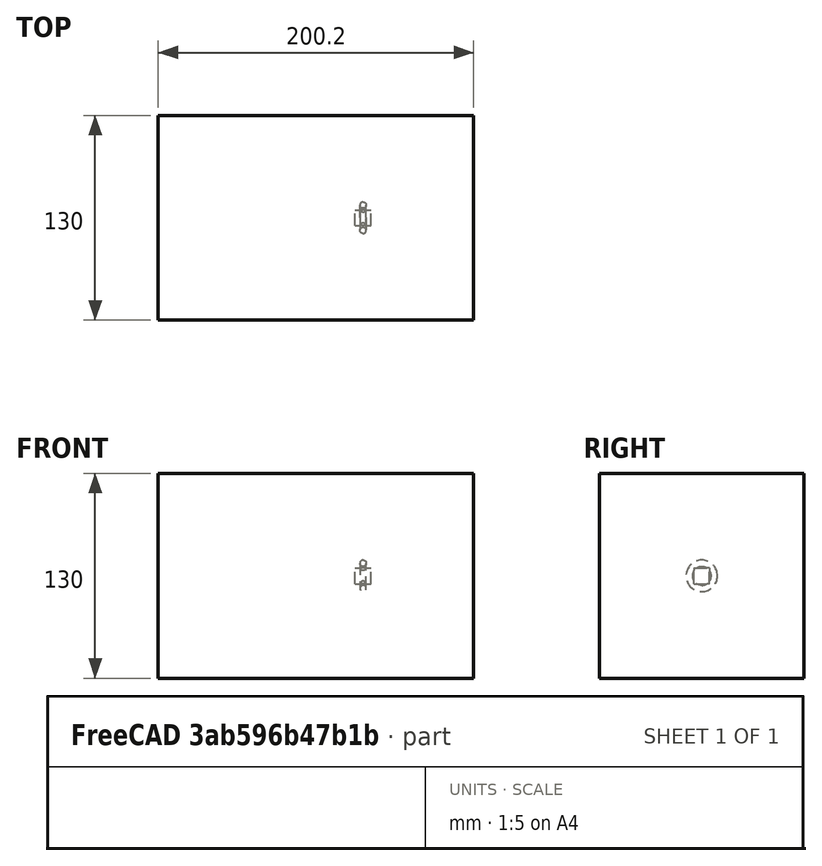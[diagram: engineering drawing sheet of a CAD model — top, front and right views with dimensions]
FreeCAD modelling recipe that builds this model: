
FCSTD DOCUMENT  (FreeCAD 0.21R33694 (Git))
Label: polarArray-7-array-translated
License: All rights reserved
objects: App::DocumentObjectGroupPython×1251, Part::FeaturePython×4, App::Part×2, Part::MultiFuse×1
note: 4 computed .brp shape members not serialized (recipe doc carries the construction recipe); baked Part::Feature solids carry a one-line shape summary decoded from their .brp

FEATURE [App::DocumentObjectGroupPython] HALFPI  # scripted group (container) (typed FeaturePython)
  name = HALFPI
  value = pi/2.
FEATURE [App::DocumentObjectGroupPython] PI  # scripted group (container) (typed FeaturePython)
  name = PI
  value = 1.*pi
FEATURE [App::DocumentObjectGroupPython] TWOPI  # scripted group (container) (typed FeaturePython)
  name = TWOPI
  value = 2.*pi
FEATURE [App::DocumentObjectGroupPython] Constants  # scripted group (container) (typed FeaturePython)
  Group = -> [HALFPI,PI,TWOPI]
FEATURE [App::DocumentObjectGroupPython] Variables  # scripted group (container) (typed FeaturePython)
FEATURE [App::DocumentObjectGroupPython] Quantities  # scripted group (container) (typed FeaturePython)
FEATURE [App::DocumentObjectGroupPython] Isotopes  # scripted group (container) (typed FeaturePython)
FEATURE [App::DocumentObjectGroupPython] Elements  # scripted group (container) (typed FeaturePython)
FEATURE [App::DocumentObjectGroupPython] Matrix  # scripted group (container) (typed FeaturePython)
FEATURE [App::DocumentObjectGroupPython] Surfaces  # scripted group (container) (typed FeaturePython)
FEATURE [App::DocumentObjectGroupPython] Opticals  # scripted group (container) (typed FeaturePython)
  Group = -> [Matrix,Surfaces]
FEATURE [App::DocumentObjectGroupPython] G4Isotopes  # scripted group (container) (typed FeaturePython)
FEATURE [App::DocumentObjectGroupPython] H_element  # scripted group (container) (typed FeaturePython)
  Z = 1
  atom_value = 1.008
  formula = H
  name = H_element
FEATURE [App::DocumentObjectGroupPython] He_element  # scripted group (container) (typed FeaturePython)
  Z = 2
  atom_value = 4.0026
  formula = He
  name = He_element
FEATURE [App::DocumentObjectGroupPython] Li_element  # scripted group (container) (typed FeaturePython)
  Z = 3
  atom_value = 6.94
  formula = Li
  name = Li_element
FEATURE [App::DocumentObjectGroupPython] Be_element  # scripted group (container) (typed FeaturePython)
  Z = 4
  atom_value = 9.01218
  formula = Be
  name = Be_element
FEATURE [App::DocumentObjectGroupPython] B_element  # scripted group (container) (typed FeaturePython)
  Z = 5
  atom_value = 10.81
  formula = B
  name = B_element
FEATURE [App::DocumentObjectGroupPython] C_element  # scripted group (container) (typed FeaturePython)
  Z = 6
  atom_value = 12.011
  formula = C
  name = C_element
FEATURE [App::DocumentObjectGroupPython] N_element  # scripted group (container) (typed FeaturePython)
  Z = 7
  atom_value = 14.007
  formula = N
  name = N_element
FEATURE [App::DocumentObjectGroupPython] O_element  # scripted group (container) (typed FeaturePython)
  Z = 8
  atom_value = 15.999
  formula = O
  name = O_element
FEATURE [App::DocumentObjectGroupPython] F_element  # scripted group (container) (typed FeaturePython)
  Z = 9
  atom_value = 18.9984
  formula = F
  name = F_element
FEATURE [App::DocumentObjectGroupPython] Ne_element  # scripted group (container) (typed FeaturePython)
  Z = 10
  atom_value = 20.1797
  formula = Ne
  name = Ne_element
FEATURE [App::DocumentObjectGroupPython] Na_element  # scripted group (container) (typed FeaturePython)
  Z = 11
  atom_value = 22.9898
  formula = Na
  name = Na_element
FEATURE [App::DocumentObjectGroupPython] Mg_element  # scripted group (container) (typed FeaturePython)
  Z = 12
  atom_value = 24.305
  formula = Mg
  name = Mg_element
FEATURE [App::DocumentObjectGroupPython] Al_element  # scripted group (container) (typed FeaturePython)
  Z = 13
  atom_value = 26.9815
  formula = Al
  name = Al_element
FEATURE [App::DocumentObjectGroupPython] Si_element  # scripted group (container) (typed FeaturePython)
  Z = 14
  atom_value = 28.085
  formula = Si
  name = Si_element
FEATURE [App::DocumentObjectGroupPython] P_element  # scripted group (container) (typed FeaturePython)
  Z = 15
  atom_value = 30.9738
  formula = P
  name = P_element
FEATURE [App::DocumentObjectGroupPython] S_element  # scripted group (container) (typed FeaturePython)
  Z = 16
  atom_value = 32.06
  formula = S
  name = S_element
FEATURE [App::DocumentObjectGroupPython] Cl_element  # scripted group (container) (typed FeaturePython)
  Z = 17
  atom_value = 35.45
  formula = Cl
  name = Cl_element
FEATURE [App::DocumentObjectGroupPython] Ar_element  # scripted group (container) (typed FeaturePython)
  Z = 18
  atom_value = 39.95
  formula = Ar
  name = Ar_element
FEATURE [App::DocumentObjectGroupPython] K_element  # scripted group (container) (typed FeaturePython)
  Z = 19
  atom_value = 39.0983
  formula = K
  name = K_element
FEATURE [App::DocumentObjectGroupPython] Ca_element  # scripted group (container) (typed FeaturePython)
  Z = 20
  atom_value = 40.078
  formula = Ca
  name = Ca_element
FEATURE [App::DocumentObjectGroupPython] Sc_element  # scripted group (container) (typed FeaturePython)
  Z = 21
  atom_value = 44.9559
  formula = Sc
  name = Sc_element
FEATURE [App::DocumentObjectGroupPython] Ti_element  # scripted group (container) (typed FeaturePython)
  Z = 22
  atom_value = 47.867
  formula = Ti
  name = Ti_element
FEATURE [App::DocumentObjectGroupPython] V_element  # scripted group (container) (typed FeaturePython)
  Z = 23
  atom_value = 50.9415
  formula = V
  name = V_element
FEATURE [App::DocumentObjectGroupPython] Cr_element  # scripted group (container) (typed FeaturePython)
  Z = 24
  atom_value = 51.9961
  formula = Cr
  name = Cr_element
FEATURE [App::DocumentObjectGroupPython] Mn_element  # scripted group (container) (typed FeaturePython)
  Z = 25
  atom_value = 54.938
  formula = Mn
  name = Mn_element
FEATURE [App::DocumentObjectGroupPython] Fe_element  # scripted group (container) (typed FeaturePython)
  Z = 26
  atom_value = 55.845
  formula = Fe
  name = Fe_element
FEATURE [App::DocumentObjectGroupPython] Co_element  # scripted group (container) (typed FeaturePython)
  Z = 27
  atom_value = 58.9332
  formula = Co
  name = Co_element
FEATURE [App::DocumentObjectGroupPython] Ni_element  # scripted group (container) (typed FeaturePython)
  Z = 28
  atom_value = 58.6934
  formula = Ni
  name = Ni_element
FEATURE [App::DocumentObjectGroupPython] Cu_element  # scripted group (container) (typed FeaturePython)
  Z = 29
  atom_value = 63.546
  formula = Cu
  name = Cu_element
FEATURE [App::DocumentObjectGroupPython] Zn_element  # scripted group (container) (typed FeaturePython)
  Z = 30
  atom_value = 65.38
  formula = Zn
  name = Zn_element
FEATURE [App::DocumentObjectGroupPython] Ga_element  # scripted group (container) (typed FeaturePython)
  Z = 31
  atom_value = 69.723
  formula = Ga
  name = Ga_element
FEATURE [App::DocumentObjectGroupPython] Ge_element  # scripted group (container) (typed FeaturePython)
  Z = 32
  atom_value = 72.63
  formula = Ge
  name = Ge_element
FEATURE [App::DocumentObjectGroupPython] As_element  # scripted group (container) (typed FeaturePython)
  Z = 33
  atom_value = 74.9216
  formula = As
  name = As_element
FEATURE [App::DocumentObjectGroupPython] Se_element  # scripted group (container) (typed FeaturePython)
  Z = 34
  atom_value = 78.971
  formula = Se
  name = Se_element
FEATURE [App::DocumentObjectGroupPython] Br_element  # scripted group (container) (typed FeaturePython)
  Z = 35
  atom_value = 79.904
  formula = Br
  name = Br_element
FEATURE [App::DocumentObjectGroupPython] Kr_element  # scripted group (container) (typed FeaturePython)
  Z = 36
  atom_value = 83.798
  formula = Kr
  name = Kr_element
FEATURE [App::DocumentObjectGroupPython] Rb_element  # scripted group (container) (typed FeaturePython)
  Z = 37
  atom_value = 85.4678
  formula = Rb
  name = Rb_element
FEATURE [App::DocumentObjectGroupPython] Sr_element  # scripted group (container) (typed FeaturePython)
  Z = 38
  atom_value = 87.62
  formula = Sr
  name = Sr_element
FEATURE [App::DocumentObjectGroupPython] Y_element  # scripted group (container) (typed FeaturePython)
  Z = 39
  atom_value = 88.9058
  formula = Y
  name = Y_element
FEATURE [App::DocumentObjectGroupPython] Zr_element  # scripted group (container) (typed FeaturePython)
  Z = 40
  atom_value = 91.224
  formula = Zr
  name = Zr_element
FEATURE [App::DocumentObjectGroupPython] Nb_element  # scripted group (container) (typed FeaturePython)
  Z = 41
  atom_value = 92.9064
  formula = Nb
  name = Nb_element
FEATURE [App::DocumentObjectGroupPython] Mo_element  # scripted group (container) (typed FeaturePython)
  Z = 42
  atom_value = 95.95
  formula = Mo
  name = Mo_element
FEATURE [App::DocumentObjectGroupPython] Tc_element  # scripted group (container) (typed FeaturePython)
  Z = 43
  atom_value = 97
  formula = Tc
  name = Tc_element
FEATURE [App::DocumentObjectGroupPython] Ru_element  # scripted group (container) (typed FeaturePython)
  Z = 44
  atom_value = 101.07
  formula = Ru
  name = Ru_element
FEATURE [App::DocumentObjectGroupPython] Rh_element  # scripted group (container) (typed FeaturePython)
  Z = 45
  atom_value = 102.905
  formula = Rh
  name = Rh_element
FEATURE [App::DocumentObjectGroupPython] Pd_element  # scripted group (container) (typed FeaturePython)
  Z = 46
  atom_value = 106.42
  formula = Pd
  name = Pd_element
FEATURE [App::DocumentObjectGroupPython] Ag_element  # scripted group (container) (typed FeaturePython)
  Z = 47
  atom_value = 107.868
  formula = Ag
  name = Ag_element
FEATURE [App::DocumentObjectGroupPython] Cd_element  # scripted group (container) (typed FeaturePython)
  Z = 48
  atom_value = 112.414
  formula = Cd
  name = Cd_element
FEATURE [App::DocumentObjectGroupPython] In_element  # scripted group (container) (typed FeaturePython)
  Z = 49
  atom_value = 114.818
  formula = In
  name = In_element
FEATURE [App::DocumentObjectGroupPython] Sn_element  # scripted group (container) (typed FeaturePython)
  Z = 50
  atom_value = 118.71
  formula = Sn
  name = Sn_element
FEATURE [App::DocumentObjectGroupPython] Sb_element  # scripted group (container) (typed FeaturePython)
  Z = 51
  atom_value = 121.76
  formula = Sb
  name = Sb_element
FEATURE [App::DocumentObjectGroupPython] Te_element  # scripted group (container) (typed FeaturePython)
  Z = 52
  atom_value = 127.6
  formula = Te
  name = Te_element
FEATURE [App::DocumentObjectGroupPython] I_element  # scripted group (container) (typed FeaturePython)
  Z = 53
  atom_value = 126.904
  formula = I
  name = I_element
FEATURE [App::DocumentObjectGroupPython] Xe_element  # scripted group (container) (typed FeaturePython)
  Z = 54
  atom_value = 131.293
  formula = Xe
  name = Xe_element
FEATURE [App::DocumentObjectGroupPython] Cs_element  # scripted group (container) (typed FeaturePython)
  Z = 55
  atom_value = 132.905
  formula = Cs
  name = Cs_element
FEATURE [App::DocumentObjectGroupPython] Ba_element  # scripted group (container) (typed FeaturePython)
  Z = 56
  atom_value = 137.327
  formula = Ba
  name = Ba_element
FEATURE [App::DocumentObjectGroupPython] La_element  # scripted group (container) (typed FeaturePython)
  Z = 57
  atom_value = 138.905
  formula = La
  name = La_element
FEATURE [App::DocumentObjectGroupPython] Ce_element  # scripted group (container) (typed FeaturePython)
  Z = 58
  atom_value = 140.116
  formula = Ce
  name = Ce_element
FEATURE [App::DocumentObjectGroupPython] Pr_element  # scripted group (container) (typed FeaturePython)
  Z = 59
  atom_value = 140.908
  formula = Pr
  name = Pr_element
FEATURE [App::DocumentObjectGroupPython] Nd_element  # scripted group (container) (typed FeaturePython)
  Z = 60
  atom_value = 144.242
  formula = Nd
  name = Nd_element
FEATURE [App::DocumentObjectGroupPython] Pm_element  # scripted group (container) (typed FeaturePython)
  Z = 61
  atom_value = 145
  formula = Pm
  name = Pm_element
FEATURE [App::DocumentObjectGroupPython] Sm_element  # scripted group (container) (typed FeaturePython)
  Z = 62
  atom_value = 150.36
  formula = Sm
  name = Sm_element
FEATURE [App::DocumentObjectGroupPython] Eu_element  # scripted group (container) (typed FeaturePython)
  Z = 63
  atom_value = 151.964
  formula = Eu
  name = Eu_element
FEATURE [App::DocumentObjectGroupPython] Gd_element  # scripted group (container) (typed FeaturePython)
  Z = 64
  atom_value = 157.25
  formula = Gd
  name = Gd_element
FEATURE [App::DocumentObjectGroupPython] Tb_element  # scripted group (container) (typed FeaturePython)
  Z = 65
  atom_value = 158.925
  formula = Tb
  name = Tb_element
FEATURE [App::DocumentObjectGroupPython] Dy_element  # scripted group (container) (typed FeaturePython)
  Z = 66
  atom_value = 162.5
  formula = Dy
  name = Dy_element
FEATURE [App::DocumentObjectGroupPython] Ho_element  # scripted group (container) (typed FeaturePython)
  Z = 67
  atom_value = 164.93
  formula = Ho
  name = Ho_element
FEATURE [App::DocumentObjectGroupPython] Er_element  # scripted group (container) (typed FeaturePython)
  Z = 68
  atom_value = 167.259
  formula = Er
  name = Er_element
FEATURE [App::DocumentObjectGroupPython] Tm_element  # scripted group (container) (typed FeaturePython)
  Z = 69
  atom_value = 168.934
  formula = Tm
  name = Tm_element
FEATURE [App::DocumentObjectGroupPython] Yb_element  # scripted group (container) (typed FeaturePython)
  Z = 70
  atom_value = 173.045
  formula = Yb
  name = Yb_element
FEATURE [App::DocumentObjectGroupPython] Lu_element  # scripted group (container) (typed FeaturePython)
  Z = 71
  atom_value = 174.967
  formula = Lu
  name = Lu_element
FEATURE [App::DocumentObjectGroupPython] Hf_element  # scripted group (container) (typed FeaturePython)
  Z = 72
  atom_value = 178.49
  formula = Hf
  name = Hf_element
FEATURE [App::DocumentObjectGroupPython] Ta_element  # scripted group (container) (typed FeaturePython)
  Z = 73
  atom_value = 180.948
  formula = Ta
  name = Ta_element
FEATURE [App::DocumentObjectGroupPython] W_element  # scripted group (container) (typed FeaturePython)
  Z = 74
  atom_value = 183.84
  formula = W
  name = W_element
FEATURE [App::DocumentObjectGroupPython] Re_element  # scripted group (container) (typed FeaturePython)
  Z = 75
  atom_value = 186.207
  formula = Re
  name = Re_element
FEATURE [App::DocumentObjectGroupPython] Os_element  # scripted group (container) (typed FeaturePython)
  Z = 76
  atom_value = 190.23
  formula = Os
  name = Os_element
FEATURE [App::DocumentObjectGroupPython] Ir_element  # scripted group (container) (typed FeaturePython)
  Z = 77
  atom_value = 192.217
  formula = Ir
  name = Ir_element
FEATURE [App::DocumentObjectGroupPython] Pt_element  # scripted group (container) (typed FeaturePython)
  Z = 78
  atom_value = 195.084
  formula = Pt
  name = Pt_element
FEATURE [App::DocumentObjectGroupPython] Au_element  # scripted group (container) (typed FeaturePython)
  Z = 79
  atom_value = 196.967
  formula = Au
  name = Au_element
FEATURE [App::DocumentObjectGroupPython] Hg_element  # scripted group (container) (typed FeaturePython)
  Z = 80
  atom_value = 200.592
  formula = Hg
  name = Hg_element
FEATURE [App::DocumentObjectGroupPython] Tl_element  # scripted group (container) (typed FeaturePython)
  Z = 81
  atom_value = 204.38
  formula = Tl
  name = Tl_element
FEATURE [App::DocumentObjectGroupPython] Pb_element  # scripted group (container) (typed FeaturePython)
  Z = 82
  atom_value = 207.2
  formula = Pb
  name = Pb_element
FEATURE [App::DocumentObjectGroupPython] Bi_element  # scripted group (container) (typed FeaturePython)
  Z = 83
  atom_value = 208.98
  formula = Bi
  name = Bi_element
FEATURE [App::DocumentObjectGroupPython] Po_element  # scripted group (container) (typed FeaturePython)
  Z = 84
  atom_value = 209
  formula = Po
  name = Po_element
FEATURE [App::DocumentObjectGroupPython] At_element  # scripted group (container) (typed FeaturePython)
  Z = 85
  atom_value = 210
  formula = At
  name = At_element
FEATURE [App::DocumentObjectGroupPython] Rn_element  # scripted group (container) (typed FeaturePython)
  Z = 86
  atom_value = 222
  formula = Rn
  name = Rn_element
FEATURE [App::DocumentObjectGroupPython] Fr_element  # scripted group (container) (typed FeaturePython)
  Z = 87
  atom_value = 223
  formula = Fr
  name = Fr_element
FEATURE [App::DocumentObjectGroupPython] Ra_element  # scripted group (container) (typed FeaturePython)
  Z = 88
  atom_value = 226
  formula = Ra
  name = Ra_element
FEATURE [App::DocumentObjectGroupPython] Ac_element  # scripted group (container) (typed FeaturePython)
  Z = 89
  atom_value = 227
  formula = Ac
  name = Ac_element
FEATURE [App::DocumentObjectGroupPython] Th_element  # scripted group (container) (typed FeaturePython)
  Z = 90
  atom_value = 232.038
  formula = Th
  name = Th_element
FEATURE [App::DocumentObjectGroupPython] Pa_element  # scripted group (container) (typed FeaturePython)
  Z = 91
  atom_value = 231.036
  formula = Pa
  name = Pa_element
FEATURE [App::DocumentObjectGroupPython] U_element  # scripted group (container) (typed FeaturePython)
  Z = 92
  atom_value = 238.029
  formula = U
  name = U_element
FEATURE [App::DocumentObjectGroupPython] Np_element  # scripted group (container) (typed FeaturePython)
  Z = 93
  atom_value = 237
  formula = Np
  name = Np_element
FEATURE [App::DocumentObjectGroupPython] Pu_element  # scripted group (container) (typed FeaturePython)
  Z = 94
  atom_value = 244
  formula = Pu
  name = Pu_element
FEATURE [App::DocumentObjectGroupPython] Am_element  # scripted group (container) (typed FeaturePython)
  Z = 95
  atom_value = 243
  formula = Am
  name = Am_element
FEATURE [App::DocumentObjectGroupPython] Cm_element  # scripted group (container) (typed FeaturePython)
  Z = 96
  atom_value = 247
  formula = Cm
  name = Cm_element
FEATURE [App::DocumentObjectGroupPython] Bk_element  # scripted group (container) (typed FeaturePython)
  Z = 97
  atom_value = 247
  formula = Bk
  name = Bk_element
FEATURE [App::DocumentObjectGroupPython] Cf_element  # scripted group (container) (typed FeaturePython)
  Z = 98
  atom_value = 251
  formula = Cf
  name = Cf_element
FEATURE [App::DocumentObjectGroupPython] G4Elements  # scripted group (container) (typed FeaturePython)
  Group = -> [H_element,He_element,Li_element,Be_element,B_element,C_element,N_element,O_element,F_element,Ne_element,Na_element,Mg_element,Al_element,Si_element,P_element,S_element,Cl_element,Ar_element,K_element,Ca_element,Sc_element,Ti_element,V_element,Cr_element,Mn_element,Fe_element,Co_element,Ni_element,Cu_element,Zn_element,Ga_element,Ge_element,As_element,Se_element,Br_element,Kr_element,Rb_element,+61 more]
FEATURE [App::DocumentObjectGroupPython] H_element001  label="H_element : 0.101"  # scripted group (container) (typed FeaturePython)
  n = 0.101327
FEATURE [App::DocumentObjectGroupPython] C_element001  label="C_element : 0.775"  # scripted group (container) (typed FeaturePython)
  n = 0.7755
FEATURE [App::DocumentObjectGroupPython] N_element001  label="N_element : 0.035"  # scripted group (container) (typed FeaturePython)
  n = 0.035057
FEATURE [App::DocumentObjectGroupPython] O_element001  label="O_element : 0.052"  # scripted group (container) (typed FeaturePython)
  n = 0.0523159
FEATURE [App::DocumentObjectGroupPython] F_element001  label="F_element : 0.017"  # scripted group (container) (typed FeaturePython)
  n = 0.017422
FEATURE [App::DocumentObjectGroupPython] Ca_element001  label="Ca_element : 0.018"  # scripted group (container) (typed FeaturePython)
  n = 0.018378
FEATURE [App::DocumentObjectGroupPython] G4_A_150_TISSUE  label="G4_A-150_TISSUE"  # scripted group (container) (typed FeaturePython)
  Dunit = g/cm3
  Dvalue = 1.127
  Group = -> [H_element001,C_element001,N_element001,O_element001,F_element001,Ca_element001]
  conduct = 2
  density = 1
  expand = 3
  formula = G4_A-150_TISSUE
  name = G4_A-150_TISSUE
  specific = 4
FEATURE [App::DocumentObjectGroupPython] C_element002  label="C_element : 3"  # scripted group (container) (typed FeaturePython)
  n = 3
  ref = C_element
FEATURE [App::DocumentObjectGroupPython] H_element002  label="H_element : 6"  # scripted group (container) (typed FeaturePython)
  n = 6
  ref = H_element
FEATURE [App::DocumentObjectGroupPython] O_element002  label="O_element : 1"  # scripted group (container) (typed FeaturePython)
  n = 1
  ref = O_element
FEATURE [App::DocumentObjectGroupPython] G4_ACETONE  # scripted group (container) (typed FeaturePython)
  Dunit = g/cm3
  Dvalue = 0.7899
  Group = -> [C_element002,H_element002,O_element002]
  conduct = 2
  density = 1
  expand = 3
  formula = G4_ACETONE
  name = G4_ACETONE
  specific = 4
FEATURE [App::DocumentObjectGroupPython] C_element003  label="C_element : 2"  # scripted group (container) (typed FeaturePython)
  n = 2
  ref = C_element
FEATURE [App::DocumentObjectGroupPython] H_element003  label="H_element : 2"  # scripted group (container) (typed FeaturePython)
  n = 2
  ref = H_element
FEATURE [App::DocumentObjectGroupPython] G4_ACETYLENE  # scripted group (container) (typed FeaturePython)
  Dunit = g/cm3
  Dvalue = 0.0010967
  Group = -> [C_element003,H_element003]
  conduct = 2
  density = 1
  expand = 3
  formula = G4_ACETYLENE
  name = G4_ACETYLENE
  specific = 4
FEATURE [App::DocumentObjectGroupPython] C_element004  label="C_element : 5"  # scripted group (container) (typed FeaturePython)
  n = 5
  ref = C_element
FEATURE [App::DocumentObjectGroupPython] H_element004  label="H_element : 5"  # scripted group (container) (typed FeaturePython)
  n = 5
  ref = H_element
FEATURE [App::DocumentObjectGroupPython] N_element002  label="N_element : 5"  # scripted group (container) (typed FeaturePython)
  n = 5
  ref = N_element
FEATURE [App::DocumentObjectGroupPython] G4_ADENINE  # scripted group (container) (typed FeaturePython)
  Dunit = g/cm3
  Dvalue = 1.6
  Group = -> [C_element004,H_element004,N_element002]
  conduct = 2
  density = 1
  expand = 3
  formula = G4_ADENINE
  name = G4_ADENINE
  specific = 4
FEATURE [App::DocumentObjectGroupPython] H_element005  label="H_element : 0.114"  # scripted group (container) (typed FeaturePython)
  n = 0.114
FEATURE [App::DocumentObjectGroupPython] C_element005  label="C_element : 0.598"  # scripted group (container) (typed FeaturePython)
  n = 0.598
FEATURE [App::DocumentObjectGroupPython] N_element003  label="N_element : 0.007"  # scripted group (container) (typed FeaturePython)
  n = 0.007
FEATURE [App::DocumentObjectGroupPython] O_element003  label="O_element : 0.278"  # scripted group (container) (typed FeaturePython)
  n = 0.278
FEATURE [App::DocumentObjectGroupPython] Na_element001  label="Na_element : 0.001"  # scripted group (container) (typed FeaturePython)
  n = 0.001
FEATURE [App::DocumentObjectGroupPython] S_element001  label="S_element : 0.001"  # scripted group (container) (typed FeaturePython)
  n = 0.001
FEATURE [App::DocumentObjectGroupPython] Cl_element001  label="Cl_element : 0.001"  # scripted group (container) (typed FeaturePython)
  n = 0.001
FEATURE [App::DocumentObjectGroupPython] G4_ADIPOSE_TISSUE_ICRP  # scripted group (container) (typed FeaturePython)
  Dunit = g/cm3
  Dvalue = 0.95
  Group = -> [H_element005,C_element005,N_element003,O_element003,Na_element001,S_element001,Cl_element001]
  conduct = 2
  density = 1
  expand = 3
  formula = G4_ADIPOSE_TISSUE_ICRP
  name = G4_ADIPOSE_TISSUE_ICRP
  specific = 4
FEATURE [App::DocumentObjectGroupPython] C_element006  label="C_element : 0.000"  # scripted group (container) (typed FeaturePython)
  n = 0.000124
FEATURE [App::DocumentObjectGroupPython] N_element004  label="N_element : 0.755"  # scripted group (container) (typed FeaturePython)
  n = 0.755268
FEATURE [App::DocumentObjectGroupPython] O_element004  label="O_element : 0.232"  # scripted group (container) (typed FeaturePython)
  n = 0.231781
FEATURE [App::DocumentObjectGroupPython] Ar_element001  label="Ar_element : 0.013"  # scripted group (container) (typed FeaturePython)
  n = 0.012827
FEATURE [App::DocumentObjectGroupPython] G4_AIR  # scripted group (container) (typed FeaturePython)
  Dunit = g/cm3
  Dvalue = 0.00120479
  Group = -> [C_element006,N_element004,O_element004,Ar_element001]
  conduct = 2
  density = 1
  expand = 3
  formula = G4_AIR
  name = G4_AIR
  specific = 4
FEATURE [App::DocumentObjectGroupPython] C_element007  label="C_element : 006"  # scripted group (container) (typed FeaturePython)
  n = 3
  ref = C_element
FEATURE [App::DocumentObjectGroupPython] H_element006  label="H_element : 7"  # scripted group (container) (typed FeaturePython)
  n = 7
  ref = H_element
FEATURE [App::DocumentObjectGroupPython] N_element005  label="N_element : 1"  # scripted group (container) (typed FeaturePython)
  n = 1
  ref = N_element
FEATURE [App::DocumentObjectGroupPython] O_element005  label="O_element : 2"  # scripted group (container) (typed FeaturePython)
  n = 2
  ref = O_element
FEATURE [App::DocumentObjectGroupPython] G4_ALANINE  # scripted group (container) (typed FeaturePython)
  Dunit = g/cm3
  Dvalue = 1.42
  Group = -> [C_element007,H_element006,N_element005,O_element005]
  conduct = 2
  density = 1
  expand = 3
  formula = G4_ALANINE
  name = G4_ALANINE
  specific = 4
FEATURE [App::DocumentObjectGroupPython] Al_element001  label="Al_element : 2"  # scripted group (container) (typed FeaturePython)
  n = 2
  ref = Al_element
FEATURE [App::DocumentObjectGroupPython] O_element006  label="O_element : 3"  # scripted group (container) (typed FeaturePython)
  n = 3
  ref = O_element
FEATURE [App::DocumentObjectGroupPython] G4_ALUMINUM_OXIDE  # scripted group (container) (typed FeaturePython)
  Dunit = g/cm3
  Dvalue = 3.97
  Group = -> [Al_element001,O_element006]
  conduct = 2
  density = 1
  expand = 3
  formula = G4_ALUMINUM_OXIDE
  name = G4_ALUMINUM_OXIDE
  specific = 4
FEATURE [App::DocumentObjectGroupPython] H_element007  label="H_element : 0.106"  # scripted group (container) (typed FeaturePython)
  n = 0.10593
FEATURE [App::DocumentObjectGroupPython] C_element008  label="C_element : 0.789"  # scripted group (container) (typed FeaturePython)
  n = 0.788974
FEATURE [App::DocumentObjectGroupPython] O_element007  label="O_element : 0.105"  # scripted group (container) (typed FeaturePython)
  n = 0.105096
FEATURE [App::DocumentObjectGroupPython] G4_AMBER  # scripted group (container) (typed FeaturePython)
  Dunit = g/cm3
  Dvalue = 1.1
  Group = -> [H_element007,C_element008,O_element007]
  conduct = 2
  density = 1
  expand = 3
  formula = G4_AMBER
  name = G4_AMBER
  specific = 4
FEATURE [App::DocumentObjectGroupPython] N_element006  label="N_element : 006"  # scripted group (container) (typed FeaturePython)
  n = 1
  ref = N_element
FEATURE [App::DocumentObjectGroupPython] H_element008  label="H_element : 3"  # scripted group (container) (typed FeaturePython)
  n = 3
  ref = H_element
FEATURE [App::DocumentObjectGroupPython] G4_AMMONIA  # scripted group (container) (typed FeaturePython)
  Dunit = g/cm3
  Dvalue = 0.000826019
  Group = -> [N_element006,H_element008]
  conduct = 2
  density = 1
  expand = 3
  formula = G4_AMMONIA
  name = G4_AMMONIA
  specific = 4
FEATURE [App::DocumentObjectGroupPython] C_element009  label="C_element : 6"  # scripted group (container) (typed FeaturePython)
  n = 6
  ref = C_element
FEATURE [App::DocumentObjectGroupPython] H_element009  label="H_element : 008"  # scripted group (container) (typed FeaturePython)
  n = 7
  ref = H_element
FEATURE [App::DocumentObjectGroupPython] N_element007  label="N_element : 007"  # scripted group (container) (typed FeaturePython)
  n = 1
  ref = N_element
FEATURE [App::DocumentObjectGroupPython] G4_ANILINE  # scripted group (container) (typed FeaturePython)
  Dunit = g/cm3
  Dvalue = 1.0235
  Group = -> [C_element009,H_element009,N_element007]
  conduct = 2
  density = 1
  expand = 3
  formula = G4_ANILINE
  name = G4_ANILINE
  specific = 4
FEATURE [App::DocumentObjectGroupPython] C_element010  label="C_element : 14"  # scripted group (container) (typed FeaturePython)
  n = 14
  ref = C_element
FEATURE [App::DocumentObjectGroupPython] H_element010  label="H_element : 10"  # scripted group (container) (typed FeaturePython)
  n = 10
  ref = H_element
FEATURE [App::DocumentObjectGroupPython] G4_ANTHRACENE  # scripted group (container) (typed FeaturePython)
  Dunit = g/cm3
  Dvalue = 1.283
  Group = -> [C_element010,H_element010]
  conduct = 2
  density = 1
  expand = 3
  formula = G4_ANTHRACENE
  name = G4_ANTHRACENE
  specific = 4
FEATURE [App::DocumentObjectGroupPython] H_element011  label="H_element : 0.065"  # scripted group (container) (typed FeaturePython)
  n = 0.0654709
FEATURE [App::DocumentObjectGroupPython] C_element011  label="C_element : 0.537"  # scripted group (container) (typed FeaturePython)
  n = 0.536944
FEATURE [App::DocumentObjectGroupPython] N_element008  label="N_element : 0.021"  # scripted group (container) (typed FeaturePython)
  n = 0.0215
FEATURE [App::DocumentObjectGroupPython] O_element008  label="O_element : 0.032"  # scripted group (container) (typed FeaturePython)
  n = 0.032085
FEATURE [App::DocumentObjectGroupPython] F_element002  label="F_element : 0.167"  # scripted group (container) (typed FeaturePython)
  n = 0.167411
FEATURE [App::DocumentObjectGroupPython] Ca_element002  label="Ca_element : 0.177"  # scripted group (container) (typed FeaturePython)
  n = 0.176589
FEATURE [App::DocumentObjectGroupPython] G4_B_100_BONE  label="G4_B-100_BONE"  # scripted group (container) (typed FeaturePython)
  Dunit = g/cm3
  Dvalue = 1.45
  Group = -> [H_element011,C_element011,N_element008,O_element008,F_element002,Ca_element002]
  conduct = 2
  density = 1
  expand = 3
  formula = G4_B-100_BONE
  name = G4_B-100_BONE
  specific = 4
FEATURE [App::DocumentObjectGroupPython] H_element012  label="H_element : 0.057"  # scripted group (container) (typed FeaturePython)
  n = 0.057441
FEATURE [App::DocumentObjectGroupPython] C_element012  label="C_element : 0.790"  # scripted group (container) (typed FeaturePython)
  n = 0.774591
FEATURE [App::DocumentObjectGroupPython] O_element009  label="O_element : 0.168"  # scripted group (container) (typed FeaturePython)
  n = 0.167968
FEATURE [App::DocumentObjectGroupPython] G4_BAKELITE  # scripted group (container) (typed FeaturePython)
  Dunit = g/cm3
  Dvalue = 1.25
  Group = -> [H_element012,C_element012,O_element009]
  conduct = 2
  density = 1
  expand = 3
  formula = G4_BAKELITE
  name = G4_BAKELITE
  specific = 4
FEATURE [App::DocumentObjectGroupPython] Ba_element001  label="Ba_element : 1"  # scripted group (container) (typed FeaturePython)
  n = 1
  ref = Ba_element
FEATURE [App::DocumentObjectGroupPython] F_element003  label="F_element : 2"  # scripted group (container) (typed FeaturePython)
  n = 2
  ref = F_element
FEATURE [App::DocumentObjectGroupPython] G4_BARIUM_FLUORIDE  # scripted group (container) (typed FeaturePython)
  Dunit = g/cm3
  Dvalue = 4.89
  Group = -> [Ba_element001,F_element003]
  conduct = 2
  density = 1
  expand = 3
  formula = G4_BARIUM_FLUORIDE
  name = G4_BARIUM_FLUORIDE
  specific = 4
FEATURE [App::DocumentObjectGroupPython] Ba_element002  label="Ba_element : 002"  # scripted group (container) (typed FeaturePython)
  n = 1
  ref = Ba_element
FEATURE [App::DocumentObjectGroupPython] S_element002  label="S_element : 1"  # scripted group (container) (typed FeaturePython)
  n = 1
  ref = S_element
FEATURE [App::DocumentObjectGroupPython] O_element010  label="O_element : 4"  # scripted group (container) (typed FeaturePython)
  n = 4
  ref = O_element
FEATURE [App::DocumentObjectGroupPython] G4_BARIUM_SULFATE  # scripted group (container) (typed FeaturePython)
  Dunit = g/cm3
  Dvalue = 4.5
  Group = -> [Ba_element002,S_element002,O_element010]
  conduct = 2
  density = 1
  expand = 3
  formula = G4_BARIUM_SULFATE
  name = G4_BARIUM_SULFATE
  specific = 4
FEATURE [App::DocumentObjectGroupPython] C_element013  label="C_element : 007"  # scripted group (container) (typed FeaturePython)
  n = 6
  ref = C_element
FEATURE [App::DocumentObjectGroupPython] H_element013  label="H_element : 009"  # scripted group (container) (typed FeaturePython)
  n = 6
  ref = H_element
FEATURE [App::DocumentObjectGroupPython] G4_BENZENE  # scripted group (container) (typed FeaturePython)
  Dunit = g/cm3
  Dvalue = 0.87865
  Group = -> [C_element013,H_element013]
  conduct = 2
  density = 1
  expand = 3
  formula = G4_BENZENE
  name = G4_BENZENE
  specific = 4
FEATURE [App::DocumentObjectGroupPython] Be_element001  label="Be_element : 1"  # scripted group (container) (typed FeaturePython)
  n = 1
  ref = Be_element
FEATURE [App::DocumentObjectGroupPython] O_element011  label="O_element : 005"  # scripted group (container) (typed FeaturePython)
  n = 1
  ref = O_element
FEATURE [App::DocumentObjectGroupPython] G4_BERYLLIUM_OXIDE  # scripted group (container) (typed FeaturePython)
  Dunit = g/cm3
  Dvalue = 3.01
  Group = -> [Be_element001,O_element011]
  conduct = 2
  density = 1
  expand = 3
  formula = G4_BERYLLIUM_OXIDE
  name = G4_BERYLLIUM_OXIDE
  specific = 4
FEATURE [App::DocumentObjectGroupPython] Bi_element001  label="Bi_element : 4"  # scripted group (container) (typed FeaturePython)
  n = 4
  ref = Bi_element
FEATURE [App::DocumentObjectGroupPython] Ge_element001  label="Ge_element : 3"  # scripted group (container) (typed FeaturePython)
  n = 3
  ref = Ge_element
FEATURE [App::DocumentObjectGroupPython] O_element012  label="O_element : 12"  # scripted group (container) (typed FeaturePython)
  n = 12
  ref = O_element
FEATURE [App::DocumentObjectGroupPython] G4_BGO  # scripted group (container) (typed FeaturePython)
  Dunit = g/cm3
  Dvalue = 7.13
  Group = -> [Bi_element001,Ge_element001,O_element012]
  conduct = 2
  density = 1
  expand = 3
  formula = G4_BGO
  name = G4_BGO
  specific = 4
FEATURE [App::DocumentObjectGroupPython] H_element014  label="H_element : 0.102"  # scripted group (container) (typed FeaturePython)
  n = 0.102
FEATURE [App::DocumentObjectGroupPython] C_element014  label="C_element : 0.110"  # scripted group (container) (typed FeaturePython)
  n = 0.11
FEATURE [App::DocumentObjectGroupPython] N_element009  label="N_element : 0.033"  # scripted group (container) (typed FeaturePython)
  n = 0.033
FEATURE [App::DocumentObjectGroupPython] O_element013  label="O_element : 0.745"  # scripted group (container) (typed FeaturePython)
  n = 0.745
FEATURE [App::DocumentObjectGroupPython] Na_element002  label="Na_element : 0.002"  # scripted group (container) (typed FeaturePython)
  n = 0.001
FEATURE [App::DocumentObjectGroupPython] P_element001  label="P_element : 0.001"  # scripted group (container) (typed FeaturePython)
  n = 0.001
FEATURE [App::DocumentObjectGroupPython] S_element003  label="S_element : 0.002"  # scripted group (container) (typed FeaturePython)
  n = 0.002
FEATURE [App::DocumentObjectGroupPython] Cl_element002  label="Cl_element : 0.003"  # scripted group (container) (typed FeaturePython)
  n = 0.003
FEATURE [App::DocumentObjectGroupPython] K_element001  label="K_element : 0.002"  # scripted group (container) (typed FeaturePython)
  n = 0.002
FEATURE [App::DocumentObjectGroupPython] Fe_element001  label="Fe_element : 0.001"  # scripted group (container) (typed FeaturePython)
  n = 0.001
FEATURE [App::DocumentObjectGroupPython] G4_BLOOD_ICRP  # scripted group (container) (typed FeaturePython)
  Dunit = g/cm3
  Dvalue = 1.06
  Group = -> [H_element014,C_element014,N_element009,O_element013,Na_element002,P_element001,S_element003,Cl_element002,K_element001,Fe_element001]
  conduct = 2
  density = 1
  expand = 3
  formula = G4_BLOOD_ICRP
  name = G4_BLOOD_ICRP
  specific = 4
FEATURE [App::DocumentObjectGroupPython] H_element015  label="H_element : 0.064"  # scripted group (container) (typed FeaturePython)
  n = 0.064
FEATURE [App::DocumentObjectGroupPython] C_element015  label="C_element : 0.278"  # scripted group (container) (typed FeaturePython)
  n = 0.278
FEATURE [App::DocumentObjectGroupPython] N_element010  label="N_element : 0.027"  # scripted group (container) (typed FeaturePython)
  n = 0.027
FEATURE [App::DocumentObjectGroupPython] O_element014  label="O_element : 0.410"  # scripted group (container) (typed FeaturePython)
  n = 0.41
FEATURE [App::DocumentObjectGroupPython] Mg_element001  label="Mg_element : 0.002"  # scripted group (container) (typed FeaturePython)
  n = 0.002
FEATURE [App::DocumentObjectGroupPython] P_element002  label="P_element : 0.070"  # scripted group (container) (typed FeaturePython)
  n = 0.07
FEATURE [App::DocumentObjectGroupPython] S_element004  label="S_element : 0.003"  # scripted group (container) (typed FeaturePython)
  n = 0.002
FEATURE [App::DocumentObjectGroupPython] Ca_element003  label="Ca_element : 0.147"  # scripted group (container) (typed FeaturePython)
  n = 0.147
FEATURE [App::DocumentObjectGroupPython] G4_BONE_COMPACT_ICRU  # scripted group (container) (typed FeaturePython)
  Dunit = g/cm3
  Dvalue = 1.85
  Group = -> [H_element015,C_element015,N_element010,O_element014,Mg_element001,P_element002,S_element004,Ca_element003]
  conduct = 2
  density = 1
  expand = 3
  formula = G4_BONE_COMPACT_ICRU
  name = G4_BONE_COMPACT_ICRU
  specific = 4
FEATURE [App::DocumentObjectGroupPython] H_element016  label="H_element : 0.034"  # scripted group (container) (typed FeaturePython)
  n = 0.034
FEATURE [App::DocumentObjectGroupPython] C_element016  label="C_element : 0.155"  # scripted group (container) (typed FeaturePython)
  n = 0.155
FEATURE [App::DocumentObjectGroupPython] N_element011  label="N_element : 0.042"  # scripted group (container) (typed FeaturePython)
  n = 0.042
FEATURE [App::DocumentObjectGroupPython] O_element015  label="O_element : 0.435"  # scripted group (container) (typed FeaturePython)
  n = 0.435
FEATURE [App::DocumentObjectGroupPython] Na_element003  label="Na_element : 0.003"  # scripted group (container) (typed FeaturePython)
  n = 0.001
FEATURE [App::DocumentObjectGroupPython] Mg_element002  label="Mg_element : 0.003"  # scripted group (container) (typed FeaturePython)
  n = 0.002
FEATURE [App::DocumentObjectGroupPython] P_element003  label="P_element : 0.103"  # scripted group (container) (typed FeaturePython)
  n = 0.103
FEATURE [App::DocumentObjectGroupPython] S_element005  label="S_element : 0.004"  # scripted group (container) (typed FeaturePython)
  n = 0.003
FEATURE [App::DocumentObjectGroupPython] Ca_element004  label="Ca_element : 0.225"  # scripted group (container) (typed FeaturePython)
  n = 0.225
FEATURE [App::DocumentObjectGroupPython] G4_BONE_CORTICAL_ICRP  # scripted group (container) (typed FeaturePython)
  Dunit = g/cm3
  Dvalue = 1.92
  Group = -> [H_element016,C_element016,N_element011,O_element015,Na_element003,Mg_element002,P_element003,S_element005,Ca_element004]
  conduct = 2
  density = 1
  expand = 3
  formula = G4_BONE_CORTICAL_ICRP
  name = G4_BONE_CORTICAL_ICRP
  specific = 4
FEATURE [App::DocumentObjectGroupPython] B_element001  label="B_element : 4"  # scripted group (container) (typed FeaturePython)
  n = 4
  ref = B_element
FEATURE [App::DocumentObjectGroupPython] C_element017  label="C_element : 1"  # scripted group (container) (typed FeaturePython)
  n = 1
  ref = C_element
FEATURE [App::DocumentObjectGroupPython] G4_BORON_CARBIDE  # scripted group (container) (typed FeaturePython)
  Dunit = g/cm3
  Dvalue = 2.52
  Group = -> [B_element001,C_element017]
  conduct = 2
  density = 1
  expand = 3
  formula = G4_BORON_CARBIDE
  name = G4_BORON_CARBIDE
  specific = 4
FEATURE [App::DocumentObjectGroupPython] B_element002  label="B_element : 2"  # scripted group (container) (typed FeaturePython)
  n = 2
  ref = B_element
FEATURE [App::DocumentObjectGroupPython] O_element016  label="O_element : 006"  # scripted group (container) (typed FeaturePython)
  n = 3
  ref = O_element
FEATURE [App::DocumentObjectGroupPython] G4_BORON_OXIDE  # scripted group (container) (typed FeaturePython)
  Dunit = g/cm3
  Dvalue = 1.812
  Group = -> [B_element002,O_element016]
  conduct = 2
  density = 1
  expand = 3
  formula = G4_BORON_OXIDE
  name = G4_BORON_OXIDE
  specific = 4
FEATURE [App::DocumentObjectGroupPython] H_element017  label="H_element : 0.107"  # scripted group (container) (typed FeaturePython)
  n = 0.107
FEATURE [App::DocumentObjectGroupPython] C_element018  label="C_element : 0.145"  # scripted group (container) (typed FeaturePython)
  n = 0.145
FEATURE [App::DocumentObjectGroupPython] N_element012  label="N_element : 0.022"  # scripted group (container) (typed FeaturePython)
  n = 0.022
FEATURE [App::DocumentObjectGroupPython] O_element017  label="O_element : 0.712"  # scripted group (container) (typed FeaturePython)
  n = 0.712
FEATURE [App::DocumentObjectGroupPython] Na_element004  label="Na_element : 0.004"  # scripted group (container) (typed FeaturePython)
  n = 0.002
FEATURE [App::DocumentObjectGroupPython] P_element004  label="P_element : 0.004"  # scripted group (container) (typed FeaturePython)
  n = 0.004
FEATURE [App::DocumentObjectGroupPython] S_element006  label="S_element : 0.005"  # scripted group (container) (typed FeaturePython)
  n = 0.002
FEATURE [App::DocumentObjectGroupPython] Cl_element003  label="Cl_element : 0.004"  # scripted group (container) (typed FeaturePython)
  n = 0.003
FEATURE [App::DocumentObjectGroupPython] K_element002  label="K_element : 0.003"  # scripted group (container) (typed FeaturePython)
  n = 0.003
FEATURE [App::DocumentObjectGroupPython] G4_BRAIN_ICRP  # scripted group (container) (typed FeaturePython)
  Dunit = g/cm3
  Dvalue = 1.04
  Group = -> [H_element017,C_element018,N_element012,O_element017,Na_element004,P_element004,S_element006,Cl_element003,K_element002]
  conduct = 2
  density = 1
  expand = 3
  formula = G4_BRAIN_ICRP
  name = G4_BRAIN_ICRP
  specific = 4
FEATURE [App::DocumentObjectGroupPython] C_element019  label="C_element : 4"  # scripted group (container) (typed FeaturePython)
  n = 4
  ref = C_element
FEATURE [App::DocumentObjectGroupPython] H_element018  label="H_element : 010"  # scripted group (container) (typed FeaturePython)
  n = 10
  ref = H_element
FEATURE [App::DocumentObjectGroupPython] G4_BUTANE  # scripted group (container) (typed FeaturePython)
  Dunit = g/cm3
  Dvalue = 0.00249343
  Group = -> [C_element019,H_element018]
  conduct = 2
  density = 1
  expand = 3
  formula = G4_BUTANE
  name = G4_BUTANE
  specific = 4
FEATURE [App::DocumentObjectGroupPython] C_element020  label="C_element : 008"  # scripted group (container) (typed FeaturePython)
  n = 4
  ref = C_element
FEATURE [App::DocumentObjectGroupPython] H_element019  label="H_element : 011"  # scripted group (container) (typed FeaturePython)
  n = 10
  ref = H_element
FEATURE [App::DocumentObjectGroupPython] O_element018  label="O_element : 007"  # scripted group (container) (typed FeaturePython)
  n = 1
  ref = O_element
FEATURE [App::DocumentObjectGroupPython] G4_N_BUTYL_ALCOHOL  label="G4_N-BUTYL_ALCOHOL"  # scripted group (container) (typed FeaturePython)
  Dunit = g/cm3
  Dvalue = 0.8098
  Group = -> [C_element020,H_element019,O_element018]
  conduct = 2
  density = 1
  expand = 3
  formula = G4_N-BUTYL_ALCOHOL
  name = G4_N-BUTYL_ALCOHOL
  specific = 4
FEATURE [App::DocumentObjectGroupPython] H_element020  label="H_element : 0.025"  # scripted group (container) (typed FeaturePython)
  n = 0.02468
FEATURE [App::DocumentObjectGroupPython] C_element021  label="C_element : 0.502"  # scripted group (container) (typed FeaturePython)
  n = 0.501611
FEATURE [App::DocumentObjectGroupPython] O_element019  label="O_element : 0.005"  # scripted group (container) (typed FeaturePython)
  n = 0.004527
FEATURE [App::DocumentObjectGroupPython] F_element004  label="F_element : 0.465"  # scripted group (container) (typed FeaturePython)
  n = 0.465209
FEATURE [App::DocumentObjectGroupPython] Si_element001  label="Si_element : 0.004"  # scripted group (container) (typed FeaturePython)
  n = 0.003973
FEATURE [App::DocumentObjectGroupPython] G4_C_552  label="G4_C-552"  # scripted group (container) (typed FeaturePython)
  Dunit = g/cm3
  Dvalue = 1.76
  Group = -> [H_element020,C_element021,O_element019,F_element004,Si_element001]
  conduct = 2
  density = 1
  expand = 3
  formula = G4_C-552
  name = G4_C-552
  specific = 4
FEATURE [App::DocumentObjectGroupPython] Cd_element001  label="Cd_element : 1"  # scripted group (container) (typed FeaturePython)
  n = 1
  ref = Cd_element
FEATURE [App::DocumentObjectGroupPython] Te_element001  label="Te_element : 1"  # scripted group (container) (typed FeaturePython)
  n = 1
  ref = Te_element
FEATURE [App::DocumentObjectGroupPython] G4_CADMIUM_TELLURIDE  # scripted group (container) (typed FeaturePython)
  Dunit = g/cm3
  Dvalue = 6.2
  Group = -> [Cd_element001,Te_element001]
  conduct = 2
  density = 1
  expand = 3
  formula = G4_CADMIUM_TELLURIDE
  name = G4_CADMIUM_TELLURIDE
  specific = 4
FEATURE [App::DocumentObjectGroupPython] Cd_element002  label="Cd_element : 002"  # scripted group (container) (typed FeaturePython)
  n = 1
  ref = Cd_element
FEATURE [App::DocumentObjectGroupPython] W_element001  label="W_element : 1"  # scripted group (container) (typed FeaturePython)
  n = 1
  ref = W_element
FEATURE [App::DocumentObjectGroupPython] O_element020  label="O_element : 008"  # scripted group (container) (typed FeaturePython)
  n = 4
  ref = O_element
FEATURE [App::DocumentObjectGroupPython] G4_CADMIUM_TUNGSTATE  # scripted group (container) (typed FeaturePython)
  Dunit = g/cm3
  Dvalue = 7.9
  Group = -> [Cd_element002,W_element001,O_element020]
  conduct = 2
  density = 1
  expand = 3
  formula = G4_CADMIUM_TUNGSTATE
  name = G4_CADMIUM_TUNGSTATE
  specific = 4
FEATURE [App::DocumentObjectGroupPython] Ca_element005  label="Ca_element : 1"  # scripted group (container) (typed FeaturePython)
  n = 1
  ref = Ca_element
FEATURE [App::DocumentObjectGroupPython] C_element022  label="C_element : 009"  # scripted group (container) (typed FeaturePython)
  n = 1
  ref = C_element
FEATURE [App::DocumentObjectGroupPython] O_element021  label="O_element : 009"  # scripted group (container) (typed FeaturePython)
  n = 3
  ref = O_element
FEATURE [App::DocumentObjectGroupPython] G4_CALCIUM_CARBONATE  # scripted group (container) (typed FeaturePython)
  Dunit = g/cm3
  Dvalue = 2.8
  Group = -> [Ca_element005,C_element022,O_element021]
  conduct = 2
  density = 1
  expand = 3
  formula = G4_CALCIUM_CARBONATE
  name = G4_CALCIUM_CARBONATE
  specific = 4
FEATURE [App::DocumentObjectGroupPython] Ca_element006  label="Ca_element : 002"  # scripted group (container) (typed FeaturePython)
  n = 1
  ref = Ca_element
FEATURE [App::DocumentObjectGroupPython] F_element005  label="F_element : 003"  # scripted group (container) (typed FeaturePython)
  n = 2
  ref = F_element
FEATURE [App::DocumentObjectGroupPython] G4_CALCIUM_FLUORIDE  # scripted group (container) (typed FeaturePython)
  Dunit = g/cm3
  Dvalue = 3.18
  Group = -> [Ca_element006,F_element005]
  conduct = 2
  density = 1
  expand = 3
  formula = G4_CALCIUM_FLUORIDE
  name = G4_CALCIUM_FLUORIDE
  specific = 4
FEATURE [App::DocumentObjectGroupPython] Ca_element007  label="Ca_element : 003"  # scripted group (container) (typed FeaturePython)
  n = 1
  ref = Ca_element
FEATURE [App::DocumentObjectGroupPython] O_element022  label="O_element : 010"  # scripted group (container) (typed FeaturePython)
  n = 1
  ref = O_element
FEATURE [App::DocumentObjectGroupPython] G4_CALCIUM_OXIDE  # scripted group (container) (typed FeaturePython)
  Dunit = g/cm3
  Dvalue = 3.3
  Group = -> [Ca_element007,O_element022]
  conduct = 2
  density = 1
  expand = 3
  formula = G4_CALCIUM_OXIDE
  name = G4_CALCIUM_OXIDE
  specific = 4
FEATURE [App::DocumentObjectGroupPython] Ca_element008  label="Ca_element : 004"  # scripted group (container) (typed FeaturePython)
  n = 1
  ref = Ca_element
FEATURE [App::DocumentObjectGroupPython] S_element007  label="S_element : 002"  # scripted group (container) (typed FeaturePython)
  n = 1
  ref = S_element
FEATURE [App::DocumentObjectGroupPython] O_element023  label="O_element : 011"  # scripted group (container) (typed FeaturePython)
  n = 4
  ref = O_element
FEATURE [App::DocumentObjectGroupPython] G4_CALCIUM_SULFATE  # scripted group (container) (typed FeaturePython)
  Dunit = g/cm3
  Dvalue = 2.96
  Group = -> [Ca_element008,S_element007,O_element023]
  conduct = 2
  density = 1
  expand = 3
  formula = G4_CALCIUM_SULFATE
  name = G4_CALCIUM_SULFATE
  specific = 4
FEATURE [App::DocumentObjectGroupPython] Ca_element009  label="Ca_element : 005"  # scripted group (container) (typed FeaturePython)
  n = 1
  ref = Ca_element
FEATURE [App::DocumentObjectGroupPython] W_element002  label="W_element : 002"  # scripted group (container) (typed FeaturePython)
  n = 1
  ref = W_element
FEATURE [App::DocumentObjectGroupPython] O_element024  label="O_element : 012"  # scripted group (container) (typed FeaturePython)
  n = 4
  ref = O_element
FEATURE [App::DocumentObjectGroupPython] G4_CALCIUM_TUNGSTATE  # scripted group (container) (typed FeaturePython)
  Dunit = g/cm3
  Dvalue = 6.062
  Group = -> [Ca_element009,W_element002,O_element024]
  conduct = 2
  density = 1
  expand = 3
  formula = G4_CALCIUM_TUNGSTATE
  name = G4_CALCIUM_TUNGSTATE
  specific = 4
FEATURE [App::DocumentObjectGroupPython] C_element023  label="C_element : 010"  # scripted group (container) (typed FeaturePython)
  n = 1
  ref = C_element
FEATURE [App::DocumentObjectGroupPython] O_element025  label="O_element : 013"  # scripted group (container) (typed FeaturePython)
  n = 2
  ref = O_element
FEATURE [App::DocumentObjectGroupPython] G4_CARBON_DIOXIDE  # scripted group (container) (typed FeaturePython)
  Dunit = g/cm3
  Dvalue = 0.00184212
  Group = -> [C_element023,O_element025]
  conduct = 2
  density = 1
  expand = 3
  formula = G4_CARBON_DIOXIDE
  name = G4_CARBON_DIOXIDE
  specific = 4
FEATURE [App::DocumentObjectGroupPython] C_element024  label="C_element : 011"  # scripted group (container) (typed FeaturePython)
  n = 1
  ref = C_element
FEATURE [App::DocumentObjectGroupPython] Cl_element004  label="Cl_element : 4"  # scripted group (container) (typed FeaturePython)
  n = 4
  ref = Cl_element
FEATURE [App::DocumentObjectGroupPython] G4_CARBON_TETRACHLORIDE  # scripted group (container) (typed FeaturePython)
  Dunit = g/cm3
  Dvalue = 1.594
  Group = -> [C_element024,Cl_element004]
  conduct = 2
  density = 1
  expand = 3
  formula = G4_CARBON_TETRACHLORIDE
  name = G4_CARBON_TETRACHLORIDE
  specific = 4
FEATURE [App::DocumentObjectGroupPython] C_element025  label="C_element : 012"  # scripted group (container) (typed FeaturePython)
  n = 6
  ref = C_element
FEATURE [App::DocumentObjectGroupPython] H_element021  label="H_element : 012"  # scripted group (container) (typed FeaturePython)
  n = 10
  ref = H_element
FEATURE [App::DocumentObjectGroupPython] O_element026  label="O_element : 5"  # scripted group (container) (typed FeaturePython)
  n = 5
  ref = O_element
FEATURE [App::DocumentObjectGroupPython] G4_CELLULOSE_CELLOPHANE  # scripted group (container) (typed FeaturePython)
  Dunit = g/cm3
  Dvalue = 1.42
  Group = -> [C_element025,H_element021,O_element026]
  conduct = 2
  density = 1
  expand = 3
  formula = G4_CELLULOSE_CELLOPHANE
  name = G4_CELLULOSE_CELLOPHANE
  specific = 4
FEATURE [App::DocumentObjectGroupPython] H_element022  label="H_element : 0.067"  # scripted group (container) (typed FeaturePython)
  n = 0.067125
FEATURE [App::DocumentObjectGroupPython] C_element026  label="C_element : 0.545"  # scripted group (container) (typed FeaturePython)
  n = 0.545403
FEATURE [App::DocumentObjectGroupPython] O_element027  label="O_element : 0.387"  # scripted group (container) (typed FeaturePython)
  n = 0.387472
FEATURE [App::DocumentObjectGroupPython] G4_CELLULOSE_BUTYRATE  # scripted group (container) (typed FeaturePython)
  Dunit = g/cm3
  Dvalue = 1.2
  Group = -> [H_element022,C_element026,O_element027]
  conduct = 2
  density = 1
  expand = 3
  formula = G4_CELLULOSE_BUTYRATE
  name = G4_CELLULOSE_BUTYRATE
  specific = 4
FEATURE [App::DocumentObjectGroupPython] H_element023  label="H_element : 0.029"  # scripted group (container) (typed FeaturePython)
  n = 0.029216
FEATURE [App::DocumentObjectGroupPython] C_element027  label="C_element : 0.271"  # scripted group (container) (typed FeaturePython)
  n = 0.271296
FEATURE [App::DocumentObjectGroupPython] N_element013  label="N_element : 0.121"  # scripted group (container) (typed FeaturePython)
  n = 0.121276
FEATURE [App::DocumentObjectGroupPython] O_element028  label="O_element : 0.578"  # scripted group (container) (typed FeaturePython)
  n = 0.578212
FEATURE [App::DocumentObjectGroupPython] G4_CELLULOSE_NITRATE  # scripted group (container) (typed FeaturePython)
  Dunit = g/cm3
  Dvalue = 1.49
  Group = -> [H_element023,C_element027,N_element013,O_element028]
  conduct = 2
  density = 1
  expand = 3
  formula = G4_CELLULOSE_NITRATE
  name = G4_CELLULOSE_NITRATE
  specific = 4
FEATURE [App::DocumentObjectGroupPython] H_element024  label="H_element : 0.108"  # scripted group (container) (typed FeaturePython)
  n = 0.107596
FEATURE [App::DocumentObjectGroupPython] N_element014  label="N_element : 0.001"  # scripted group (container) (typed FeaturePython)
  n = 0.0008
FEATURE [App::DocumentObjectGroupPython] O_element029  label="O_element : 0.875"  # scripted group (container) (typed FeaturePython)
  n = 0.874976
FEATURE [App::DocumentObjectGroupPython] S_element008  label="S_element : 0.015"  # scripted group (container) (typed FeaturePython)
  n = 0.014627
FEATURE [App::DocumentObjectGroupPython] Ce_element001  label="Ce_element : 0.002"  # scripted group (container) (typed FeaturePython)
  n = 0.002001
FEATURE [App::DocumentObjectGroupPython] G4_CERIC_SULFATE  # scripted group (container) (typed FeaturePython)
  Dunit = g/cm3
  Dvalue = 1.03
  Group = -> [H_element024,N_element014,O_element029,S_element008,Ce_element001]
  conduct = 2
  density = 1
  expand = 3
  formula = G4_CERIC_SULFATE
  name = G4_CERIC_SULFATE
  specific = 4
FEATURE [App::DocumentObjectGroupPython] Cs_element001  label="Cs_element : 1"  # scripted group (container) (typed FeaturePython)
  n = 1
  ref = Cs_element
FEATURE [App::DocumentObjectGroupPython] F_element006  label="F_element : 1"  # scripted group (container) (typed FeaturePython)
  n = 1
  ref = F_element
FEATURE [App::DocumentObjectGroupPython] G4_CESIUM_FLUORIDE  # scripted group (container) (typed FeaturePython)
  Dunit = g/cm3
  Dvalue = 4.115
  Group = -> [Cs_element001,F_element006]
  conduct = 2
  density = 1
  expand = 3
  formula = G4_CESIUM_FLUORIDE
  name = G4_CESIUM_FLUORIDE
  specific = 4
FEATURE [App::DocumentObjectGroupPython] Cs_element002  label="Cs_element : 002"  # scripted group (container) (typed FeaturePython)
  n = 1
  ref = Cs_element
FEATURE [App::DocumentObjectGroupPython] I_element001  label="I_element : 1"  # scripted group (container) (typed FeaturePython)
  n = 1
  ref = I_element
FEATURE [App::DocumentObjectGroupPython] G4_CESIUM_IODIDE  # scripted group (container) (typed FeaturePython)
  Dunit = g/cm3
  Dvalue = 4.51
  Group = -> [Cs_element002,I_element001]
  conduct = 2
  density = 1
  expand = 3
  formula = G4_CESIUM_IODIDE
  name = G4_CESIUM_IODIDE
  specific = 4
FEATURE [App::DocumentObjectGroupPython] C_element028  label="C_element : 013"  # scripted group (container) (typed FeaturePython)
  n = 6
  ref = C_element
FEATURE [App::DocumentObjectGroupPython] H_element025  label="H_element : 013"  # scripted group (container) (typed FeaturePython)
  n = 5
  ref = H_element
FEATURE [App::DocumentObjectGroupPython] Cl_element005  label="Cl_element : 1"  # scripted group (container) (typed FeaturePython)
  n = 1
  ref = Cl_element
FEATURE [App::DocumentObjectGroupPython] G4_CHLOROBENZENE  # scripted group (container) (typed FeaturePython)
  Dunit = g/cm3
  Dvalue = 1.1058
  Group = -> [C_element028,H_element025,Cl_element005]
  conduct = 2
  density = 1
  expand = 3
  formula = G4_CHLOROBENZENE
  name = G4_CHLOROBENZENE
  specific = 4
FEATURE [App::DocumentObjectGroupPython] C_element029  label="C_element : 014"  # scripted group (container) (typed FeaturePython)
  n = 1
  ref = C_element
FEATURE [App::DocumentObjectGroupPython] H_element026  label="H_element : 1"  # scripted group (container) (typed FeaturePython)
  n = 1
  ref = H_element
FEATURE [App::DocumentObjectGroupPython] Cl_element006  label="Cl_element : 3"  # scripted group (container) (typed FeaturePython)
  n = 3
  ref = Cl_element
FEATURE [App::DocumentObjectGroupPython] G4_CHLOROFORM  # scripted group (container) (typed FeaturePython)
  Dunit = g/cm3
  Dvalue = 1.4832
  Group = -> [C_element029,H_element026,Cl_element006]
  conduct = 2
  density = 1
  expand = 3
  formula = G4_CHLOROFORM
  name = G4_CHLOROFORM
  specific = 4
FEATURE [App::DocumentObjectGroupPython] H_element027  label="H_element : 0.010"  # scripted group (container) (typed FeaturePython)
  n = 0.01
FEATURE [App::DocumentObjectGroupPython] C_element030  label="C_element : 0.001"  # scripted group (container) (typed FeaturePython)
  n = 0.001
FEATURE [App::DocumentObjectGroupPython] O_element030  label="O_element : 0.529"  # scripted group (container) (typed FeaturePython)
  n = 0.529107
FEATURE [App::DocumentObjectGroupPython] Na_element005  label="Na_element : 0.016"  # scripted group (container) (typed FeaturePython)
  n = 0.016
FEATURE [App::DocumentObjectGroupPython] Mg_element003  label="Mg_element : 0.004"  # scripted group (container) (typed FeaturePython)
  n = 0.002
FEATURE [App::DocumentObjectGroupPython] Al_element002  label="Al_element : 0.034"  # scripted group (container) (typed FeaturePython)
  n = 0.033872
FEATURE [App::DocumentObjectGroupPython] Si_element002  label="Si_element : 0.337"  # scripted group (container) (typed FeaturePython)
  n = 0.337021
FEATURE [App::DocumentObjectGroupPython] K_element003  label="K_element : 0.013"  # scripted group (container) (typed FeaturePython)
  n = 0.013
FEATURE [App::DocumentObjectGroupPython] Ca_element010  label="Ca_element : 0.044"  # scripted group (container) (typed FeaturePython)
  n = 0.044
FEATURE [App::DocumentObjectGroupPython] Fe_element002  label="Fe_element : 0.014"  # scripted group (container) (typed FeaturePython)
  n = 0.014
FEATURE [App::DocumentObjectGroupPython] G4_CONCRETE  # scripted group (container) (typed FeaturePython)
  Dunit = g/cm3
  Dvalue = 2.3
  Group = -> [H_element027,C_element030,O_element030,Na_element005,Mg_element003,Al_element002,Si_element002,K_element003,Ca_element010,Fe_element002]
  conduct = 2
  density = 1
  expand = 3
  formula = G4_CONCRETE
  name = G4_CONCRETE
  specific = 4
FEATURE [App::DocumentObjectGroupPython] C_element031  label="C_element : 015"  # scripted group (container) (typed FeaturePython)
  n = 6
  ref = C_element
FEATURE [App::DocumentObjectGroupPython] H_element028  label="H_element : 12"  # scripted group (container) (typed FeaturePython)
  n = 12
  ref = H_element
FEATURE [App::DocumentObjectGroupPython] G4_CYCLOHEXANE  # scripted group (container) (typed FeaturePython)
  Dunit = g/cm3
  Dvalue = 0.779
  Group = -> [C_element031,H_element028]
  conduct = 2
  density = 1
  expand = 3
  formula = G4_CYCLOHEXANE
  name = G4_CYCLOHEXANE
  specific = 4
FEATURE [App::DocumentObjectGroupPython] C_element032  label="C_element : 016"  # scripted group (container) (typed FeaturePython)
  n = 6
  ref = C_element
FEATURE [App::DocumentObjectGroupPython] H_element029  label="H_element : 4"  # scripted group (container) (typed FeaturePython)
  n = 4
  ref = H_element
FEATURE [App::DocumentObjectGroupPython] Cl_element007  label="Cl_element : 2"  # scripted group (container) (typed FeaturePython)
  n = 2
  ref = Cl_element
FEATURE [App::DocumentObjectGroupPython] G4_1_2_DICHLOROBENZENE  label="G4_1.2-DICHLOROBENZENE"  # scripted group (container) (typed FeaturePython)
  Dunit = g/cm3
  Dvalue = 1.3048
  Group = -> [C_element032,H_element029,Cl_element007]
  conduct = 2
  density = 1
  expand = 3
  formula = G4_1.2-DICHLOROBENZENE
  name = G4_1.2-DICHLOROBENZENE
  specific = 4
FEATURE [App::DocumentObjectGroupPython] C_element033  label="C_element : 017"  # scripted group (container) (typed FeaturePython)
  n = 4
  ref = C_element
FEATURE [App::DocumentObjectGroupPython] H_element030  label="H_element : 8"  # scripted group (container) (typed FeaturePython)
  n = 8
  ref = H_element
FEATURE [App::DocumentObjectGroupPython] O_element031  label="O_element : 014"  # scripted group (container) (typed FeaturePython)
  n = 1
  ref = O_element
FEATURE [App::DocumentObjectGroupPython] Cl_element008  label="Cl_element : 005"  # scripted group (container) (typed FeaturePython)
  n = 2
  ref = Cl_element
FEATURE [App::DocumentObjectGroupPython] G4_DICHLORODIETHYL_ETHER  # scripted group (container) (typed FeaturePython)
  Dunit = g/cm3
  Dvalue = 1.2199
  Group = -> [C_element033,H_element030,O_element031,Cl_element008]
  conduct = 2
  density = 1
  expand = 3
  formula = G4_DICHLORODIETHYL_ETHER
  name = G4_DICHLORODIETHYL_ETHER
  specific = 4
FEATURE [App::DocumentObjectGroupPython] C_element034  label="C_element : 018"  # scripted group (container) (typed FeaturePython)
  n = 2
  ref = C_element
FEATURE [App::DocumentObjectGroupPython] H_element031  label="H_element : 014"  # scripted group (container) (typed FeaturePython)
  n = 4
  ref = H_element
FEATURE [App::DocumentObjectGroupPython] Cl_element009  label="Cl_element : 006"  # scripted group (container) (typed FeaturePython)
  n = 2
  ref = Cl_element
FEATURE [App::DocumentObjectGroupPython] G4_1_2_DICHLOROETHANE  label="G4_1.2-DICHLOROETHANE"  # scripted group (container) (typed FeaturePython)
  Dunit = g/cm3
  Dvalue = 1.2351
  Group = -> [C_element034,H_element031,Cl_element009]
  conduct = 2
  density = 1
  expand = 3
  formula = G4_1.2-DICHLOROETHANE
  name = G4_1.2-DICHLOROETHANE
  specific = 4
FEATURE [App::DocumentObjectGroupPython] C_element035  label="C_element : 019"  # scripted group (container) (typed FeaturePython)
  n = 4
  ref = C_element
FEATURE [App::DocumentObjectGroupPython] H_element032  label="H_element : 015"  # scripted group (container) (typed FeaturePython)
  n = 10
  ref = H_element
FEATURE [App::DocumentObjectGroupPython] O_element032  label="O_element : 015"  # scripted group (container) (typed FeaturePython)
  n = 1
  ref = O_element
FEATURE [App::DocumentObjectGroupPython] G4_DIETHYL_ETHER  # scripted group (container) (typed FeaturePython)
  Dunit = g/cm3
  Dvalue = 0.71378
  Group = -> [C_element035,H_element032,O_element032]
  conduct = 2
  density = 1
  expand = 3
  formula = G4_DIETHYL_ETHER
  name = G4_DIETHYL_ETHER
  specific = 4
FEATURE [App::DocumentObjectGroupPython] C_element036  label="C_element : 020"  # scripted group (container) (typed FeaturePython)
  n = 3
  ref = C_element
FEATURE [App::DocumentObjectGroupPython] H_element033  label="H_element : 016"  # scripted group (container) (typed FeaturePython)
  n = 7
  ref = H_element
FEATURE [App::DocumentObjectGroupPython] N_element015  label="N_element : 008"  # scripted group (container) (typed FeaturePython)
  n = 1
  ref = N_element
FEATURE [App::DocumentObjectGroupPython] O_element033  label="O_element : 016"  # scripted group (container) (typed FeaturePython)
  n = 1
  ref = O_element
FEATURE [App::DocumentObjectGroupPython] G4_N_N_DIMETHYL_FORMAMIDE  label="G4_N.N-DIMETHYL_FORMAMIDE"  # scripted group (container) (typed FeaturePython)
  Dunit = g/cm3
  Dvalue = 0.9487
  Group = -> [C_element036,H_element033,N_element015,O_element033]
  conduct = 2
  density = 1
  expand = 3
  formula = G4_N.N-DIMETHYL_FORMAMIDE
  name = G4_N.N-DIMETHYL_FORMAMIDE
  specific = 4
FEATURE [App::DocumentObjectGroupPython] C_element037  label="C_element : 021"  # scripted group (container) (typed FeaturePython)
  n = 2
  ref = C_element
FEATURE [App::DocumentObjectGroupPython] H_element034  label="H_element : 017"  # scripted group (container) (typed FeaturePython)
  n = 6
  ref = H_element
FEATURE [App::DocumentObjectGroupPython] O_element034  label="O_element : 017"  # scripted group (container) (typed FeaturePython)
  n = 1
  ref = O_element
FEATURE [App::DocumentObjectGroupPython] S_element009  label="S_element : 003"  # scripted group (container) (typed FeaturePython)
  n = 1
  ref = S_element
FEATURE [App::DocumentObjectGroupPython] G4_DIMETHYL_SULFOXIDE  # scripted group (container) (typed FeaturePython)
  Dunit = g/cm3
  Dvalue = 1.1014
  Group = -> [C_element037,H_element034,O_element034,S_element009]
  conduct = 2
  density = 1
  expand = 3
  formula = G4_DIMETHYL_SULFOXIDE
  name = G4_DIMETHYL_SULFOXIDE
  specific = 4
FEATURE [App::DocumentObjectGroupPython] C_element038  label="C_element : 022"  # scripted group (container) (typed FeaturePython)
  n = 2
  ref = C_element
FEATURE [App::DocumentObjectGroupPython] H_element035  label="H_element : 018"  # scripted group (container) (typed FeaturePython)
  n = 6
  ref = H_element
FEATURE [App::DocumentObjectGroupPython] G4_ETHANE  # scripted group (container) (typed FeaturePython)
  Dunit = g/cm3
  Dvalue = 0.00125324
  Group = -> [C_element038,H_element035]
  conduct = 2
  density = 1
  expand = 3
  formula = G4_ETHANE
  name = G4_ETHANE
  specific = 4
FEATURE [App::DocumentObjectGroupPython] C_element039  label="C_element : 023"  # scripted group (container) (typed FeaturePython)
  n = 2
  ref = C_element
FEATURE [App::DocumentObjectGroupPython] H_element036  label="H_element : 019"  # scripted group (container) (typed FeaturePython)
  n = 6
  ref = H_element
FEATURE [App::DocumentObjectGroupPython] O_element035  label="O_element : 018"  # scripted group (container) (typed FeaturePython)
  n = 1
  ref = O_element
FEATURE [App::DocumentObjectGroupPython] G4_ETHYL_ALCOHOL  # scripted group (container) (typed FeaturePython)
  Dunit = g/cm3
  Dvalue = 0.7893
  Group = -> [C_element039,H_element036,O_element035]
  conduct = 2
  density = 1
  expand = 3
  formula = G4_ETHYL_ALCOHOL
  name = G4_ETHYL_ALCOHOL
  specific = 4
FEATURE [App::DocumentObjectGroupPython] H_element037  label="H_element : 0.090"  # scripted group (container) (typed FeaturePython)
  n = 0.090027
FEATURE [App::DocumentObjectGroupPython] C_element040  label="C_element : 0.585"  # scripted group (container) (typed FeaturePython)
  n = 0.585182
FEATURE [App::DocumentObjectGroupPython] O_element036  label="O_element : 0.325"  # scripted group (container) (typed FeaturePython)
  n = 0.324791
FEATURE [App::DocumentObjectGroupPython] G4_ETHYL_CELLULOSE  # scripted group (container) (typed FeaturePython)
  Dunit = g/cm3
  Dvalue = 1.13
  Group = -> [H_element037,C_element040,O_element036]
  conduct = 2
  density = 1
  expand = 3
  formula = G4_ETHYL_CELLULOSE
  name = G4_ETHYL_CELLULOSE
  specific = 4
FEATURE [App::DocumentObjectGroupPython] C_element041  label="C_element : 024"  # scripted group (container) (typed FeaturePython)
  n = 2
  ref = C_element
FEATURE [App::DocumentObjectGroupPython] H_element038  label="H_element : 020"  # scripted group (container) (typed FeaturePython)
  n = 4
  ref = H_element
FEATURE [App::DocumentObjectGroupPython] G4_ETHYLENE  # scripted group (container) (typed FeaturePython)
  Dunit = g/cm3
  Dvalue = 0.00117497
  Group = -> [C_element041,H_element038]
  conduct = 2
  density = 1
  expand = 3
  formula = G4_ETHYLENE
  name = G4_ETHYLENE
  specific = 4
FEATURE [App::DocumentObjectGroupPython] H_element039  label="H_element : 0.096"  # scripted group (container) (typed FeaturePython)
  n = 0.096
FEATURE [App::DocumentObjectGroupPython] C_element042  label="C_element : 0.195"  # scripted group (container) (typed FeaturePython)
  n = 0.195
FEATURE [App::DocumentObjectGroupPython] N_element016  label="N_element : 0.057"  # scripted group (container) (typed FeaturePython)
  n = 0.057
FEATURE [App::DocumentObjectGroupPython] O_element037  label="O_element : 0.646"  # scripted group (container) (typed FeaturePython)
  n = 0.646
FEATURE [App::DocumentObjectGroupPython] Na_element006  label="Na_element : 0.017"  # scripted group (container) (typed FeaturePython)
  n = 0.001
FEATURE [App::DocumentObjectGroupPython] P_element005  label="P_element : 0.104"  # scripted group (container) (typed FeaturePython)
  n = 0.001
FEATURE [App::DocumentObjectGroupPython] S_element010  label="S_element : 0.016"  # scripted group (container) (typed FeaturePython)
  n = 0.003
FEATURE [App::DocumentObjectGroupPython] Cl_element010  label="Cl_element : 0.005"  # scripted group (container) (typed FeaturePython)
  n = 0.001
FEATURE [App::DocumentObjectGroupPython] G4_EYE_LENS_ICRP  # scripted group (container) (typed FeaturePython)
  Dunit = g/cm3
  Dvalue = 1.07
  Group = -> [H_element039,C_element042,N_element016,O_element037,Na_element006,P_element005,S_element010,Cl_element010]
  conduct = 2
  density = 1
  expand = 3
  formula = G4_EYE_LENS_ICRP
  name = G4_EYE_LENS_ICRP
  specific = 4
FEATURE [App::DocumentObjectGroupPython] Fe_element003  label="Fe_element : 2"  # scripted group (container) (typed FeaturePython)
  n = 2
  ref = Fe_element
FEATURE [App::DocumentObjectGroupPython] O_element038  label="O_element : 019"  # scripted group (container) (typed FeaturePython)
  n = 3
  ref = O_element
FEATURE [App::DocumentObjectGroupPython] G4_FERRIC_OXIDE  # scripted group (container) (typed FeaturePython)
  Dunit = g/cm3
  Dvalue = 5.2
  Group = -> [Fe_element003,O_element038]
  conduct = 2
  density = 1
  expand = 3
  formula = G4_FERRIC_OXIDE
  name = G4_FERRIC_OXIDE
  specific = 4
FEATURE [App::DocumentObjectGroupPython] Fe_element004  label="Fe_element : 1"  # scripted group (container) (typed FeaturePython)
  n = 1
  ref = Fe_element
FEATURE [App::DocumentObjectGroupPython] B_element003  label="B_element : 1"  # scripted group (container) (typed FeaturePython)
  n = 1
  ref = B_element
FEATURE [App::DocumentObjectGroupPython] G4_FERROBORIDE  # scripted group (container) (typed FeaturePython)
  Dunit = g/cm3
  Dvalue = 7.15
  Group = -> [Fe_element004,B_element003]
  conduct = 2
  density = 1
  expand = 3
  formula = G4_FERROBORIDE
  name = G4_FERROBORIDE
  specific = 4
FEATURE [App::DocumentObjectGroupPython] Fe_element005  label="Fe_element : 003"  # scripted group (container) (typed FeaturePython)
  n = 1
  ref = Fe_element
FEATURE [App::DocumentObjectGroupPython] O_element039  label="O_element : 020"  # scripted group (container) (typed FeaturePython)
  n = 1
  ref = O_element
FEATURE [App::DocumentObjectGroupPython] G4_FERROUS_OXIDE  # scripted group (container) (typed FeaturePython)
  Dunit = g/cm3
  Dvalue = 5.7
  Group = -> [Fe_element005,O_element039]
  conduct = 2
  density = 1
  expand = 3
  formula = G4_FERROUS_OXIDE
  name = G4_FERROUS_OXIDE
  specific = 4
FEATURE [App::DocumentObjectGroupPython] H_element040  label="H_element : 0.115"  # scripted group (container) (typed FeaturePython)
  n = 0.108259
FEATURE [App::DocumentObjectGroupPython] N_element017  label="N_element : 0.000"  # scripted group (container) (typed FeaturePython)
  n = 2.7e-05
FEATURE [App::DocumentObjectGroupPython] O_element040  label="O_element : 0.879"  # scripted group (container) (typed FeaturePython)
  n = 0.878636
FEATURE [App::DocumentObjectGroupPython] Na_element007  label="Na_element : 0.000"  # scripted group (container) (typed FeaturePython)
  n = 2.2e-05
FEATURE [App::DocumentObjectGroupPython] S_element011  label="S_element : 0.013"  # scripted group (container) (typed FeaturePython)
  n = 0.012968
FEATURE [App::DocumentObjectGroupPython] Cl_element011  label="Cl_element : 0.000"  # scripted group (container) (typed FeaturePython)
  n = 3.4e-05
FEATURE [App::DocumentObjectGroupPython] Fe_element006  label="Fe_element : 0.000"  # scripted group (container) (typed FeaturePython)
  n = 5.4e-05
FEATURE [App::DocumentObjectGroupPython] G4_FERROUS_SULFATE  # scripted group (container) (typed FeaturePython)
  Dunit = g/cm3
  Dvalue = 1.024
  Group = -> [H_element040,N_element017,O_element040,Na_element007,S_element011,Cl_element011,Fe_element006]
  conduct = 2
  density = 1
  expand = 3
  formula = G4_FERROUS_SULFATE
  name = G4_FERROUS_SULFATE
  specific = 4
FEATURE [App::DocumentObjectGroupPython] C_element043  label="C_element : 0.099"  # scripted group (container) (typed FeaturePython)
  n = 0.099335
FEATURE [App::DocumentObjectGroupPython] F_element007  label="F_element : 0.314"  # scripted group (container) (typed FeaturePython)
  n = 0.314247
FEATURE [App::DocumentObjectGroupPython] Cl_element012  label="Cl_element : 0.586"  # scripted group (container) (typed FeaturePython)
  n = 0.586418
FEATURE [App::DocumentObjectGroupPython] G4_FREON_12  label="G4_FREON-12"  # scripted group (container) (typed FeaturePython)
  Dunit = g/cm3
  Dvalue = 1.12
  Group = -> [C_element043,F_element007,Cl_element012]
  conduct = 2
  density = 1
  expand = 3
  formula = G4_FREON-12
  name = G4_FREON-12
  specific = 4
FEATURE [App::DocumentObjectGroupPython] C_element044  label="C_element : 0.057"  # scripted group (container) (typed FeaturePython)
  n = 0.057245
FEATURE [App::DocumentObjectGroupPython] F_element008  label="F_element : 0.181"  # scripted group (container) (typed FeaturePython)
  n = 0.181096
FEATURE [App::DocumentObjectGroupPython] Br_element001  label="Br_element : 0.762"  # scripted group (container) (typed FeaturePython)
  n = 0.761659
FEATURE [App::DocumentObjectGroupPython] G4_FREON_12B2  label="G4_FREON-12B2"  # scripted group (container) (typed FeaturePython)
  Dunit = g/cm3
  Dvalue = 1.8
  Group = -> [C_element044,F_element008,Br_element001]
  conduct = 2
  density = 1
  expand = 3
  formula = G4_FREON-12B2
  name = G4_FREON-12B2
  specific = 4
FEATURE [App::DocumentObjectGroupPython] C_element045  label="C_element : 0.115"  # scripted group (container) (typed FeaturePython)
  n = 0.114983
FEATURE [App::DocumentObjectGroupPython] F_element009  label="F_element : 0.546"  # scripted group (container) (typed FeaturePython)
  n = 0.545621
FEATURE [App::DocumentObjectGroupPython] Cl_element013  label="Cl_element : 0.339"  # scripted group (container) (typed FeaturePython)
  n = 0.339396
FEATURE [App::DocumentObjectGroupPython] G4_FREON_13  label="G4_FREON-13"  # scripted group (container) (typed FeaturePython)
  Dunit = g/cm3
  Dvalue = 0.95
  Group = -> [C_element045,F_element009,Cl_element013]
  conduct = 2
  density = 1
  expand = 3
  formula = G4_FREON-13
  name = G4_FREON-13
  specific = 4
FEATURE [App::DocumentObjectGroupPython] C_element046  label="C_element : 025"  # scripted group (container) (typed FeaturePython)
  n = 1
  ref = C_element
FEATURE [App::DocumentObjectGroupPython] F_element010  label="F_element : 3"  # scripted group (container) (typed FeaturePython)
  n = 3
  ref = F_element
FEATURE [App::DocumentObjectGroupPython] Br_element002  label="Br_element : 1"  # scripted group (container) (typed FeaturePython)
  n = 1
  ref = Br_element
FEATURE [App::DocumentObjectGroupPython] G4_FREON_13B1  label="G4_FREON-13B1"  # scripted group (container) (typed FeaturePython)
  Dunit = g/cm3
  Dvalue = 1.5
  Group = -> [C_element046,F_element010,Br_element002]
  conduct = 2
  density = 1
  expand = 3
  formula = G4_FREON-13B1
  name = G4_FREON-13B1
  specific = 4
FEATURE [App::DocumentObjectGroupPython] C_element047  label="C_element : 0.061"  # scripted group (container) (typed FeaturePython)
  n = 0.061309
FEATURE [App::DocumentObjectGroupPython] F_element011  label="F_element : 0.291"  # scripted group (container) (typed FeaturePython)
  n = 0.290924
FEATURE [App::DocumentObjectGroupPython] I_element002  label="I_element : 0.648"  # scripted group (container) (typed FeaturePython)
  n = 0.647767
FEATURE [App::DocumentObjectGroupPython] G4_FREON_13I1  label="G4_FREON-13I1"  # scripted group (container) (typed FeaturePython)
  Dunit = g/cm3
  Dvalue = 1.8
  Group = -> [C_element047,F_element011,I_element002]
  conduct = 2
  density = 1
  expand = 3
  formula = G4_FREON-13I1
  name = G4_FREON-13I1
  specific = 4
FEATURE [App::DocumentObjectGroupPython] Gd_element001  label="Gd_element : 2"  # scripted group (container) (typed FeaturePython)
  n = 2
  ref = Gd_element
FEATURE [App::DocumentObjectGroupPython] O_element041  label="O_element : 021"  # scripted group (container) (typed FeaturePython)
  n = 2
  ref = O_element
FEATURE [App::DocumentObjectGroupPython] S_element012  label="S_element : 004"  # scripted group (container) (typed FeaturePython)
  n = 1
  ref = S_element
FEATURE [App::DocumentObjectGroupPython] G4_GADOLINIUM_OXYSULFIDE  # scripted group (container) (typed FeaturePython)
  Dunit = g/cm3
  Dvalue = 7.44
  Group = -> [Gd_element001,O_element041,S_element012]
  conduct = 2
  density = 1
  expand = 3
  formula = G4_GADOLINIUM_OXYSULFIDE
  name = G4_GADOLINIUM_OXYSULFIDE
  specific = 4
FEATURE [App::DocumentObjectGroupPython] Ga_element001  label="Ga_element : 1"  # scripted group (container) (typed FeaturePython)
  n = 1
  ref = Ga_element
FEATURE [App::DocumentObjectGroupPython] As_element001  label="As_element : 1"  # scripted group (container) (typed FeaturePython)
  n = 1
  ref = As_element
FEATURE [App::DocumentObjectGroupPython] G4_GALLIUM_ARSENIDE  # scripted group (container) (typed FeaturePython)
  Dunit = g/cm3
  Dvalue = 5.31
  Group = -> [Ga_element001,As_element001]
  conduct = 2
  density = 1
  expand = 3
  formula = G4_GALLIUM_ARSENIDE
  name = G4_GALLIUM_ARSENIDE
  specific = 4
FEATURE [App::DocumentObjectGroupPython] H_element041  label="H_element : 0.081"  # scripted group (container) (typed FeaturePython)
  n = 0.08118
FEATURE [App::DocumentObjectGroupPython] C_element048  label="C_element : 0.416"  # scripted group (container) (typed FeaturePython)
  n = 0.41606
FEATURE [App::DocumentObjectGroupPython] N_element018  label="N_element : 0.111"  # scripted group (container) (typed FeaturePython)
  n = 0.11124
FEATURE [App::DocumentObjectGroupPython] O_element042  label="O_element : 0.381"  # scripted group (container) (typed FeaturePython)
  n = 0.38064
FEATURE [App::DocumentObjectGroupPython] S_element013  label="S_element : 0.011"  # scripted group (container) (typed FeaturePython)
  n = 0.01088
FEATURE [App::DocumentObjectGroupPython] G4_GEL_PHOTO_EMULSION  # scripted group (container) (typed FeaturePython)
  Dunit = g/cm3
  Dvalue = 1.2914
  Group = -> [H_element041,C_element048,N_element018,O_element042,S_element013]
  conduct = 2
  density = 1
  expand = 3
  formula = G4_GEL_PHOTO_EMULSION
  name = G4_GEL_PHOTO_EMULSION
  specific = 4
FEATURE [App::DocumentObjectGroupPython] B_element004  label="B_element : 0.040"  # scripted group (container) (typed FeaturePython)
  n = 0.0400639
FEATURE [App::DocumentObjectGroupPython] O_element043  label="O_element : 0.540"  # scripted group (container) (typed FeaturePython)
  n = 0.539561
FEATURE [App::DocumentObjectGroupPython] Na_element008  label="Na_element : 0.028"  # scripted group (container) (typed FeaturePython)
  n = 0.0281909
FEATURE [App::DocumentObjectGroupPython] Al_element003  label="Al_element : 0.012"  # scripted group (container) (typed FeaturePython)
  n = 0.011644
FEATURE [App::DocumentObjectGroupPython] Si_element003  label="Si_element : 0.377"  # scripted group (container) (typed FeaturePython)
  n = 0.377219
FEATURE [App::DocumentObjectGroupPython] K_element004  label="K_element : 0.014"  # scripted group (container) (typed FeaturePython)
  n = 0.00332099
FEATURE [App::DocumentObjectGroupPython] G4_Pyrex_Glass  # scripted group (container) (typed FeaturePython)
  Dunit = g/cm3
  Dvalue = 2.23
  Group = -> [B_element004,O_element043,Na_element008,Al_element003,Si_element003,K_element004]
  conduct = 2
  density = 1
  expand = 3
  formula = G4_Pyrex_Glass
  name = G4_Pyrex_Glass
  specific = 4
FEATURE [App::DocumentObjectGroupPython] O_element044  label="O_element : 0.156"  # scripted group (container) (typed FeaturePython)
  n = 0.156453
FEATURE [App::DocumentObjectGroupPython] Si_element004  label="Si_element : 0.081"  # scripted group (container) (typed FeaturePython)
  n = 0.080866
FEATURE [App::DocumentObjectGroupPython] Ti_element001  label="Ti_element : 0.008"  # scripted group (container) (typed FeaturePython)
  n = 0.008092
FEATURE [App::DocumentObjectGroupPython] As_element002  label="As_element : 0.003"  # scripted group (container) (typed FeaturePython)
  n = 0.002651
FEATURE [App::DocumentObjectGroupPython] Pb_element001  label="Pb_element : 0.752"  # scripted group (container) (typed FeaturePython)
  n = 0.751938
FEATURE [App::DocumentObjectGroupPython] G4_GLASS_LEAD  # scripted group (container) (typed FeaturePython)
  Dunit = g/cm3
  Dvalue = 6.22
  Group = -> [O_element044,Si_element004,Ti_element001,As_element002,Pb_element001]
  conduct = 2
  density = 1
  expand = 3
  formula = G4_GLASS_LEAD
  name = G4_GLASS_LEAD
  specific = 4
FEATURE [App::DocumentObjectGroupPython] O_element045  label="O_element : 0.460"  # scripted group (container) (typed FeaturePython)
  n = 0.4598
FEATURE [App::DocumentObjectGroupPython] Na_element009  label="Na_element : 0.096"  # scripted group (container) (typed FeaturePython)
  n = 0.0964411
FEATURE [App::DocumentObjectGroupPython] Si_element005  label="Si_element : 0.378"  # scripted group (container) (typed FeaturePython)
  n = 0.336553
FEATURE [App::DocumentObjectGroupPython] Ca_element011  label="Ca_element : 0.107"  # scripted group (container) (typed FeaturePython)
  n = 0.107205
FEATURE [App::DocumentObjectGroupPython] G4_GLASS_PLATE  # scripted group (container) (typed FeaturePython)
  Dunit = g/cm3
  Dvalue = 2.4
  Group = -> [O_element045,Na_element009,Si_element005,Ca_element011]
  conduct = 2
  density = 1
  expand = 3
  formula = G4_GLASS_PLATE
  name = G4_GLASS_PLATE
  specific = 4
FEATURE [App::DocumentObjectGroupPython] C_element049  label="C_element : 026"  # scripted group (container) (typed FeaturePython)
  n = 5
  ref = C_element
FEATURE [App::DocumentObjectGroupPython] H_element042  label="H_element : 021"  # scripted group (container) (typed FeaturePython)
  n = 10
  ref = H_element
FEATURE [App::DocumentObjectGroupPython] N_element019  label="N_element : 2"  # scripted group (container) (typed FeaturePython)
  n = 2
  ref = N_element
FEATURE [App::DocumentObjectGroupPython] O_element046  label="O_element : 022"  # scripted group (container) (typed FeaturePython)
  n = 3
  ref = O_element
FEATURE [App::DocumentObjectGroupPython] G4_GLUTAMINE  # scripted group (container) (typed FeaturePython)
  Dunit = g/cm3
  Dvalue = 1.46
  Group = -> [C_element049,H_element042,N_element019,O_element046]
  conduct = 2
  density = 1
  expand = 3
  formula = G4_GLUTAMINE
  name = G4_GLUTAMINE
  specific = 4
FEATURE [App::DocumentObjectGroupPython] C_element050  label="C_element : 027"  # scripted group (container) (typed FeaturePython)
  n = 3
  ref = C_element
FEATURE [App::DocumentObjectGroupPython] H_element043  label="H_element : 022"  # scripted group (container) (typed FeaturePython)
  n = 8
  ref = H_element
FEATURE [App::DocumentObjectGroupPython] O_element047  label="O_element : 023"  # scripted group (container) (typed FeaturePython)
  n = 3
  ref = O_element
FEATURE [App::DocumentObjectGroupPython] G4_GLYCEROL  # scripted group (container) (typed FeaturePython)
  Dunit = g/cm3
  Dvalue = 1.2613
  Group = -> [C_element050,H_element043,O_element047]
  conduct = 2
  density = 1
  expand = 3
  formula = G4_GLYCEROL
  name = G4_GLYCEROL
  specific = 4
FEATURE [App::DocumentObjectGroupPython] C_element051  label="C_element : 028"  # scripted group (container) (typed FeaturePython)
  n = 5
  ref = C_element
FEATURE [App::DocumentObjectGroupPython] H_element044  label="H_element : 023"  # scripted group (container) (typed FeaturePython)
  n = 5
  ref = H_element
FEATURE [App::DocumentObjectGroupPython] N_element020  label="N_element : 009"  # scripted group (container) (typed FeaturePython)
  n = 5
  ref = N_element
FEATURE [App::DocumentObjectGroupPython] O_element048  label="O_element : 024"  # scripted group (container) (typed FeaturePython)
  n = 1
  ref = O_element
FEATURE [App::DocumentObjectGroupPython] G4_GUANINE  # scripted group (container) (typed FeaturePython)
  Dunit = g/cm3
  Dvalue = 2.2
  Group = -> [C_element051,H_element044,N_element020,O_element048]
  conduct = 2
  density = 1
  expand = 3
  formula = G4_GUANINE
  name = G4_GUANINE
  specific = 4
FEATURE [App::DocumentObjectGroupPython] Ca_element012  label="Ca_element : 006"  # scripted group (container) (typed FeaturePython)
  n = 1
  ref = Ca_element
FEATURE [App::DocumentObjectGroupPython] S_element014  label="S_element : 005"  # scripted group (container) (typed FeaturePython)
  n = 1
  ref = S_element
FEATURE [App::DocumentObjectGroupPython] O_element049  label="O_element : 6"  # scripted group (container) (typed FeaturePython)
  n = 6
  ref = O_element
FEATURE [App::DocumentObjectGroupPython] H_element045  label="H_element : 024"  # scripted group (container) (typed FeaturePython)
  n = 4
  ref = H_element
FEATURE [App::DocumentObjectGroupPython] G4_GYPSUM  # scripted group (container) (typed FeaturePython)
  Dunit = g/cm3
  Dvalue = 2.32
  Group = -> [Ca_element012,S_element014,O_element049,H_element045]
  conduct = 2
  density = 1
  expand = 3
  formula = G4_GYPSUM
  name = G4_GYPSUM
  specific = 4
FEATURE [App::DocumentObjectGroupPython] C_element052  label="C_element : 7"  # scripted group (container) (typed FeaturePython)
  n = 7
  ref = C_element
FEATURE [App::DocumentObjectGroupPython] H_element046  label="H_element : 16"  # scripted group (container) (typed FeaturePython)
  n = 16
  ref = H_element
FEATURE [App::DocumentObjectGroupPython] G4_N_HEPTANE  label="G4_N-HEPTANE"  # scripted group (container) (typed FeaturePython)
  Dunit = g/cm3
  Dvalue = 0.68376
  Group = -> [C_element052,H_element046]
  conduct = 2
  density = 1
  expand = 3
  formula = G4_N-HEPTANE
  name = G4_N-HEPTANE
  specific = 4
FEATURE [App::DocumentObjectGroupPython] C_element053  label="C_element : 029"  # scripted group (container) (typed FeaturePython)
  n = 6
  ref = C_element
FEATURE [App::DocumentObjectGroupPython] H_element047  label="H_element : 14"  # scripted group (container) (typed FeaturePython)
  n = 14
  ref = H_element
FEATURE [App::DocumentObjectGroupPython] G4_N_HEXANE  label="G4_N-HEXANE"  # scripted group (container) (typed FeaturePython)
  Dunit = g/cm3
  Dvalue = 0.6603
  Group = -> [C_element053,H_element047]
  conduct = 2
  density = 1
  expand = 3
  formula = G4_N-HEXANE
  name = G4_N-HEXANE
  specific = 4
FEATURE [App::DocumentObjectGroupPython] C_element054  label="C_element : 22"  # scripted group (container) (typed FeaturePython)
  n = 22
  ref = C_element
FEATURE [App::DocumentObjectGroupPython] H_element048  label="H_element : 025"  # scripted group (container) (typed FeaturePython)
  n = 10
  ref = H_element
FEATURE [App::DocumentObjectGroupPython] N_element021  label="N_element : 010"  # scripted group (container) (typed FeaturePython)
  n = 2
  ref = N_element
FEATURE [App::DocumentObjectGroupPython] O_element050  label="O_element : 025"  # scripted group (container) (typed FeaturePython)
  n = 5
  ref = O_element
FEATURE [App::DocumentObjectGroupPython] G4_KAPTON  # scripted group (container) (typed FeaturePython)
  Dunit = g/cm3
  Dvalue = 1.42
  Group = -> [C_element054,H_element048,N_element021,O_element050]
  conduct = 2
  density = 1
  expand = 3
  formula = G4_KAPTON
  name = G4_KAPTON
  specific = 4
FEATURE [App::DocumentObjectGroupPython] La_element001  label="La_element : 1"  # scripted group (container) (typed FeaturePython)
  n = 1
  ref = La_element
FEATURE [App::DocumentObjectGroupPython] Br_element003  label="Br_element : 002"  # scripted group (container) (typed FeaturePython)
  n = 1
  ref = Br_element
FEATURE [App::DocumentObjectGroupPython] O_element051  label="O_element : 026"  # scripted group (container) (typed FeaturePython)
  n = 1
  ref = O_element
FEATURE [App::DocumentObjectGroupPython] G4_LANTHANUM_OXYBROMIDE  # scripted group (container) (typed FeaturePython)
  Dunit = g/cm3
  Dvalue = 6.28
  Group = -> [La_element001,Br_element003,O_element051]
  conduct = 2
  density = 1
  expand = 3
  formula = G4_LANTHANUM_OXYBROMIDE
  name = G4_LANTHANUM_OXYBROMIDE
  specific = 4
FEATURE [App::DocumentObjectGroupPython] La_element002  label="La_element : 2"  # scripted group (container) (typed FeaturePython)
  n = 2
  ref = La_element
FEATURE [App::DocumentObjectGroupPython] O_element052  label="O_element : 027"  # scripted group (container) (typed FeaturePython)
  n = 2
  ref = O_element
FEATURE [App::DocumentObjectGroupPython] S_element015  label="S_element : 006"  # scripted group (container) (typed FeaturePython)
  n = 1
  ref = S_element
FEATURE [App::DocumentObjectGroupPython] G4_LANTHANUM_OXYSULFIDE  # scripted group (container) (typed FeaturePython)
  Dunit = g/cm3
  Dvalue = 5.86
  Group = -> [La_element002,O_element052,S_element015]
  conduct = 2
  density = 1
  expand = 3
  formula = G4_LANTHANUM_OXYSULFIDE
  name = G4_LANTHANUM_OXYSULFIDE
  specific = 4
FEATURE [App::DocumentObjectGroupPython] O_element053  label="O_element : 0.072"  # scripted group (container) (typed FeaturePython)
  n = 0.071682
FEATURE [App::DocumentObjectGroupPython] Pb_element002  label="Pb_element : 0.928"  # scripted group (container) (typed FeaturePython)
  n = 0.928318
FEATURE [App::DocumentObjectGroupPython] G4_LEAD_OXIDE  # scripted group (container) (typed FeaturePython)
  Dunit = g/cm3
  Dvalue = 9.53
  Group = -> [O_element053,Pb_element002]
  conduct = 2
  density = 1
  expand = 3
  formula = G4_LEAD_OXIDE
  name = G4_LEAD_OXIDE
  specific = 4
FEATURE [App::DocumentObjectGroupPython] Li_element001  label="Li_element : 1"  # scripted group (container) (typed FeaturePython)
  n = 1
  ref = Li_element
FEATURE [App::DocumentObjectGroupPython] N_element022  label="N_element : 011"  # scripted group (container) (typed FeaturePython)
  n = 1
  ref = N_element
FEATURE [App::DocumentObjectGroupPython] H_element049  label="H_element : 026"  # scripted group (container) (typed FeaturePython)
  n = 2
  ref = H_element
FEATURE [App::DocumentObjectGroupPython] G4_LITHIUM_AMIDE  # scripted group (container) (typed FeaturePython)
  Dunit = g/cm3
  Dvalue = 1.178
  Group = -> [Li_element001,N_element022,H_element049]
  conduct = 2
  density = 1
  expand = 3
  formula = G4_LITHIUM_AMIDE
  name = G4_LITHIUM_AMIDE
  specific = 4
FEATURE [App::DocumentObjectGroupPython] Li_element002  label="Li_element : 2"  # scripted group (container) (typed FeaturePython)
  n = 2
  ref = Li_element
FEATURE [App::DocumentObjectGroupPython] C_element055  label="C_element : 030"  # scripted group (container) (typed FeaturePython)
  n = 1
  ref = C_element
FEATURE [App::DocumentObjectGroupPython] O_element054  label="O_element : 028"  # scripted group (container) (typed FeaturePython)
  n = 3
  ref = O_element
FEATURE [App::DocumentObjectGroupPython] G4_LITHIUM_CARBONATE  # scripted group (container) (typed FeaturePython)
  Dunit = g/cm3
  Dvalue = 2.11
  Group = -> [Li_element002,C_element055,O_element054]
  conduct = 2
  density = 1
  expand = 3
  formula = G4_LITHIUM_CARBONATE
  name = G4_LITHIUM_CARBONATE
  specific = 4
FEATURE [App::DocumentObjectGroupPython] Li_element003  label="Li_element : 003"  # scripted group (container) (typed FeaturePython)
  n = 1
  ref = Li_element
FEATURE [App::DocumentObjectGroupPython] F_element012  label="F_element : 004"  # scripted group (container) (typed FeaturePython)
  n = 1
  ref = F_element
FEATURE [App::DocumentObjectGroupPython] G4_LITHIUM_FLUORIDE  # scripted group (container) (typed FeaturePython)
  Dunit = g/cm3
  Dvalue = 2.635
  Group = -> [Li_element003,F_element012]
  conduct = 2
  density = 1
  expand = 3
  formula = G4_LITHIUM_FLUORIDE
  name = G4_LITHIUM_FLUORIDE
  specific = 4
FEATURE [App::DocumentObjectGroupPython] Li_element004  label="Li_element : 004"  # scripted group (container) (typed FeaturePython)
  n = 1
  ref = Li_element
FEATURE [App::DocumentObjectGroupPython] H_element050  label="H_element : 027"  # scripted group (container) (typed FeaturePython)
  n = 1
  ref = H_element
FEATURE [App::DocumentObjectGroupPython] G4_LITHIUM_HYDRIDE  # scripted group (container) (typed FeaturePython)
  Dunit = g/cm3
  Dvalue = 0.82
  Group = -> [Li_element004,H_element050]
  conduct = 2
  density = 1
  expand = 3
  formula = G4_LITHIUM_HYDRIDE
  name = G4_LITHIUM_HYDRIDE
  specific = 4
FEATURE [App::DocumentObjectGroupPython] Li_element005  label="Li_element : 005"  # scripted group (container) (typed FeaturePython)
  n = 1
  ref = Li_element
FEATURE [App::DocumentObjectGroupPython] I_element003  label="I_element : 002"  # scripted group (container) (typed FeaturePython)
  n = 1
  ref = I_element
FEATURE [App::DocumentObjectGroupPython] G4_LITHIUM_IODIDE  # scripted group (container) (typed FeaturePython)
  Dunit = g/cm3
  Dvalue = 3.494
  Group = -> [Li_element005,I_element003]
  conduct = 2
  density = 1
  expand = 3
  formula = G4_LITHIUM_IODIDE
  name = G4_LITHIUM_IODIDE
  specific = 4
FEATURE [App::DocumentObjectGroupPython] Li_element006  label="Li_element : 006"  # scripted group (container) (typed FeaturePython)
  n = 2
  ref = Li_element
FEATURE [App::DocumentObjectGroupPython] O_element055  label="O_element : 029"  # scripted group (container) (typed FeaturePython)
  n = 1
  ref = O_element
FEATURE [App::DocumentObjectGroupPython] G4_LITHIUM_OXIDE  # scripted group (container) (typed FeaturePython)
  Dunit = g/cm3
  Dvalue = 2.013
  Group = -> [Li_element006,O_element055]
  conduct = 2
  density = 1
  expand = 3
  formula = G4_LITHIUM_OXIDE
  name = G4_LITHIUM_OXIDE
  specific = 4
FEATURE [App::DocumentObjectGroupPython] Li_element007  label="Li_element : 007"  # scripted group (container) (typed FeaturePython)
  n = 2
  ref = Li_element
FEATURE [App::DocumentObjectGroupPython] B_element005  label="B_element : 005"  # scripted group (container) (typed FeaturePython)
  n = 4
  ref = B_element
FEATURE [App::DocumentObjectGroupPython] O_element056  label="O_element : 7"  # scripted group (container) (typed FeaturePython)
  n = 7
  ref = O_element
FEATURE [App::DocumentObjectGroupPython] G4_LITHIUM_TETRABORATE  # scripted group (container) (typed FeaturePython)
  Dunit = g/cm3
  Dvalue = 2.44
  Group = -> [Li_element007,B_element005,O_element056]
  conduct = 2
  density = 1
  expand = 3
  formula = G4_LITHIUM_TETRABORATE
  name = G4_LITHIUM_TETRABORATE
  specific = 4
FEATURE [App::DocumentObjectGroupPython] H_element051  label="H_element : 0.105"  # scripted group (container) (typed FeaturePython)
  n = 0.105
FEATURE [App::DocumentObjectGroupPython] C_element056  label="C_element : 0.083"  # scripted group (container) (typed FeaturePython)
  n = 0.083
FEATURE [App::DocumentObjectGroupPython] N_element023  label="N_element : 0.023"  # scripted group (container) (typed FeaturePython)
  n = 0.023
FEATURE [App::DocumentObjectGroupPython] O_element057  label="O_element : 0.779"  # scripted group (container) (typed FeaturePython)
  n = 0.779
FEATURE [App::DocumentObjectGroupPython] Na_element010  label="Na_element : 0.097"  # scripted group (container) (typed FeaturePython)
  n = 0.002
FEATURE [App::DocumentObjectGroupPython] P_element006  label="P_element : 0.105"  # scripted group (container) (typed FeaturePython)
  n = 0.001
FEATURE [App::DocumentObjectGroupPython] S_element016  label="S_element : 0.017"  # scripted group (container) (typed FeaturePython)
  n = 0.002
FEATURE [App::DocumentObjectGroupPython] Cl_element014  label="Cl_element : 0.587"  # scripted group (container) (typed FeaturePython)
  n = 0.003
FEATURE [App::DocumentObjectGroupPython] K_element005  label="K_element : 0.015"  # scripted group (container) (typed FeaturePython)
  n = 0.002
FEATURE [App::DocumentObjectGroupPython] G4_LUNG_ICRP  # scripted group (container) (typed FeaturePython)
  Dunit = g/cm3
  Dvalue = 1.04
  Group = -> [H_element051,C_element056,N_element023,O_element057,Na_element010,P_element006,S_element016,Cl_element014,K_element005]
  conduct = 2
  density = 1
  expand = 3
  formula = G4_LUNG_ICRP
  name = G4_LUNG_ICRP
  specific = 4
FEATURE [App::DocumentObjectGroupPython] H_element052  label="H_element : 0.116"  # scripted group (container) (typed FeaturePython)
  n = 0.114318
FEATURE [App::DocumentObjectGroupPython] C_element057  label="C_element : 0.656"  # scripted group (container) (typed FeaturePython)
  n = 0.655824
FEATURE [App::DocumentObjectGroupPython] O_element058  label="O_element : 0.092"  # scripted group (container) (typed FeaturePython)
  n = 0.0921831
FEATURE [App::DocumentObjectGroupPython] Mg_element004  label="Mg_element : 0.135"  # scripted group (container) (typed FeaturePython)
  n = 0.134792
FEATURE [App::DocumentObjectGroupPython] Ca_element013  label="Ca_element : 0.003"  # scripted group (container) (typed FeaturePython)
  n = 0.002883
FEATURE [App::DocumentObjectGroupPython] G4_M3_WAX  # scripted group (container) (typed FeaturePython)
  Dunit = g/cm3
  Dvalue = 1.05
  Group = -> [H_element052,C_element057,O_element058,Mg_element004,Ca_element013]
  conduct = 2
  density = 1
  expand = 3
  formula = G4_M3_WAX
  name = G4_M3_WAX
  specific = 4
FEATURE [App::DocumentObjectGroupPython] Mg_element005  label="Mg_element : 1"  # scripted group (container) (typed FeaturePython)
  n = 1
  ref = Mg_element
FEATURE [App::DocumentObjectGroupPython] C_element058  label="C_element : 031"  # scripted group (container) (typed FeaturePython)
  n = 1
  ref = C_element
FEATURE [App::DocumentObjectGroupPython] O_element059  label="O_element : 030"  # scripted group (container) (typed FeaturePython)
  n = 3
  ref = O_element
FEATURE [App::DocumentObjectGroupPython] G4_MAGNESIUM_CARBONATE  # scripted group (container) (typed FeaturePython)
  Dunit = g/cm3
  Dvalue = 2.958
  Group = -> [Mg_element005,C_element058,O_element059]
  conduct = 2
  density = 1
  expand = 3
  formula = G4_MAGNESIUM_CARBONATE
  name = G4_MAGNESIUM_CARBONATE
  specific = 4
FEATURE [App::DocumentObjectGroupPython] Mg_element006  label="Mg_element : 002"  # scripted group (container) (typed FeaturePython)
  n = 1
  ref = Mg_element
FEATURE [App::DocumentObjectGroupPython] F_element013  label="F_element : 005"  # scripted group (container) (typed FeaturePython)
  n = 2
  ref = F_element
FEATURE [App::DocumentObjectGroupPython] G4_MAGNESIUM_FLUORIDE  # scripted group (container) (typed FeaturePython)
  Dunit = g/cm3
  Dvalue = 3
  Group = -> [Mg_element006,F_element013]
  conduct = 2
  density = 1
  expand = 3
  formula = G4_MAGNESIUM_FLUORIDE
  name = G4_MAGNESIUM_FLUORIDE
  specific = 4
FEATURE [App::DocumentObjectGroupPython] Mg_element007  label="Mg_element : 003"  # scripted group (container) (typed FeaturePython)
  n = 1
  ref = Mg_element
FEATURE [App::DocumentObjectGroupPython] O_element060  label="O_element : 031"  # scripted group (container) (typed FeaturePython)
  n = 1
  ref = O_element
FEATURE [App::DocumentObjectGroupPython] G4_MAGNESIUM_OXIDE  # scripted group (container) (typed FeaturePython)
  Dunit = g/cm3
  Dvalue = 3.58
  Group = -> [Mg_element007,O_element060]
  conduct = 2
  density = 1
  expand = 3
  formula = G4_MAGNESIUM_OXIDE
  name = G4_MAGNESIUM_OXIDE
  specific = 4
FEATURE [App::DocumentObjectGroupPython] Mg_element008  label="Mg_element : 004"  # scripted group (container) (typed FeaturePython)
  n = 1
  ref = Mg_element
FEATURE [App::DocumentObjectGroupPython] B_element006  label="B_element : 006"  # scripted group (container) (typed FeaturePython)
  n = 4
  ref = B_element
FEATURE [App::DocumentObjectGroupPython] O_element061  label="O_element : 032"  # scripted group (container) (typed FeaturePython)
  n = 7
  ref = O_element
FEATURE [App::DocumentObjectGroupPython] G4_MAGNESIUM_TETRABORATE  # scripted group (container) (typed FeaturePython)
  Dunit = g/cm3
  Dvalue = 2.53
  Group = -> [Mg_element008,B_element006,O_element061]
  conduct = 2
  density = 1
  expand = 3
  formula = G4_MAGNESIUM_TETRABORATE
  name = G4_MAGNESIUM_TETRABORATE
  specific = 4
FEATURE [App::DocumentObjectGroupPython] Hg_element001  label="Hg_element : 1"  # scripted group (container) (typed FeaturePython)
  n = 1
  ref = Hg_element
FEATURE [App::DocumentObjectGroupPython] I_element004  label="I_element : 2"  # scripted group (container) (typed FeaturePython)
  n = 2
  ref = I_element
FEATURE [App::DocumentObjectGroupPython] G4_MERCURIC_IODIDE  # scripted group (container) (typed FeaturePython)
  Dunit = g/cm3
  Dvalue = 6.36
  Group = -> [Hg_element001,I_element004]
  conduct = 2
  density = 1
  expand = 3
  formula = G4_MERCURIC_IODIDE
  name = G4_MERCURIC_IODIDE
  specific = 4
FEATURE [App::DocumentObjectGroupPython] C_element059  label="C_element : 032"  # scripted group (container) (typed FeaturePython)
  n = 1
  ref = C_element
FEATURE [App::DocumentObjectGroupPython] H_element053  label="H_element : 028"  # scripted group (container) (typed FeaturePython)
  n = 4
  ref = H_element
FEATURE [App::DocumentObjectGroupPython] G4_METHANE  # scripted group (container) (typed FeaturePython)
  Dunit = g/cm3
  Dvalue = 0.000667151
  Group = -> [C_element059,H_element053]
  conduct = 2
  density = 1
  expand = 3
  formula = G4_METHANE
  name = G4_METHANE
  specific = 4
FEATURE [App::DocumentObjectGroupPython] C_element060  label="C_element : 033"  # scripted group (container) (typed FeaturePython)
  n = 1
  ref = C_element
FEATURE [App::DocumentObjectGroupPython] H_element054  label="H_element : 029"  # scripted group (container) (typed FeaturePython)
  n = 4
  ref = H_element
FEATURE [App::DocumentObjectGroupPython] O_element062  label="O_element : 033"  # scripted group (container) (typed FeaturePython)
  n = 1
  ref = O_element
FEATURE [App::DocumentObjectGroupPython] G4_METHANOL  # scripted group (container) (typed FeaturePython)
  Dunit = g/cm3
  Dvalue = 0.7914
  Group = -> [C_element060,H_element054,O_element062]
  conduct = 2
  density = 1
  expand = 3
  formula = G4_METHANOL
  name = G4_METHANOL
  specific = 4
FEATURE [App::DocumentObjectGroupPython] H_element055  label="H_element : 0.134"  # scripted group (container) (typed FeaturePython)
  n = 0.13404
FEATURE [App::DocumentObjectGroupPython] C_element061  label="C_element : 0.778"  # scripted group (container) (typed FeaturePython)
  n = 0.77796
FEATURE [App::DocumentObjectGroupPython] O_element063  label="O_element : 0.035"  # scripted group (container) (typed FeaturePython)
  n = 0.03502
FEATURE [App::DocumentObjectGroupPython] Mg_element009  label="Mg_element : 0.039"  # scripted group (container) (typed FeaturePython)
  n = 0.038594
FEATURE [App::DocumentObjectGroupPython] Ti_element002  label="Ti_element : 0.014"  # scripted group (container) (typed FeaturePython)
  n = 0.014386
FEATURE [App::DocumentObjectGroupPython] G4_MIX_D_WAX  # scripted group (container) (typed FeaturePython)
  Dunit = g/cm3
  Dvalue = 0.99
  Group = -> [H_element055,C_element061,O_element063,Mg_element009,Ti_element002]
  conduct = 2
  density = 1
  expand = 3
  formula = G4_MIX_D_WAX
  name = G4_MIX_D_WAX
  specific = 4
FEATURE [App::DocumentObjectGroupPython] H_element056  label="H_element : 0.135"  # scripted group (container) (typed FeaturePython)
  n = 0.081192
FEATURE [App::DocumentObjectGroupPython] C_element062  label="C_element : 0.583"  # scripted group (container) (typed FeaturePython)
  n = 0.583442
FEATURE [App::DocumentObjectGroupPython] N_element024  label="N_element : 0.018"  # scripted group (container) (typed FeaturePython)
  n = 0.017798
FEATURE [App::DocumentObjectGroupPython] O_element064  label="O_element : 0.186"  # scripted group (container) (typed FeaturePython)
  n = 0.186381
FEATURE [App::DocumentObjectGroupPython] Mg_element010  label="Mg_element : 0.130"  # scripted group (container) (typed FeaturePython)
  n = 0.130287
FEATURE [App::DocumentObjectGroupPython] Cl_element015  label="Cl_element : 0.588"  # scripted group (container) (typed FeaturePython)
  n = 0.0009
FEATURE [App::DocumentObjectGroupPython] G4_MS20_TISSUE  # scripted group (container) (typed FeaturePython)
  Dunit = g/cm3
  Dvalue = 1
  Group = -> [H_element056,C_element062,N_element024,O_element064,Mg_element010,Cl_element015]
  conduct = 2
  density = 1
  expand = 3
  formula = G4_MS20_TISSUE
  name = G4_MS20_TISSUE
  specific = 4
FEATURE [App::DocumentObjectGroupPython] H_element057  label="H_element : 0.136"  # scripted group (container) (typed FeaturePython)
  n = 0.102
FEATURE [App::DocumentObjectGroupPython] C_element063  label="C_element : 0.143"  # scripted group (container) (typed FeaturePython)
  n = 0.143
FEATURE [App::DocumentObjectGroupPython] N_element025  label="N_element : 0.034"  # scripted group (container) (typed FeaturePython)
  n = 0.034
FEATURE [App::DocumentObjectGroupPython] O_element065  label="O_element : 0.710"  # scripted group (container) (typed FeaturePython)
  n = 0.71
FEATURE [App::DocumentObjectGroupPython] Na_element011  label="Na_element : 0.098"  # scripted group (container) (typed FeaturePython)
  n = 0.001
FEATURE [App::DocumentObjectGroupPython] P_element007  label="P_element : 0.002"  # scripted group (container) (typed FeaturePython)
  n = 0.002
FEATURE [App::DocumentObjectGroupPython] S_element017  label="S_element : 0.018"  # scripted group (container) (typed FeaturePython)
  n = 0.003
FEATURE [App::DocumentObjectGroupPython] Cl_element016  label="Cl_element : 0.589"  # scripted group (container) (typed FeaturePython)
  n = 0.001
FEATURE [App::DocumentObjectGroupPython] K_element006  label="K_element : 0.004"  # scripted group (container) (typed FeaturePython)
  n = 0.004
FEATURE [App::DocumentObjectGroupPython] G4_MUSCLE_SKELETAL_ICRP  # scripted group (container) (typed FeaturePython)
  Dunit = g/cm3
  Dvalue = 1.05
  Group = -> [H_element057,C_element063,N_element025,O_element065,Na_element011,P_element007,S_element017,Cl_element016,K_element006]
  conduct = 2
  density = 1
  expand = 3
  formula = G4_MUSCLE_SKELETAL_ICRP
  name = G4_MUSCLE_SKELETAL_ICRP
  specific = 4
FEATURE [App::DocumentObjectGroupPython] H_element058  label="H_element : 0.137"  # scripted group (container) (typed FeaturePython)
  n = 0.102102
FEATURE [App::DocumentObjectGroupPython] C_element064  label="C_element : 0.123"  # scripted group (container) (typed FeaturePython)
  n = 0.123123
FEATURE [App::DocumentObjectGroupPython] N_element026  label="N_element : 0.756"  # scripted group (container) (typed FeaturePython)
  n = 0.035035
FEATURE [App::DocumentObjectGroupPython] O_element066  label="O_element : 0.730"  # scripted group (container) (typed FeaturePython)
  n = 0.72973
FEATURE [App::DocumentObjectGroupPython] Na_element012  label="Na_element : 0.099"  # scripted group (container) (typed FeaturePython)
  n = 0.001001
FEATURE [App::DocumentObjectGroupPython] P_element008  label="P_element : 0.106"  # scripted group (container) (typed FeaturePython)
  n = 0.002002
FEATURE [App::DocumentObjectGroupPython] S_element018  label="S_element : 0.019"  # scripted group (container) (typed FeaturePython)
  n = 0.004004
FEATURE [App::DocumentObjectGroupPython] K_element007  label="K_element : 0.016"  # scripted group (container) (typed FeaturePython)
  n = 0.003003
FEATURE [App::DocumentObjectGroupPython] G4_MUSCLE_STRIATED_ICRU  # scripted group (container) (typed FeaturePython)
  Dunit = g/cm3
  Dvalue = 1.04
  Group = -> [H_element058,C_element064,N_element026,O_element066,Na_element012,P_element008,S_element018,K_element007]
  conduct = 2
  density = 1
  expand = 3
  formula = G4_MUSCLE_STRIATED_ICRU
  name = G4_MUSCLE_STRIATED_ICRU
  specific = 4
FEATURE [App::DocumentObjectGroupPython] H_element059  label="H_element : 0.098"  # scripted group (container) (typed FeaturePython)
  n = 0.0982341
FEATURE [App::DocumentObjectGroupPython] C_element065  label="C_element : 0.156"  # scripted group (container) (typed FeaturePython)
  n = 0.156214
FEATURE [App::DocumentObjectGroupPython] N_element027  label="N_element : 0.757"  # scripted group (container) (typed FeaturePython)
  n = 0.035451
FEATURE [App::DocumentObjectGroupPython] O_element067  label="O_element : 0.880"  # scripted group (container) (typed FeaturePython)
  n = 0.710101
FEATURE [App::DocumentObjectGroupPython] G4_MUSCLE_WITH_SUCROSE  # scripted group (container) (typed FeaturePython)
  Dunit = g/cm3
  Dvalue = 1.11
  Group = -> [H_element059,C_element065,N_element027,O_element067]
  conduct = 2
  density = 1
  expand = 3
  formula = G4_MUSCLE_WITH_SUCROSE
  name = G4_MUSCLE_WITH_SUCROSE
  specific = 4
FEATURE [App::DocumentObjectGroupPython] H_element060  label="H_element : 0.138"  # scripted group (container) (typed FeaturePython)
  n = 0.101969
FEATURE [App::DocumentObjectGroupPython] C_element066  label="C_element : 0.120"  # scripted group (container) (typed FeaturePython)
  n = 0.120058
FEATURE [App::DocumentObjectGroupPython] N_element028  label="N_element : 0.758"  # scripted group (container) (typed FeaturePython)
  n = 0.035451
FEATURE [App::DocumentObjectGroupPython] O_element068  label="O_element : 0.743"  # scripted group (container) (typed FeaturePython)
  n = 0.742522
FEATURE [App::DocumentObjectGroupPython] G4_MUSCLE_WITHOUT_SUCROSE  # scripted group (container) (typed FeaturePython)
  Dunit = g/cm3
  Dvalue = 1.07
  Group = -> [H_element060,C_element066,N_element028,O_element068]
  conduct = 2
  density = 1
  expand = 3
  formula = G4_MUSCLE_WITHOUT_SUCROSE
  name = G4_MUSCLE_WITHOUT_SUCROSE
  specific = 4
FEATURE [App::DocumentObjectGroupPython] C_element067  label="C_element : 10"  # scripted group (container) (typed FeaturePython)
  n = 10
  ref = C_element
FEATURE [App::DocumentObjectGroupPython] H_element061  label="H_element : 030"  # scripted group (container) (typed FeaturePython)
  n = 8
  ref = H_element
FEATURE [App::DocumentObjectGroupPython] G4_NAPHTHALENE  # scripted group (container) (typed FeaturePython)
  Dunit = g/cm3
  Dvalue = 1.145
  Group = -> [C_element067,H_element061]
  conduct = 2
  density = 1
  expand = 3
  formula = G4_NAPHTHALENE
  name = G4_NAPHTHALENE
  specific = 4
FEATURE [App::DocumentObjectGroupPython] C_element068  label="C_element : 034"  # scripted group (container) (typed FeaturePython)
  n = 6
  ref = C_element
FEATURE [App::DocumentObjectGroupPython] H_element062  label="H_element : 031"  # scripted group (container) (typed FeaturePython)
  n = 5
  ref = H_element
FEATURE [App::DocumentObjectGroupPython] N_element029  label="N_element : 012"  # scripted group (container) (typed FeaturePython)
  n = 1
  ref = N_element
FEATURE [App::DocumentObjectGroupPython] O_element069  label="O_element : 034"  # scripted group (container) (typed FeaturePython)
  n = 2
  ref = O_element
FEATURE [App::DocumentObjectGroupPython] G4_NITROBENZENE  # scripted group (container) (typed FeaturePython)
  Dunit = g/cm3
  Dvalue = 1.19867
  Group = -> [C_element068,H_element062,N_element029,O_element069]
  conduct = 2
  density = 1
  expand = 3
  formula = G4_NITROBENZENE
  name = G4_NITROBENZENE
  specific = 4
FEATURE [App::DocumentObjectGroupPython] N_element030  label="N_element : 013"  # scripted group (container) (typed FeaturePython)
  n = 2
  ref = N_element
FEATURE [App::DocumentObjectGroupPython] O_element070  label="O_element : 035"  # scripted group (container) (typed FeaturePython)
  n = 1
  ref = O_element
FEATURE [App::DocumentObjectGroupPython] G4_NITROUS_OXIDE  # scripted group (container) (typed FeaturePython)
  Dunit = g/cm3
  Dvalue = 0.00183094
  Group = -> [N_element030,O_element070]
  conduct = 2
  density = 1
  expand = 3
  formula = G4_NITROUS_OXIDE
  name = G4_NITROUS_OXIDE
  specific = 4
FEATURE [App::DocumentObjectGroupPython] H_element063  label="H_element : 0.104"  # scripted group (container) (typed FeaturePython)
  n = 0.103509
FEATURE [App::DocumentObjectGroupPython] C_element069  label="C_element : 0.648"  # scripted group (container) (typed FeaturePython)
  n = 0.648416
FEATURE [App::DocumentObjectGroupPython] N_element031  label="N_element : 0.100"  # scripted group (container) (typed FeaturePython)
  n = 0.0995361
FEATURE [App::DocumentObjectGroupPython] O_element071  label="O_element : 0.149"  # scripted group (container) (typed FeaturePython)
  n = 0.148539
FEATURE [App::DocumentObjectGroupPython] G4_NYLON_8062  label="G4_NYLON-8062"  # scripted group (container) (typed FeaturePython)
  Dunit = g/cm3
  Dvalue = 1.08
  Group = -> [H_element063,C_element069,N_element031,O_element071]
  conduct = 2
  density = 1
  expand = 3
  formula = G4_NYLON-8062
  name = G4_NYLON-8062
  specific = 4
FEATURE [App::DocumentObjectGroupPython] C_element070  label="C_element : 035"  # scripted group (container) (typed FeaturePython)
  n = 6
  ref = C_element
FEATURE [App::DocumentObjectGroupPython] H_element064  label="H_element : 11"  # scripted group (container) (typed FeaturePython)
  n = 11
  ref = H_element
FEATURE [App::DocumentObjectGroupPython] N_element032  label="N_element : 014"  # scripted group (container) (typed FeaturePython)
  n = 1
  ref = N_element
FEATURE [App::DocumentObjectGroupPython] O_element072  label="O_element : 036"  # scripted group (container) (typed FeaturePython)
  n = 1
  ref = O_element
FEATURE [App::DocumentObjectGroupPython] G4_NYLON_6_6  label="G4_NYLON-6-6"  # scripted group (container) (typed FeaturePython)
  Dunit = g/cm3
  Dvalue = 1.14
  Group = -> [C_element070,H_element064,N_element032,O_element072]
  conduct = 2
  density = 1
  expand = 3
  formula = G4_NYLON-6-6
  name = G4_NYLON-6-6
  specific = 4
FEATURE [App::DocumentObjectGroupPython] H_element065  label="H_element : 0.139"  # scripted group (container) (typed FeaturePython)
  n = 0.107062
FEATURE [App::DocumentObjectGroupPython] C_element071  label="C_element : 0.680"  # scripted group (container) (typed FeaturePython)
  n = 0.680449
FEATURE [App::DocumentObjectGroupPython] N_element033  label="N_element : 0.099"  # scripted group (container) (typed FeaturePython)
  n = 0.099189
FEATURE [App::DocumentObjectGroupPython] O_element073  label="O_element : 0.113"  # scripted group (container) (typed FeaturePython)
  n = 0.1133
FEATURE [App::DocumentObjectGroupPython] G4_NYLON_6_10  label="G4_NYLON-6-10"  # scripted group (container) (typed FeaturePython)
  Dunit = g/cm3
  Dvalue = 1.14
  Group = -> [H_element065,C_element071,N_element033,O_element073]
  conduct = 2
  density = 1
  expand = 3
  formula = G4_NYLON-6-10
  name = G4_NYLON-6-10
  specific = 4
FEATURE [App::DocumentObjectGroupPython] H_element066  label="H_element : 0.140"  # scripted group (container) (typed FeaturePython)
  n = 0.115476
FEATURE [App::DocumentObjectGroupPython] C_element072  label="C_element : 0.721"  # scripted group (container) (typed FeaturePython)
  n = 0.720818
FEATURE [App::DocumentObjectGroupPython] N_element034  label="N_element : 0.076"  # scripted group (container) (typed FeaturePython)
  n = 0.0764169
FEATURE [App::DocumentObjectGroupPython] O_element074  label="O_element : 0.087"  # scripted group (container) (typed FeaturePython)
  n = 0.0872889
FEATURE [App::DocumentObjectGroupPython] G4_NYLON_11_RILSAN  label="G4_NYLON-11_RILSAN"  # scripted group (container) (typed FeaturePython)
  Dunit = g/cm3
  Dvalue = 1.425
  Group = -> [H_element066,C_element072,N_element034,O_element074]
  conduct = 2
  density = 1
  expand = 3
  formula = G4_NYLON-11_RILSAN
  name = G4_NYLON-11_RILSAN
  specific = 4
FEATURE [App::DocumentObjectGroupPython] C_element073  label="C_element : 8"  # scripted group (container) (typed FeaturePython)
  n = 8
  ref = C_element
FEATURE [App::DocumentObjectGroupPython] H_element067  label="H_element : 18"  # scripted group (container) (typed FeaturePython)
  n = 18
  ref = H_element
FEATURE [App::DocumentObjectGroupPython] G4_OCTANE  # scripted group (container) (typed FeaturePython)
  Dunit = g/cm3
  Dvalue = 0.7026
  Group = -> [C_element073,H_element067]
  conduct = 2
  density = 1
  expand = 3
  formula = G4_OCTANE
  name = G4_OCTANE
  specific = 4
FEATURE [App::DocumentObjectGroupPython] C_element074  label="C_element : 25"  # scripted group (container) (typed FeaturePython)
  n = 25
  ref = C_element
FEATURE [App::DocumentObjectGroupPython] H_element068  label="H_element : 52"  # scripted group (container) (typed FeaturePython)
  n = 52
  ref = H_element
FEATURE [App::DocumentObjectGroupPython] G4_PARAFFIN  # scripted group (container) (typed FeaturePython)
  Dunit = g/cm3
  Dvalue = 0.93
  Group = -> [C_element074,H_element068]
  conduct = 2
  density = 1
  expand = 3
  formula = G4_PARAFFIN
  name = G4_PARAFFIN
  specific = 4
FEATURE [App::DocumentObjectGroupPython] C_element075  label="C_element : 036"  # scripted group (container) (typed FeaturePython)
  n = 5
  ref = C_element
FEATURE [App::DocumentObjectGroupPython] H_element069  label="H_element : 032"  # scripted group (container) (typed FeaturePython)
  n = 12
  ref = H_element
FEATURE [App::DocumentObjectGroupPython] G4_N_PENTANE  label="G4_N-PENTANE"  # scripted group (container) (typed FeaturePython)
  Dunit = g/cm3
  Dvalue = 0.6262
  Group = -> [C_element075,H_element069]
  conduct = 2
  density = 1
  expand = 3
  formula = G4_N-PENTANE
  name = G4_N-PENTANE
  specific = 4
FEATURE [App::DocumentObjectGroupPython] H_element070  label="H_element : 0.014"  # scripted group (container) (typed FeaturePython)
  n = 0.0141
FEATURE [App::DocumentObjectGroupPython] C_element076  label="C_element : 0.072"  # scripted group (container) (typed FeaturePython)
  n = 0.072261
FEATURE [App::DocumentObjectGroupPython] N_element035  label="N_element : 0.019"  # scripted group (container) (typed FeaturePython)
  n = 0.01932
FEATURE [App::DocumentObjectGroupPython] O_element075  label="O_element : 0.066"  # scripted group (container) (typed FeaturePython)
  n = 0.066101
FEATURE [App::DocumentObjectGroupPython] S_element019  label="S_element : 0.020"  # scripted group (container) (typed FeaturePython)
  n = 0.00189
FEATURE [App::DocumentObjectGroupPython] Br_element004  label="Br_element : 0.349"  # scripted group (container) (typed FeaturePython)
  n = 0.349103
FEATURE [App::DocumentObjectGroupPython] Ag_element001  label="Ag_element : 0.474"  # scripted group (container) (typed FeaturePython)
  n = 0.474105
FEATURE [App::DocumentObjectGroupPython] I_element005  label="I_element : 0.003"  # scripted group (container) (typed FeaturePython)
  n = 0.00312
FEATURE [App::DocumentObjectGroupPython] G4_PHOTO_EMULSION  # scripted group (container) (typed FeaturePython)
  Dunit = g/cm3
  Dvalue = 3.815
  Group = -> [H_element070,C_element076,N_element035,O_element075,S_element019,Br_element004,Ag_element001,I_element005]
  conduct = 2
  density = 1
  expand = 3
  formula = G4_PHOTO_EMULSION
  name = G4_PHOTO_EMULSION
  specific = 4
FEATURE [App::DocumentObjectGroupPython] C_element077  label="C_element : 9"  # scripted group (container) (typed FeaturePython)
  n = 9
  ref = C_element
FEATURE [App::DocumentObjectGroupPython] H_element071  label="H_element : 033"  # scripted group (container) (typed FeaturePython)
  n = 10
  ref = H_element
FEATURE [App::DocumentObjectGroupPython] G4_PLASTIC_SC_VINYLTOLUENE  # scripted group (container) (typed FeaturePython)
  Dunit = g/cm3
  Dvalue = 1.032
  Group = -> [C_element077,H_element071]
  conduct = 2
  density = 1
  expand = 3
  formula = G4_PLASTIC_SC_VINYLTOLUENE
  name = G4_PLASTIC_SC_VINYLTOLUENE
  specific = 4
FEATURE [App::DocumentObjectGroupPython] Pu_element001  label="Pu_element : 1"  # scripted group (container) (typed FeaturePython)
  n = 1
  ref = Pu_element
FEATURE [App::DocumentObjectGroupPython] O_element076  label="O_element : 037"  # scripted group (container) (typed FeaturePython)
  n = 2
  ref = O_element
FEATURE [App::DocumentObjectGroupPython] G4_PLUTONIUM_DIOXIDE  # scripted group (container) (typed FeaturePython)
  Dunit = g/cm3
  Dvalue = 11.46
  Group = -> [Pu_element001,O_element076]
  conduct = 2
  density = 1
  expand = 3
  formula = G4_PLUTONIUM_DIOXIDE
  name = G4_PLUTONIUM_DIOXIDE
  specific = 4
FEATURE [App::DocumentObjectGroupPython] C_element078  label="C_element : 037"  # scripted group (container) (typed FeaturePython)
  n = 3
  ref = C_element
FEATURE [App::DocumentObjectGroupPython] H_element072  label="H_element : 034"  # scripted group (container) (typed FeaturePython)
  n = 3
  ref = H_element
FEATURE [App::DocumentObjectGroupPython] N_element036  label="N_element : 015"  # scripted group (container) (typed FeaturePython)
  n = 1
  ref = N_element
FEATURE [App::DocumentObjectGroupPython] G4_POLYACRYLONITRILE  # scripted group (container) (typed FeaturePython)
  Dunit = g/cm3
  Dvalue = 1.17
  Group = -> [C_element078,H_element072,N_element036]
  conduct = 2
  density = 1
  expand = 3
  formula = G4_POLYACRYLONITRILE
  name = G4_POLYACRYLONITRILE
  specific = 4
FEATURE [App::DocumentObjectGroupPython] C_element079  label="C_element : 16"  # scripted group (container) (typed FeaturePython)
  n = 16
  ref = C_element
FEATURE [App::DocumentObjectGroupPython] H_element073  label="H_element : 035"  # scripted group (container) (typed FeaturePython)
  n = 14
  ref = H_element
FEATURE [App::DocumentObjectGroupPython] O_element077  label="O_element : 038"  # scripted group (container) (typed FeaturePython)
  n = 3
  ref = O_element
FEATURE [App::DocumentObjectGroupPython] G4_POLYCARBONATE  # scripted group (container) (typed FeaturePython)
  Dunit = g/cm3
  Dvalue = 1.2
  Group = -> [C_element079,H_element073,O_element077]
  conduct = 2
  density = 1
  expand = 3
  formula = G4_POLYCARBONATE
  name = G4_POLYCARBONATE
  specific = 4
FEATURE [App::DocumentObjectGroupPython] C_element080  label="C_element : 038"  # scripted group (container) (typed FeaturePython)
  n = 8
  ref = C_element
FEATURE [App::DocumentObjectGroupPython] H_element074  label="H_element : 036"  # scripted group (container) (typed FeaturePython)
  n = 7
  ref = H_element
FEATURE [App::DocumentObjectGroupPython] Cl_element017  label="Cl_element : 007"  # scripted group (container) (typed FeaturePython)
  n = 1
  ref = Cl_element
FEATURE [App::DocumentObjectGroupPython] G4_POLYCHLOROSTYRENE  # scripted group (container) (typed FeaturePython)
  Dunit = g/cm3
  Dvalue = 1.3
  Group = -> [C_element080,H_element074,Cl_element017]
  conduct = 2
  density = 1
  expand = 3
  formula = G4_POLYCHLOROSTYRENE
  name = G4_POLYCHLOROSTYRENE
  specific = 4
FEATURE [App::DocumentObjectGroupPython] C_element081  label="C_element : 039"  # scripted group (container) (typed FeaturePython)
  n = 1
  ref = C_element
FEATURE [App::DocumentObjectGroupPython] H_element075  label="H_element : 037"  # scripted group (container) (typed FeaturePython)
  n = 2
  ref = H_element
FEATURE [App::DocumentObjectGroupPython] G4_POLYETHYLENE  # scripted group (container) (typed FeaturePython)
  Dunit = g/cm3
  Dvalue = 0.94
  Group = -> [C_element081,H_element075]
  conduct = 2
  density = 1
  expand = 3
  formula = G4_POLYETHYLENE
  name = G4_POLYETHYLENE
  specific = 4
FEATURE [App::DocumentObjectGroupPython] C_element082  label="C_element : 040"  # scripted group (container) (typed FeaturePython)
  n = 10
  ref = C_element
FEATURE [App::DocumentObjectGroupPython] H_element076  label="H_element : 038"  # scripted group (container) (typed FeaturePython)
  n = 8
  ref = H_element
FEATURE [App::DocumentObjectGroupPython] O_element078  label="O_element : 039"  # scripted group (container) (typed FeaturePython)
  n = 4
  ref = O_element
FEATURE [App::DocumentObjectGroupPython] G4_MYLAR  # scripted group (container) (typed FeaturePython)
  Dunit = g/cm3
  Dvalue = 1.4
  Group = -> [C_element082,H_element076,O_element078]
  conduct = 2
  density = 1
  expand = 3
  formula = G4_MYLAR
  name = G4_MYLAR
  specific = 4
FEATURE [App::DocumentObjectGroupPython] C_element083  label="C_element : 041"  # scripted group (container) (typed FeaturePython)
  n = 5
  ref = C_element
FEATURE [App::DocumentObjectGroupPython] H_element077  label="H_element : 039"  # scripted group (container) (typed FeaturePython)
  n = 8
  ref = H_element
FEATURE [App::DocumentObjectGroupPython] O_element079  label="O_element : 040"  # scripted group (container) (typed FeaturePython)
  n = 2
  ref = O_element
FEATURE [App::DocumentObjectGroupPython] G4_PLEXIGLASS  # scripted group (container) (typed FeaturePython)
  Dunit = g/cm3
  Dvalue = 1.19
  Group = -> [C_element083,H_element077,O_element079]
  conduct = 2
  density = 1
  expand = 3
  formula = G4_PLEXIGLASS
  name = G4_PLEXIGLASS
  specific = 4
FEATURE [App::DocumentObjectGroupPython] C_element084  label="C_element : 042"  # scripted group (container) (typed FeaturePython)
  n = 1
  ref = C_element
FEATURE [App::DocumentObjectGroupPython] H_element078  label="H_element : 040"  # scripted group (container) (typed FeaturePython)
  n = 2
  ref = H_element
FEATURE [App::DocumentObjectGroupPython] O_element080  label="O_element : 041"  # scripted group (container) (typed FeaturePython)
  n = 1
  ref = O_element
FEATURE [App::DocumentObjectGroupPython] G4_POLYOXYMETHYLENE  # scripted group (container) (typed FeaturePython)
  Dunit = g/cm3
  Dvalue = 1.425
  Group = -> [C_element084,H_element078,O_element080]
  conduct = 2
  density = 1
  expand = 3
  formula = G4_POLYOXYMETHYLENE
  name = G4_POLYOXYMETHYLENE
  specific = 4
FEATURE [App::DocumentObjectGroupPython] C_element085  label="C_element : 043"  # scripted group (container) (typed FeaturePython)
  n = 2
  ref = C_element
FEATURE [App::DocumentObjectGroupPython] H_element079  label="H_element : 041"  # scripted group (container) (typed FeaturePython)
  n = 4
  ref = H_element
FEATURE [App::DocumentObjectGroupPython] G4_POLYPROPYLENE  # scripted group (container) (typed FeaturePython)
  Dunit = g/cm3
  Dvalue = 0.9
  Group = -> [C_element085,H_element079]
  conduct = 2
  density = 1
  expand = 3
  formula = G4_POLYPROPYLENE
  name = G4_POLYPROPYLENE
  specific = 4
FEATURE [App::DocumentObjectGroupPython] C_element086  label="C_element : 044"  # scripted group (container) (typed FeaturePython)
  n = 8
  ref = C_element
FEATURE [App::DocumentObjectGroupPython] H_element080  label="H_element : 042"  # scripted group (container) (typed FeaturePython)
  n = 8
  ref = H_element
FEATURE [App::DocumentObjectGroupPython] G4_POLYSTYRENE  # scripted group (container) (typed FeaturePython)
  Dunit = g/cm3
  Dvalue = 1.06
  Group = -> [C_element086,H_element080]
  conduct = 2
  density = 1
  expand = 3
  formula = G4_POLYSTYRENE
  name = G4_POLYSTYRENE
  specific = 4
FEATURE [App::DocumentObjectGroupPython] C_element087  label="C_element : 045"  # scripted group (container) (typed FeaturePython)
  n = 2
  ref = C_element
FEATURE [App::DocumentObjectGroupPython] F_element014  label="F_element : 4"  # scripted group (container) (typed FeaturePython)
  n = 4
  ref = F_element
FEATURE [App::DocumentObjectGroupPython] G4_TEFLON  # scripted group (container) (typed FeaturePython)
  Dunit = g/cm3
  Dvalue = 2.2
  Group = -> [C_element087,F_element014]
  conduct = 2
  density = 1
  expand = 3
  formula = G4_TEFLON
  name = G4_TEFLON
  specific = 4
FEATURE [App::DocumentObjectGroupPython] C_element088  label="C_element : 046"  # scripted group (container) (typed FeaturePython)
  n = 2
  ref = C_element
FEATURE [App::DocumentObjectGroupPython] F_element015  label="F_element : 006"  # scripted group (container) (typed FeaturePython)
  n = 3
  ref = F_element
FEATURE [App::DocumentObjectGroupPython] Cl_element018  label="Cl_element : 008"  # scripted group (container) (typed FeaturePython)
  n = 1
  ref = Cl_element
FEATURE [App::DocumentObjectGroupPython] G4_POLYTRIFLUOROCHLOROETHYLENE  # scripted group (container) (typed FeaturePython)
  Dunit = g/cm3
  Dvalue = 2.1
  Group = -> [C_element088,F_element015,Cl_element018]
  conduct = 2
  density = 1
  expand = 3
  formula = G4_POLYTRIFLUOROCHLOROETHYLENE
  name = G4_POLYTRIFLUOROCHLOROETHYLENE
  specific = 4
FEATURE [App::DocumentObjectGroupPython] C_element089  label="C_element : 047"  # scripted group (container) (typed FeaturePython)
  n = 4
  ref = C_element
FEATURE [App::DocumentObjectGroupPython] H_element081  label="H_element : 043"  # scripted group (container) (typed FeaturePython)
  n = 6
  ref = H_element
FEATURE [App::DocumentObjectGroupPython] O_element081  label="O_element : 042"  # scripted group (container) (typed FeaturePython)
  n = 2
  ref = O_element
FEATURE [App::DocumentObjectGroupPython] G4_POLYVINYL_ACETATE  # scripted group (container) (typed FeaturePython)
  Dunit = g/cm3
  Dvalue = 1.19
  Group = -> [C_element089,H_element081,O_element081]
  conduct = 2
  density = 1
  expand = 3
  formula = G4_POLYVINYL_ACETATE
  name = G4_POLYVINYL_ACETATE
  specific = 4
FEATURE [App::DocumentObjectGroupPython] C_element090  label="C_element : 048"  # scripted group (container) (typed FeaturePython)
  n = 2
  ref = C_element
FEATURE [App::DocumentObjectGroupPython] H_element082  label="H_element : 044"  # scripted group (container) (typed FeaturePython)
  n = 4
  ref = H_element
FEATURE [App::DocumentObjectGroupPython] O_element082  label="O_element : 043"  # scripted group (container) (typed FeaturePython)
  n = 1
  ref = O_element
FEATURE [App::DocumentObjectGroupPython] G4_POLYVINYL_ALCOHOL  # scripted group (container) (typed FeaturePython)
  Dunit = g/cm3
  Dvalue = 1.3
  Group = -> [C_element090,H_element082,O_element082]
  conduct = 2
  density = 1
  expand = 3
  formula = G4_POLYVINYL_ALCOHOL
  name = G4_POLYVINYL_ALCOHOL
  specific = 4
FEATURE [App::DocumentObjectGroupPython] C_element091  label="C_element : 049"  # scripted group (container) (typed FeaturePython)
  n = 8
  ref = C_element
FEATURE [App::DocumentObjectGroupPython] H_element083  label="H_element : 045"  # scripted group (container) (typed FeaturePython)
  n = 14
  ref = H_element
FEATURE [App::DocumentObjectGroupPython] O_element083  label="O_element : 044"  # scripted group (container) (typed FeaturePython)
  n = 2
  ref = O_element
FEATURE [App::DocumentObjectGroupPython] G4_POLYVINYL_BUTYRAL  # scripted group (container) (typed FeaturePython)
  Dunit = g/cm3
  Dvalue = 1.12
  Group = -> [C_element091,H_element083,O_element083]
  conduct = 2
  density = 1
  expand = 3
  formula = G4_POLYVINYL_BUTYRAL
  name = G4_POLYVINYL_BUTYRAL
  specific = 4
FEATURE [App::DocumentObjectGroupPython] C_element092  label="C_element : 050"  # scripted group (container) (typed FeaturePython)
  n = 2
  ref = C_element
FEATURE [App::DocumentObjectGroupPython] H_element084  label="H_element : 046"  # scripted group (container) (typed FeaturePython)
  n = 3
  ref = H_element
FEATURE [App::DocumentObjectGroupPython] Cl_element019  label="Cl_element : 009"  # scripted group (container) (typed FeaturePython)
  n = 1
  ref = Cl_element
FEATURE [App::DocumentObjectGroupPython] G4_POLYVINYL_CHLORIDE  # scripted group (container) (typed FeaturePython)
  Dunit = g/cm3
  Dvalue = 1.3
  Group = -> [C_element092,H_element084,Cl_element019]
  conduct = 2
  density = 1
  expand = 3
  formula = G4_POLYVINYL_CHLORIDE
  name = G4_POLYVINYL_CHLORIDE
  specific = 4
FEATURE [App::DocumentObjectGroupPython] C_element093  label="C_element : 051"  # scripted group (container) (typed FeaturePython)
  n = 2
  ref = C_element
FEATURE [App::DocumentObjectGroupPython] H_element085  label="H_element : 047"  # scripted group (container) (typed FeaturePython)
  n = 2
  ref = H_element
FEATURE [App::DocumentObjectGroupPython] Cl_element020  label="Cl_element : 010"  # scripted group (container) (typed FeaturePython)
  n = 2
  ref = Cl_element
FEATURE [App::DocumentObjectGroupPython] G4_POLYVINYLIDENE_CHLORIDE  # scripted group (container) (typed FeaturePython)
  Dunit = g/cm3
  Dvalue = 1.7
  Group = -> [C_element093,H_element085,Cl_element020]
  conduct = 2
  density = 1
  expand = 3
  formula = G4_POLYVINYLIDENE_CHLORIDE
  name = G4_POLYVINYLIDENE_CHLORIDE
  specific = 4
FEATURE [App::DocumentObjectGroupPython] C_element094  label="C_element : 052"  # scripted group (container) (typed FeaturePython)
  n = 2
  ref = C_element
FEATURE [App::DocumentObjectGroupPython] H_element086  label="H_element : 048"  # scripted group (container) (typed FeaturePython)
  n = 2
  ref = H_element
FEATURE [App::DocumentObjectGroupPython] F_element016  label="F_element : 007"  # scripted group (container) (typed FeaturePython)
  n = 2
  ref = F_element
FEATURE [App::DocumentObjectGroupPython] G4_POLYVINYLIDENE_FLUORIDE  # scripted group (container) (typed FeaturePython)
  Dunit = g/cm3
  Dvalue = 1.76
  Group = -> [C_element094,H_element086,F_element016]
  conduct = 2
  density = 1
  expand = 3
  formula = G4_POLYVINYLIDENE_FLUORIDE
  name = G4_POLYVINYLIDENE_FLUORIDE
  specific = 4
FEATURE [App::DocumentObjectGroupPython] C_element095  label="C_element : 053"  # scripted group (container) (typed FeaturePython)
  n = 6
  ref = C_element
FEATURE [App::DocumentObjectGroupPython] H_element087  label="H_element : 9"  # scripted group (container) (typed FeaturePython)
  n = 9
  ref = H_element
FEATURE [App::DocumentObjectGroupPython] N_element037  label="N_element : 016"  # scripted group (container) (typed FeaturePython)
  n = 1
  ref = N_element
FEATURE [App::DocumentObjectGroupPython] O_element084  label="O_element : 045"  # scripted group (container) (typed FeaturePython)
  n = 1
  ref = O_element
FEATURE [App::DocumentObjectGroupPython] G4_POLYVINYL_PYRROLIDONE  # scripted group (container) (typed FeaturePython)
  Dunit = g/cm3
  Dvalue = 1.25
  Group = -> [C_element095,H_element087,N_element037,O_element084]
  conduct = 2
  density = 1
  expand = 3
  formula = G4_POLYVINYL_PYRROLIDONE
  name = G4_POLYVINYL_PYRROLIDONE
  specific = 4
FEATURE [App::DocumentObjectGroupPython] K_element008  label="K_element : 1"  # scripted group (container) (typed FeaturePython)
  n = 1
  ref = K_element
FEATURE [App::DocumentObjectGroupPython] I_element006  label="I_element : 003"  # scripted group (container) (typed FeaturePython)
  n = 1
  ref = I_element
FEATURE [App::DocumentObjectGroupPython] G4_POTASSIUM_IODIDE  # scripted group (container) (typed FeaturePython)
  Dunit = g/cm3
  Dvalue = 3.13
  Group = -> [K_element008,I_element006]
  conduct = 2
  density = 1
  expand = 3
  formula = G4_POTASSIUM_IODIDE
  name = G4_POTASSIUM_IODIDE
  specific = 4
FEATURE [App::DocumentObjectGroupPython] K_element009  label="K_element : 2"  # scripted group (container) (typed FeaturePython)
  n = 2
  ref = K_element
FEATURE [App::DocumentObjectGroupPython] O_element085  label="O_element : 046"  # scripted group (container) (typed FeaturePython)
  n = 1
  ref = O_element
FEATURE [App::DocumentObjectGroupPython] G4_POTASSIUM_OXIDE  # scripted group (container) (typed FeaturePython)
  Dunit = g/cm3
  Dvalue = 2.32
  Group = -> [K_element009,O_element085]
  conduct = 2
  density = 1
  expand = 3
  formula = G4_POTASSIUM_OXIDE
  name = G4_POTASSIUM_OXIDE
  specific = 4
FEATURE [App::DocumentObjectGroupPython] C_element096  label="C_element : 054"  # scripted group (container) (typed FeaturePython)
  n = 3
  ref = C_element
FEATURE [App::DocumentObjectGroupPython] H_element088  label="H_element : 049"  # scripted group (container) (typed FeaturePython)
  n = 8
  ref = H_element
FEATURE [App::DocumentObjectGroupPython] G4_PROPANE  # scripted group (container) (typed FeaturePython)
  Dunit = g/cm3
  Dvalue = 0.00187939
  Group = -> [C_element096,H_element088]
  conduct = 2
  density = 1
  expand = 3
  formula = G4_PROPANE
  name = G4_PROPANE
  specific = 4
FEATURE [App::DocumentObjectGroupPython] C_element097  label="C_element : 055"  # scripted group (container) (typed FeaturePython)
  n = 3
  ref = C_element
FEATURE [App::DocumentObjectGroupPython] H_element089  label="H_element : 050"  # scripted group (container) (typed FeaturePython)
  n = 8
  ref = H_element
FEATURE [App::DocumentObjectGroupPython] G4_lPROPANE  # scripted group (container) (typed FeaturePython)
  Dunit = g/cm3
  Dvalue = 0.43
  Group = -> [C_element097,H_element089]
  conduct = 2
  density = 1
  expand = 3
  formula = G4_lPROPANE
  name = G4_lPROPANE
  specific = 4
FEATURE [App::DocumentObjectGroupPython] C_element098  label="C_element : 056"  # scripted group (container) (typed FeaturePython)
  n = 3
  ref = C_element
FEATURE [App::DocumentObjectGroupPython] H_element090  label="H_element : 051"  # scripted group (container) (typed FeaturePython)
  n = 8
  ref = H_element
FEATURE [App::DocumentObjectGroupPython] O_element086  label="O_element : 047"  # scripted group (container) (typed FeaturePython)
  n = 1
  ref = O_element
FEATURE [App::DocumentObjectGroupPython] G4_N_PROPYL_ALCOHOL  label="G4_N-PROPYL_ALCOHOL"  # scripted group (container) (typed FeaturePython)
  Dunit = g/cm3
  Dvalue = 0.8035
  Group = -> [C_element098,H_element090,O_element086]
  conduct = 2
  density = 1
  expand = 3
  formula = G4_N-PROPYL_ALCOHOL
  name = G4_N-PROPYL_ALCOHOL
  specific = 4
FEATURE [App::DocumentObjectGroupPython] C_element099  label="C_element : 057"  # scripted group (container) (typed FeaturePython)
  n = 5
  ref = C_element
FEATURE [App::DocumentObjectGroupPython] H_element091  label="H_element : 052"  # scripted group (container) (typed FeaturePython)
  n = 5
  ref = H_element
FEATURE [App::DocumentObjectGroupPython] N_element038  label="N_element : 017"  # scripted group (container) (typed FeaturePython)
  n = 1
  ref = N_element
FEATURE [App::DocumentObjectGroupPython] G4_PYRIDINE  # scripted group (container) (typed FeaturePython)
  Dunit = g/cm3
  Dvalue = 0.9819
  Group = -> [C_element099,H_element091,N_element038]
  conduct = 2
  density = 1
  expand = 3
  formula = G4_PYRIDINE
  name = G4_PYRIDINE
  specific = 4
FEATURE [App::DocumentObjectGroupPython] H_element092  label="H_element : 0.144"  # scripted group (container) (typed FeaturePython)
  n = 0.143711
FEATURE [App::DocumentObjectGroupPython] C_element100  label="C_element : 0.856"  # scripted group (container) (typed FeaturePython)
  n = 0.856289
FEATURE [App::DocumentObjectGroupPython] G4_RUBBER_BUTYL  # scripted group (container) (typed FeaturePython)
  Dunit = g/cm3
  Dvalue = 0.92
  Group = -> [H_element092,C_element100]
  conduct = 2
  density = 1
  expand = 3
  formula = G4_RUBBER_BUTYL
  name = G4_RUBBER_BUTYL
  specific = 4
FEATURE [App::DocumentObjectGroupPython] H_element093  label="H_element : 0.118"  # scripted group (container) (typed FeaturePython)
  n = 0.118371
FEATURE [App::DocumentObjectGroupPython] C_element101  label="C_element : 0.882"  # scripted group (container) (typed FeaturePython)
  n = 0.881629
FEATURE [App::DocumentObjectGroupPython] G4_RUBBER_NATURAL  # scripted group (container) (typed FeaturePython)
  Dunit = g/cm3
  Dvalue = 0.92
  Group = -> [H_element093,C_element101]
  conduct = 2
  density = 1
  expand = 3
  formula = G4_RUBBER_NATURAL
  name = G4_RUBBER_NATURAL
  specific = 4
FEATURE [App::DocumentObjectGroupPython] H_element094  label="H_element : 0.145"  # scripted group (container) (typed FeaturePython)
  n = 0.05692
FEATURE [App::DocumentObjectGroupPython] C_element102  label="C_element : 0.543"  # scripted group (container) (typed FeaturePython)
  n = 0.542646
FEATURE [App::DocumentObjectGroupPython] Cl_element021  label="Cl_element : 0.400"  # scripted group (container) (typed FeaturePython)
  n = 0.400434
FEATURE [App::DocumentObjectGroupPython] G4_RUBBER_NEOPRENE  # scripted group (container) (typed FeaturePython)
  Dunit = g/cm3
  Dvalue = 1.23
  Group = -> [H_element094,C_element102,Cl_element021]
  conduct = 2
  density = 1
  expand = 3
  formula = G4_RUBBER_NEOPRENE
  name = G4_RUBBER_NEOPRENE
  specific = 4
FEATURE [App::DocumentObjectGroupPython] Si_element006  label="Si_element : 1"  # scripted group (container) (typed FeaturePython)
  n = 1
  ref = Si_element
FEATURE [App::DocumentObjectGroupPython] O_element087  label="O_element : 048"  # scripted group (container) (typed FeaturePython)
  n = 2
  ref = O_element
FEATURE [App::DocumentObjectGroupPython] G4_SILICON_DIOXIDE  # scripted group (container) (typed FeaturePython)
  Dunit = g/cm3
  Dvalue = 2.32
  Group = -> [Si_element006,O_element087]
  conduct = 2
  density = 1
  expand = 3
  formula = G4_SILICON_DIOXIDE
  name = G4_SILICON_DIOXIDE
  specific = 4
FEATURE [App::DocumentObjectGroupPython] Ag_element002  label="Ag_element : 1"  # scripted group (container) (typed FeaturePython)
  n = 1
  ref = Ag_element
FEATURE [App::DocumentObjectGroupPython] Br_element005  label="Br_element : 003"  # scripted group (container) (typed FeaturePython)
  n = 1
  ref = Br_element
FEATURE [App::DocumentObjectGroupPython] G4_SILVER_BROMIDE  # scripted group (container) (typed FeaturePython)
  Dunit = g/cm3
  Dvalue = 6.473
  Group = -> [Ag_element002,Br_element005]
  conduct = 2
  density = 1
  expand = 3
  formula = G4_SILVER_BROMIDE
  name = G4_SILVER_BROMIDE
  specific = 4
FEATURE [App::DocumentObjectGroupPython] Ag_element003  label="Ag_element : 002"  # scripted group (container) (typed FeaturePython)
  n = 1
  ref = Ag_element
FEATURE [App::DocumentObjectGroupPython] Cl_element022  label="Cl_element : 011"  # scripted group (container) (typed FeaturePython)
  n = 1
  ref = Cl_element
FEATURE [App::DocumentObjectGroupPython] G4_SILVER_CHLORIDE  # scripted group (container) (typed FeaturePython)
  Dunit = g/cm3
  Dvalue = 5.56
  Group = -> [Ag_element003,Cl_element022]
  conduct = 2
  density = 1
  expand = 3
  formula = G4_SILVER_CHLORIDE
  name = G4_SILVER_CHLORIDE
  specific = 4
FEATURE [App::DocumentObjectGroupPython] Br_element006  label="Br_element : 0.423"  # scripted group (container) (typed FeaturePython)
  n = 0.422895
FEATURE [App::DocumentObjectGroupPython] Ag_element004  label="Ag_element : 0.574"  # scripted group (container) (typed FeaturePython)
  n = 0.573748
FEATURE [App::DocumentObjectGroupPython] I_element007  label="I_element : 0.649"  # scripted group (container) (typed FeaturePython)
  n = 0.003357
FEATURE [App::DocumentObjectGroupPython] G4_SILVER_HALIDES  # scripted group (container) (typed FeaturePython)
  Dunit = g/cm3
  Dvalue = 6.47
  Group = -> [Br_element006,Ag_element004,I_element007]
  conduct = 2
  density = 1
  expand = 3
  formula = G4_SILVER_HALIDES
  name = G4_SILVER_HALIDES
  specific = 4
FEATURE [App::DocumentObjectGroupPython] Ag_element005  label="Ag_element : 003"  # scripted group (container) (typed FeaturePython)
  n = 1
  ref = Ag_element
FEATURE [App::DocumentObjectGroupPython] I_element008  label="I_element : 004"  # scripted group (container) (typed FeaturePython)
  n = 1
  ref = I_element
FEATURE [App::DocumentObjectGroupPython] G4_SILVER_IODIDE  # scripted group (container) (typed FeaturePython)
  Dunit = g/cm3
  Dvalue = 6.01
  Group = -> [Ag_element005,I_element008]
  conduct = 2
  density = 1
  expand = 3
  formula = G4_SILVER_IODIDE
  name = G4_SILVER_IODIDE
  specific = 4
FEATURE [App::DocumentObjectGroupPython] H_element095  label="H_element : 0.100"  # scripted group (container) (typed FeaturePython)
  n = 0.1
FEATURE [App::DocumentObjectGroupPython] C_element103  label="C_element : 0.204"  # scripted group (container) (typed FeaturePython)
  n = 0.204
FEATURE [App::DocumentObjectGroupPython] N_element039  label="N_element : 0.759"  # scripted group (container) (typed FeaturePython)
  n = 0.042
FEATURE [App::DocumentObjectGroupPython] O_element088  label="O_element : 0.645"  # scripted group (container) (typed FeaturePython)
  n = 0.645
FEATURE [App::DocumentObjectGroupPython] Na_element013  label="Na_element : 0.100"  # scripted group (container) (typed FeaturePython)
  n = 0.002
FEATURE [App::DocumentObjectGroupPython] P_element009  label="P_element : 0.107"  # scripted group (container) (typed FeaturePython)
  n = 0.001
FEATURE [App::DocumentObjectGroupPython] S_element020  label="S_element : 0.021"  # scripted group (container) (typed FeaturePython)
  n = 0.002
FEATURE [App::DocumentObjectGroupPython] Cl_element023  label="Cl_element : 0.590"  # scripted group (container) (typed FeaturePython)
  n = 0.003
FEATURE [App::DocumentObjectGroupPython] K_element010  label="K_element : 0.001"  # scripted group (container) (typed FeaturePython)
  n = 0.001
FEATURE [App::DocumentObjectGroupPython] G4_SKIN_ICRP  # scripted group (container) (typed FeaturePython)
  Dunit = g/cm3
  Dvalue = 1.09
  Group = -> [H_element095,C_element103,N_element039,O_element088,Na_element013,P_element009,S_element020,Cl_element023,K_element010]
  conduct = 2
  density = 1
  expand = 3
  formula = G4_SKIN_ICRP
  name = G4_SKIN_ICRP
  specific = 4
FEATURE [App::DocumentObjectGroupPython] Na_element014  label="Na_element : 2"  # scripted group (container) (typed FeaturePython)
  n = 2
  ref = Na_element
FEATURE [App::DocumentObjectGroupPython] C_element104  label="C_element : 058"  # scripted group (container) (typed FeaturePython)
  n = 1
  ref = C_element
FEATURE [App::DocumentObjectGroupPython] O_element089  label="O_element : 049"  # scripted group (container) (typed FeaturePython)
  n = 3
  ref = O_element
FEATURE [App::DocumentObjectGroupPython] G4_SODIUM_CARBONATE  # scripted group (container) (typed FeaturePython)
  Dunit = g/cm3
  Dvalue = 2.532
  Group = -> [Na_element014,C_element104,O_element089]
  conduct = 2
  density = 1
  expand = 3
  formula = G4_SODIUM_CARBONATE
  name = G4_SODIUM_CARBONATE
  specific = 4
FEATURE [App::DocumentObjectGroupPython] Na_element015  label="Na_element : 1"  # scripted group (container) (typed FeaturePython)
  n = 1
  ref = Na_element
FEATURE [App::DocumentObjectGroupPython] I_element009  label="I_element : 005"  # scripted group (container) (typed FeaturePython)
  n = 1
  ref = I_element
FEATURE [App::DocumentObjectGroupPython] G4_SODIUM_IODIDE  # scripted group (container) (typed FeaturePython)
  Dunit = g/cm3
  Dvalue = 3.667
  Group = -> [Na_element015,I_element009]
  conduct = 2
  density = 1
  expand = 3
  formula = G4_SODIUM_IODIDE
  name = G4_SODIUM_IODIDE
  specific = 4
FEATURE [App::DocumentObjectGroupPython] Na_element016  label="Na_element : 003"  # scripted group (container) (typed FeaturePython)
  n = 2
  ref = Na_element
FEATURE [App::DocumentObjectGroupPython] O_element090  label="O_element : 050"  # scripted group (container) (typed FeaturePython)
  n = 1
  ref = O_element
FEATURE [App::DocumentObjectGroupPython] G4_SODIUM_MONOXIDE  # scripted group (container) (typed FeaturePython)
  Dunit = g/cm3
  Dvalue = 2.27
  Group = -> [Na_element016,O_element090]
  conduct = 2
  density = 1
  expand = 3
  formula = G4_SODIUM_MONOXIDE
  name = G4_SODIUM_MONOXIDE
  specific = 4
FEATURE [App::DocumentObjectGroupPython] Na_element017  label="Na_element : 004"  # scripted group (container) (typed FeaturePython)
  n = 1
  ref = Na_element
FEATURE [App::DocumentObjectGroupPython] N_element040  label="N_element : 018"  # scripted group (container) (typed FeaturePython)
  n = 1
  ref = N_element
FEATURE [App::DocumentObjectGroupPython] O_element091  label="O_element : 051"  # scripted group (container) (typed FeaturePython)
  n = 3
  ref = O_element
FEATURE [App::DocumentObjectGroupPython] G4_SODIUM_NITRATE  # scripted group (container) (typed FeaturePython)
  Dunit = g/cm3
  Dvalue = 2.261
  Group = -> [Na_element017,N_element040,O_element091]
  conduct = 2
  density = 1
  expand = 3
  formula = G4_SODIUM_NITRATE
  name = G4_SODIUM_NITRATE
  specific = 4
FEATURE [App::DocumentObjectGroupPython] C_element105  label="C_element : 059"  # scripted group (container) (typed FeaturePython)
  n = 14
  ref = C_element
FEATURE [App::DocumentObjectGroupPython] H_element096  label="H_element : 053"  # scripted group (container) (typed FeaturePython)
  n = 12
  ref = H_element
FEATURE [App::DocumentObjectGroupPython] G4_STILBENE  # scripted group (container) (typed FeaturePython)
  Dunit = g/cm3
  Dvalue = 0.9707
  Group = -> [C_element105,H_element096]
  conduct = 2
  density = 1
  expand = 3
  formula = G4_STILBENE
  name = G4_STILBENE
  specific = 4
FEATURE [App::DocumentObjectGroupPython] C_element106  label="C_element : 12"  # scripted group (container) (typed FeaturePython)
  n = 12
  ref = C_element
FEATURE [App::DocumentObjectGroupPython] H_element097  label="H_element : 22"  # scripted group (container) (typed FeaturePython)
  n = 22
  ref = H_element
FEATURE [App::DocumentObjectGroupPython] O_element092  label="O_element : 11"  # scripted group (container) (typed FeaturePython)
  n = 11
  ref = O_element
FEATURE [App::DocumentObjectGroupPython] G4_SUCROSE  # scripted group (container) (typed FeaturePython)
  Dunit = g/cm3
  Dvalue = 1.5805
  Group = -> [C_element106,H_element097,O_element092]
  conduct = 2
  density = 1
  expand = 3
  formula = G4_SUCROSE
  name = G4_SUCROSE
  specific = 4
FEATURE [App::DocumentObjectGroupPython] C_element107  label="C_element : 18"  # scripted group (container) (typed FeaturePython)
  n = 18
  ref = C_element
FEATURE [App::DocumentObjectGroupPython] H_element098  label="H_element : 054"  # scripted group (container) (typed FeaturePython)
  n = 14
  ref = H_element
FEATURE [App::DocumentObjectGroupPython] G4_TERPHENYL  # scripted group (container) (typed FeaturePython)
  Dunit = g/cm3
  Dvalue = 1.24
  Group = -> [C_element107,H_element098]
  conduct = 2
  density = 1
  expand = 3
  formula = G4_TERPHENYL
  name = G4_TERPHENYL
  specific = 4
FEATURE [App::DocumentObjectGroupPython] H_element099  label="H_element : 0.146"  # scripted group (container) (typed FeaturePython)
  n = 0.106
FEATURE [App::DocumentObjectGroupPython] C_element108  label="C_element : 0.883"  # scripted group (container) (typed FeaturePython)
  n = 0.099
FEATURE [App::DocumentObjectGroupPython] N_element041  label="N_element : 0.020"  # scripted group (container) (typed FeaturePython)
  n = 0.02
FEATURE [App::DocumentObjectGroupPython] O_element093  label="O_element : 0.766"  # scripted group (container) (typed FeaturePython)
  n = 0.766
FEATURE [App::DocumentObjectGroupPython] Na_element018  label="Na_element : 0.101"  # scripted group (container) (typed FeaturePython)
  n = 0.002
FEATURE [App::DocumentObjectGroupPython] P_element010  label="P_element : 0.108"  # scripted group (container) (typed FeaturePython)
  n = 0.001
FEATURE [App::DocumentObjectGroupPython] S_element021  label="S_element : 0.022"  # scripted group (container) (typed FeaturePython)
  n = 0.002
FEATURE [App::DocumentObjectGroupPython] Cl_element024  label="Cl_element : 0.002"  # scripted group (container) (typed FeaturePython)
  n = 0.002
FEATURE [App::DocumentObjectGroupPython] K_element011  label="K_element : 0.017"  # scripted group (container) (typed FeaturePython)
  n = 0.002
FEATURE [App::DocumentObjectGroupPython] G4_TESTIS_ICRP  # scripted group (container) (typed FeaturePython)
  Dunit = g/cm3
  Dvalue = 1.04
  Group = -> [H_element099,C_element108,N_element041,O_element093,Na_element018,P_element010,S_element021,Cl_element024,K_element011]
  conduct = 2
  density = 1
  expand = 3
  formula = G4_TESTIS_ICRP
  name = G4_TESTIS_ICRP
  specific = 4
FEATURE [App::DocumentObjectGroupPython] C_element109  label="C_element : 060"  # scripted group (container) (typed FeaturePython)
  n = 2
  ref = C_element
FEATURE [App::DocumentObjectGroupPython] Cl_element025  label="Cl_element : 012"  # scripted group (container) (typed FeaturePython)
  n = 4
  ref = Cl_element
FEATURE [App::DocumentObjectGroupPython] G4_TETRACHLOROETHYLENE  # scripted group (container) (typed FeaturePython)
  Dunit = g/cm3
  Dvalue = 1.625
  Group = -> [C_element109,Cl_element025]
  conduct = 2
  density = 1
  expand = 3
  formula = G4_TETRACHLOROETHYLENE
  name = G4_TETRACHLOROETHYLENE
  specific = 4
FEATURE [App::DocumentObjectGroupPython] Tl_element001  label="Tl_element : 1"  # scripted group (container) (typed FeaturePython)
  n = 1
  ref = Tl_element
FEATURE [App::DocumentObjectGroupPython] Cl_element026  label="Cl_element : 013"  # scripted group (container) (typed FeaturePython)
  n = 1
  ref = Cl_element
FEATURE [App::DocumentObjectGroupPython] G4_THALLIUM_CHLORIDE  # scripted group (container) (typed FeaturePython)
  Dunit = g/cm3
  Dvalue = 7.004
  Group = -> [Tl_element001,Cl_element026]
  conduct = 2
  density = 1
  expand = 3
  formula = G4_THALLIUM_CHLORIDE
  name = G4_THALLIUM_CHLORIDE
  specific = 4
FEATURE [App::DocumentObjectGroupPython] H_element100  label="H_element : 0.147"  # scripted group (container) (typed FeaturePython)
  n = 0.105
FEATURE [App::DocumentObjectGroupPython] C_element110  label="C_element : 0.256"  # scripted group (container) (typed FeaturePython)
  n = 0.256
FEATURE [App::DocumentObjectGroupPython] N_element042  label="N_element : 0.760"  # scripted group (container) (typed FeaturePython)
  n = 0.027
FEATURE [App::DocumentObjectGroupPython] O_element094  label="O_element : 0.602"  # scripted group (container) (typed FeaturePython)
  n = 0.602
FEATURE [App::DocumentObjectGroupPython] Na_element019  label="Na_element : 0.102"  # scripted group (container) (typed FeaturePython)
  n = 0.001
FEATURE [App::DocumentObjectGroupPython] P_element011  label="P_element : 0.109"  # scripted group (container) (typed FeaturePython)
  n = 0.002
FEATURE [App::DocumentObjectGroupPython] S_element022  label="S_element : 0.023"  # scripted group (container) (typed FeaturePython)
  n = 0.003
FEATURE [App::DocumentObjectGroupPython] Cl_element027  label="Cl_element : 0.591"  # scripted group (container) (typed FeaturePython)
  n = 0.002
FEATURE [App::DocumentObjectGroupPython] K_element012  label="K_element : 0.018"  # scripted group (container) (typed FeaturePython)
  n = 0.002
FEATURE [App::DocumentObjectGroupPython] G4_TISSUE_SOFT_ICRP  # scripted group (container) (typed FeaturePython)
  Dunit = g/cm3
  Dvalue = 1.03
  Group = -> [H_element100,C_element110,N_element042,O_element094,Na_element019,P_element011,S_element022,Cl_element027,K_element012]
  conduct = 2
  density = 1
  expand = 3
  formula = G4_TISSUE_SOFT_ICRP
  name = G4_TISSUE_SOFT_ICRP
  specific = 4
FEATURE [App::DocumentObjectGroupPython] H_element101  label="H_element : 0.148"  # scripted group (container) (typed FeaturePython)
  n = 0.101
FEATURE [App::DocumentObjectGroupPython] C_element111  label="C_element : 0.111"  # scripted group (container) (typed FeaturePython)
  n = 0.111
FEATURE [App::DocumentObjectGroupPython] N_element043  label="N_element : 0.026"  # scripted group (container) (typed FeaturePython)
  n = 0.026
FEATURE [App::DocumentObjectGroupPython] O_element095  label="O_element : 0.762"  # scripted group (container) (typed FeaturePython)
  n = 0.762
FEATURE [App::DocumentObjectGroupPython] G4_TISSUE_SOFT_ICRU_4  label="G4_TISSUE_SOFT_ICRU-4"  # scripted group (container) (typed FeaturePython)
  Dunit = g/cm3
  Dvalue = 1
  Group = -> [H_element101,C_element111,N_element043,O_element095]
  conduct = 2
  density = 1
  expand = 3
  formula = G4_TISSUE_SOFT_ICRU-4
  name = G4_TISSUE_SOFT_ICRU-4
  specific = 4
FEATURE [App::DocumentObjectGroupPython] H_element102  label="H_element : 0.149"  # scripted group (container) (typed FeaturePython)
  n = 0.101869
FEATURE [App::DocumentObjectGroupPython] C_element112  label="C_element : 0.456"  # scripted group (container) (typed FeaturePython)
  n = 0.456179
FEATURE [App::DocumentObjectGroupPython] N_element044  label="N_element : 0.761"  # scripted group (container) (typed FeaturePython)
  n = 0.035172
FEATURE [App::DocumentObjectGroupPython] O_element096  label="O_element : 0.407"  # scripted group (container) (typed FeaturePython)
  n = 0.40678
FEATURE [App::DocumentObjectGroupPython] G4_TISSUE_METHANE  label="G4_TISSUE-METHANE"  # scripted group (container) (typed FeaturePython)
  Dunit = g/cm3
  Dvalue = 0.00106409
  Group = -> [H_element102,C_element112,N_element044,O_element096]
  conduct = 2
  density = 1
  expand = 3
  formula = G4_TISSUE-METHANE
  name = G4_TISSUE-METHANE
  specific = 4
FEATURE [App::DocumentObjectGroupPython] H_element103  label="H_element : 0.103"  # scripted group (container) (typed FeaturePython)
  n = 0.102672
FEATURE [App::DocumentObjectGroupPython] C_element113  label="C_element : 0.569"  # scripted group (container) (typed FeaturePython)
  n = 0.56894
FEATURE [App::DocumentObjectGroupPython] N_element045  label="N_element : 0.762"  # scripted group (container) (typed FeaturePython)
  n = 0.035022
FEATURE [App::DocumentObjectGroupPython] O_element097  label="O_element : 0.293"  # scripted group (container) (typed FeaturePython)
  n = 0.293366
FEATURE [App::DocumentObjectGroupPython] G4_TISSUE_PROPANE  label="G4_TISSUE-PROPANE"  # scripted group (container) (typed FeaturePython)
  Dunit = g/cm3
  Dvalue = 0.00182628
  Group = -> [H_element103,C_element113,N_element045,O_element097]
  conduct = 2
  density = 1
  expand = 3
  formula = G4_TISSUE-PROPANE
  name = G4_TISSUE-PROPANE
  specific = 4
FEATURE [App::DocumentObjectGroupPython] Ti_element003  label="Ti_element : 1"  # scripted group (container) (typed FeaturePython)
  n = 1
  ref = Ti_element
FEATURE [App::DocumentObjectGroupPython] O_element098  label="O_element : 052"  # scripted group (container) (typed FeaturePython)
  n = 2
  ref = O_element
FEATURE [App::DocumentObjectGroupPython] G4_TITANIUM_DIOXIDE  # scripted group (container) (typed FeaturePython)
  Dunit = g/cm3
  Dvalue = 4.26
  Group = -> [Ti_element003,O_element098]
  conduct = 2
  density = 1
  expand = 3
  formula = G4_TITANIUM_DIOXIDE
  name = G4_TITANIUM_DIOXIDE
  specific = 4
FEATURE [App::DocumentObjectGroupPython] C_element114  label="C_element : 061"  # scripted group (container) (typed FeaturePython)
  n = 7
  ref = C_element
FEATURE [App::DocumentObjectGroupPython] H_element104  label="H_element : 055"  # scripted group (container) (typed FeaturePython)
  n = 8
  ref = H_element
FEATURE [App::DocumentObjectGroupPython] G4_TOLUENE  # scripted group (container) (typed FeaturePython)
  Dunit = g/cm3
  Dvalue = 0.8669
  Group = -> [C_element114,H_element104]
  conduct = 2
  density = 1
  expand = 3
  formula = G4_TOLUENE
  name = G4_TOLUENE
  specific = 4
FEATURE [App::DocumentObjectGroupPython] C_element115  label="C_element : 062"  # scripted group (container) (typed FeaturePython)
  n = 2
  ref = C_element
FEATURE [App::DocumentObjectGroupPython] H_element105  label="H_element : 056"  # scripted group (container) (typed FeaturePython)
  n = 1
  ref = H_element
FEATURE [App::DocumentObjectGroupPython] Cl_element028  label="Cl_element : 014"  # scripted group (container) (typed FeaturePython)
  n = 3
  ref = Cl_element
FEATURE [App::DocumentObjectGroupPython] G4_TRICHLOROETHYLENE  # scripted group (container) (typed FeaturePython)
  Dunit = g/cm3
  Dvalue = 1.46
  Group = -> [C_element115,H_element105,Cl_element028]
  conduct = 2
  density = 1
  expand = 3
  formula = G4_TRICHLOROETHYLENE
  name = G4_TRICHLOROETHYLENE
  specific = 4
FEATURE [App::DocumentObjectGroupPython] C_element116  label="C_element : 063"  # scripted group (container) (typed FeaturePython)
  n = 6
  ref = C_element
FEATURE [App::DocumentObjectGroupPython] H_element106  label="H_element : 15"  # scripted group (container) (typed FeaturePython)
  n = 15
  ref = H_element
FEATURE [App::DocumentObjectGroupPython] O_element099  label="O_element : 053"  # scripted group (container) (typed FeaturePython)
  n = 4
  ref = O_element
FEATURE [App::DocumentObjectGroupPython] P_element012  label="P_element : 1"  # scripted group (container) (typed FeaturePython)
  n = 1
  ref = P_element
FEATURE [App::DocumentObjectGroupPython] G4_TRIETHYL_PHOSPHATE  # scripted group (container) (typed FeaturePython)
  Dunit = g/cm3
  Dvalue = 1.07
  Group = -> [C_element116,H_element106,O_element099,P_element012]
  conduct = 2
  density = 1
  expand = 3
  formula = G4_TRIETHYL_PHOSPHATE
  name = G4_TRIETHYL_PHOSPHATE
  specific = 4
FEATURE [App::DocumentObjectGroupPython] W_element003  label="W_element : 003"  # scripted group (container) (typed FeaturePython)
  n = 1
  ref = W_element
FEATURE [App::DocumentObjectGroupPython] F_element017  label="F_element : 6"  # scripted group (container) (typed FeaturePython)
  n = 6
  ref = F_element
FEATURE [App::DocumentObjectGroupPython] G4_TUNGSTEN_HEXAFLUORIDE  # scripted group (container) (typed FeaturePython)
  Dunit = g/cm3
  Dvalue = 2.4
  Group = -> [W_element003,F_element017]
  conduct = 2
  density = 1
  expand = 3
  formula = G4_TUNGSTEN_HEXAFLUORIDE
  name = G4_TUNGSTEN_HEXAFLUORIDE
  specific = 4
FEATURE [App::DocumentObjectGroupPython] U_element001  label="U_element : 1"  # scripted group (container) (typed FeaturePython)
  n = 1
  ref = U_element
FEATURE [App::DocumentObjectGroupPython] C_element117  label="C_element : 064"  # scripted group (container) (typed FeaturePython)
  n = 2
  ref = C_element
FEATURE [App::DocumentObjectGroupPython] G4_URANIUM_DICARBIDE  # scripted group (container) (typed FeaturePython)
  Dunit = g/cm3
  Dvalue = 11.28
  Group = -> [U_element001,C_element117]
  conduct = 2
  density = 1
  expand = 3
  formula = G4_URANIUM_DICARBIDE
  name = G4_URANIUM_DICARBIDE
  specific = 4
FEATURE [App::DocumentObjectGroupPython] U_element002  label="U_element : 002"  # scripted group (container) (typed FeaturePython)
  n = 1
  ref = U_element
FEATURE [App::DocumentObjectGroupPython] C_element118  label="C_element : 065"  # scripted group (container) (typed FeaturePython)
  n = 1
  ref = C_element
FEATURE [App::DocumentObjectGroupPython] G4_URANIUM_MONOCARBIDE  # scripted group (container) (typed FeaturePython)
  Dunit = g/cm3
  Dvalue = 13.63
  Group = -> [U_element002,C_element118]
  conduct = 2
  density = 1
  expand = 3
  formula = G4_URANIUM_MONOCARBIDE
  name = G4_URANIUM_MONOCARBIDE
  specific = 4
FEATURE [App::DocumentObjectGroupPython] U_element003  label="U_element : 003"  # scripted group (container) (typed FeaturePython)
  n = 1
  ref = U_element
FEATURE [App::DocumentObjectGroupPython] O_element100  label="O_element : 054"  # scripted group (container) (typed FeaturePython)
  n = 2
  ref = O_element
FEATURE [App::DocumentObjectGroupPython] G4_URANIUM_OXIDE  # scripted group (container) (typed FeaturePython)
  Dunit = g/cm3
  Dvalue = 10.96
  Group = -> [U_element003,O_element100]
  conduct = 2
  density = 1
  expand = 3
  formula = G4_URANIUM_OXIDE
  name = G4_URANIUM_OXIDE
  specific = 4
FEATURE [App::DocumentObjectGroupPython] C_element119  label="C_element : 066"  # scripted group (container) (typed FeaturePython)
  n = 1
  ref = C_element
FEATURE [App::DocumentObjectGroupPython] H_element107  label="H_element : 057"  # scripted group (container) (typed FeaturePython)
  n = 4
  ref = H_element
FEATURE [App::DocumentObjectGroupPython] N_element046  label="N_element : 019"  # scripted group (container) (typed FeaturePython)
  n = 2
  ref = N_element
FEATURE [App::DocumentObjectGroupPython] O_element101  label="O_element : 055"  # scripted group (container) (typed FeaturePython)
  n = 1
  ref = O_element
FEATURE [App::DocumentObjectGroupPython] G4_UREA  # scripted group (container) (typed FeaturePython)
  Dunit = g/cm3
  Dvalue = 1.323
  Group = -> [C_element119,H_element107,N_element046,O_element101]
  conduct = 2
  density = 1
  expand = 3
  formula = G4_UREA
  name = G4_UREA
  specific = 4
FEATURE [App::DocumentObjectGroupPython] C_element120  label="C_element : 067"  # scripted group (container) (typed FeaturePython)
  n = 5
  ref = C_element
FEATURE [App::DocumentObjectGroupPython] H_element108  label="H_element : 058"  # scripted group (container) (typed FeaturePython)
  n = 11
  ref = H_element
FEATURE [App::DocumentObjectGroupPython] N_element047  label="N_element : 020"  # scripted group (container) (typed FeaturePython)
  n = 1
  ref = N_element
FEATURE [App::DocumentObjectGroupPython] O_element102  label="O_element : 056"  # scripted group (container) (typed FeaturePython)
  n = 2
  ref = O_element
FEATURE [App::DocumentObjectGroupPython] G4_VALINE  # scripted group (container) (typed FeaturePython)
  Dunit = g/cm3
  Dvalue = 1.23
  Group = -> [C_element120,H_element108,N_element047,O_element102]
  conduct = 2
  density = 1
  expand = 3
  formula = G4_VALINE
  name = G4_VALINE
  specific = 4
FEATURE [App::DocumentObjectGroupPython] H_element109  label="H_element : 0.009"  # scripted group (container) (typed FeaturePython)
  n = 0.009417
FEATURE [App::DocumentObjectGroupPython] C_element121  label="C_element : 0.281"  # scripted group (container) (typed FeaturePython)
  n = 0.280555
FEATURE [App::DocumentObjectGroupPython] F_element018  label="F_element : 0.710"  # scripted group (container) (typed FeaturePython)
  n = 0.710028
FEATURE [App::DocumentObjectGroupPython] G4_VITON  # scripted group (container) (typed FeaturePython)
  Dunit = g/cm3
  Dvalue = 1.8
  Group = -> [H_element109,C_element121,F_element018]
  conduct = 2
  density = 1
  expand = 3
  formula = G4_VITON
  name = G4_VITON
  specific = 4
FEATURE [App::DocumentObjectGroupPython] H_element110  label="H_element : 059"  # scripted group (container) (typed FeaturePython)
  n = 2
  ref = H_element
FEATURE [App::DocumentObjectGroupPython] O_element103  label="O_element : 057"  # scripted group (container) (typed FeaturePython)
  n = 1
  ref = O_element
FEATURE [App::DocumentObjectGroupPython] G4_WATER  # scripted group (container) (typed FeaturePython)
  Dunit = g/cm3
  Dvalue = 1
  Group = -> [H_element110,O_element103]
  conduct = 2
  density = 1
  expand = 3
  formula = G4_WATER
  name = G4_WATER
  specific = 4
FEATURE [App::DocumentObjectGroupPython] H_element111  label="H_element : 060"  # scripted group (container) (typed FeaturePython)
  n = 2
  ref = H_element
FEATURE [App::DocumentObjectGroupPython] O_element104  label="O_element : 058"  # scripted group (container) (typed FeaturePython)
  n = 1
  ref = O_element
FEATURE [App::DocumentObjectGroupPython] G4_WATER_VAPOR  # scripted group (container) (typed FeaturePython)
  Dunit = g/cm3
  Dvalue = 0.000756182
  Group = -> [H_element111,O_element104]
  conduct = 2
  density = 1
  expand = 3
  formula = G4_WATER_VAPOR
  name = G4_WATER_VAPOR
  specific = 4
FEATURE [App::DocumentObjectGroupPython] C_element122  label="C_element : 068"  # scripted group (container) (typed FeaturePython)
  n = 8
  ref = C_element
FEATURE [App::DocumentObjectGroupPython] H_element112  label="H_element : 061"  # scripted group (container) (typed FeaturePython)
  n = 10
  ref = H_element
FEATURE [App::DocumentObjectGroupPython] G4_XYLENE  # scripted group (container) (typed FeaturePython)
  Dunit = g/cm3
  Dvalue = 0.87
  Group = -> [C_element122,H_element112]
  conduct = 2
  density = 1
  expand = 3
  formula = G4_XYLENE
  name = G4_XYLENE
  specific = 4
FEATURE [App::DocumentObjectGroupPython] C_element123  label="C_element : 069"  # scripted group (container) (typed FeaturePython)
  n = 1
  ref = C_element
FEATURE [App::DocumentObjectGroupPython] G4_GRAPHITE  # scripted group (container) (typed FeaturePython)
  Dunit = g/cm3
  Dvalue = 2.21
  Group = -> [C_element123]
  conduct = 2
  density = 1
  expand = 3
  formula = G4_GRAPHITE
  name = G4_GRAPHITE
  specific = 4
FEATURE [App::DocumentObjectGroupPython] NIST  # scripted group (container) (typed FeaturePython)
  Group = -> [G4_A_150_TISSUE,G4_ACETONE,G4_ACETYLENE,G4_ADENINE,G4_ADIPOSE_TISSUE_ICRP,G4_AIR,G4_ALANINE,G4_ALUMINUM_OXIDE,G4_AMBER,G4_AMMONIA,G4_ANILINE,G4_ANTHRACENE,G4_B_100_BONE,G4_BAKELITE,G4_BARIUM_FLUORIDE,G4_BARIUM_SULFATE,G4_BENZENE,G4_BERYLLIUM_OXIDE,G4_BGO,G4_BLOOD_ICRP,G4_BONE_COMPACT_ICRU,G4_BONE_CORTICAL_ICRP,G4_BORON_CARBIDE,G4_BORON_OXIDE,G4_BRAIN_ICRP,G4_BUTANE,G4_N_BUTYL_ALCOHOL,G4_C_552,+152 more]
FEATURE [App::DocumentObjectGroupPython] H_element113  label="H_element : 062"  # scripted group (container) (typed FeaturePython)
  n = 1
  ref = H_element
FEATURE [App::DocumentObjectGroupPython] G4_H  # scripted group (container) (typed FeaturePython)
  Dunit = g/cm3
  Dvalue = 8.3748e-05
  Group = -> [H_element113]
  conduct = 2
  density = 1
  expand = 3
  formula = H
  name = G4_H
  specific = 4
FEATURE [App::DocumentObjectGroupPython] He_element001  label="He_element : 1"  # scripted group (container) (typed FeaturePython)
  n = 1
  ref = He_element
FEATURE [App::DocumentObjectGroupPython] G4_He  # scripted group (container) (typed FeaturePython)
  Dunit = g/cm3
  Dvalue = 0.000166322
  Group = -> [He_element001]
  conduct = 2
  density = 1
  expand = 3
  formula = He
  name = G4_He
  specific = 4
FEATURE [App::DocumentObjectGroupPython] Li_element008  label="Li_element : 008"  # scripted group (container) (typed FeaturePython)
  n = 1
  ref = Li_element
FEATURE [App::DocumentObjectGroupPython] G4_Li  # scripted group (container) (typed FeaturePython)
  Dunit = g/cm3
  Dvalue = 0.534
  Group = -> [Li_element008]
  conduct = 2
  density = 1
  expand = 3
  formula = Li
  name = G4_Li
  specific = 4
FEATURE [App::DocumentObjectGroupPython] Be_element002  label="Be_element : 002"  # scripted group (container) (typed FeaturePython)
  n = 1
  ref = Be_element
FEATURE [App::DocumentObjectGroupPython] G4_Be  # scripted group (container) (typed FeaturePython)
  Dunit = g/cm3
  Dvalue = 1.848
  Group = -> [Be_element002]
  conduct = 2
  density = 1
  expand = 3
  formula = Be
  name = G4_Be
  specific = 4
FEATURE [App::DocumentObjectGroupPython] B_element007  label="B_element : 007"  # scripted group (container) (typed FeaturePython)
  n = 1
  ref = B_element
FEATURE [App::DocumentObjectGroupPython] G4_B  # scripted group (container) (typed FeaturePython)
  Dunit = g/cm3
  Dvalue = 2.37
  Group = -> [B_element007]
  conduct = 2
  density = 1
  expand = 3
  formula = B
  name = G4_B
  specific = 4
FEATURE [App::DocumentObjectGroupPython] C_element124  label="C_element : 070"  # scripted group (container) (typed FeaturePython)
  n = 1
  ref = C_element
FEATURE [App::DocumentObjectGroupPython] G4_C  # scripted group (container) (typed FeaturePython)
  Dunit = g/cm3
  Dvalue = 2
  Group = -> [C_element124]
  conduct = 2
  density = 1
  expand = 3
  formula = C
  name = G4_C
  specific = 4
FEATURE [App::DocumentObjectGroupPython] N_element048  label="N_element : 021"  # scripted group (container) (typed FeaturePython)
  n = 1
  ref = N_element
FEATURE [App::DocumentObjectGroupPython] G4_N  # scripted group (container) (typed FeaturePython)
  Dunit = g/cm3
  Dvalue = 0.0011652
  Group = -> [N_element048]
  conduct = 2
  density = 1
  expand = 3
  formula = N
  name = G4_N
  specific = 4
FEATURE [App::DocumentObjectGroupPython] O_element105  label="O_element : 059"  # scripted group (container) (typed FeaturePython)
  n = 1
  ref = O_element
FEATURE [App::DocumentObjectGroupPython] G4_O  # scripted group (container) (typed FeaturePython)
  Dunit = g/cm3
  Dvalue = 0.00133151
  Group = -> [O_element105]
  conduct = 2
  density = 1
  expand = 3
  formula = O
  name = G4_O
  specific = 4
FEATURE [App::DocumentObjectGroupPython] F_element019  label="F_element : 008"  # scripted group (container) (typed FeaturePython)
  n = 1
  ref = F_element
FEATURE [App::DocumentObjectGroupPython] G4_F  # scripted group (container) (typed FeaturePython)
  Dunit = g/cm3
  Dvalue = 0.00158029
  Group = -> [F_element019]
  conduct = 2
  density = 1
  expand = 3
  formula = F
  name = G4_F
  specific = 4
FEATURE [App::DocumentObjectGroupPython] Ne_element001  label="Ne_element : 1"  # scripted group (container) (typed FeaturePython)
  n = 1
  ref = Ne_element
FEATURE [App::DocumentObjectGroupPython] G4_Ne  # scripted group (container) (typed FeaturePython)
  Dunit = g/cm3
  Dvalue = 0.000838505
  Group = -> [Ne_element001]
  conduct = 2
  density = 1
  expand = 3
  formula = Ne
  name = G4_Ne
  specific = 4
FEATURE [App::DocumentObjectGroupPython] Na_element020  label="Na_element : 005"  # scripted group (container) (typed FeaturePython)
  n = 1
  ref = Na_element
FEATURE [App::DocumentObjectGroupPython] G4_Na  # scripted group (container) (typed FeaturePython)
  Dunit = g/cm3
  Dvalue = 0.971
  Group = -> [Na_element020]
  conduct = 2
  density = 1
  expand = 3
  formula = Na
  name = G4_Na
  specific = 4
FEATURE [App::DocumentObjectGroupPython] Mg_element011  label="Mg_element : 005"  # scripted group (container) (typed FeaturePython)
  n = 1
  ref = Mg_element
FEATURE [App::DocumentObjectGroupPython] G4_Mg  # scripted group (container) (typed FeaturePython)
  Dunit = g/cm3
  Dvalue = 1.74
  Group = -> [Mg_element011]
  conduct = 2
  density = 1
  expand = 3
  formula = Mg
  name = G4_Mg
  specific = 4
FEATURE [App::DocumentObjectGroupPython] Al_element004  label="Al_element : 1"  # scripted group (container) (typed FeaturePython)
  n = 1
  ref = Al_element
FEATURE [App::DocumentObjectGroupPython] G4_Al  # scripted group (container) (typed FeaturePython)
  Dunit = g/cm3
  Dvalue = 2.699
  Group = -> [Al_element004]
  conduct = 2
  density = 1
  expand = 3
  formula = Al
  name = G4_Al
  specific = 4
FEATURE [App::DocumentObjectGroupPython] Si_element007  label="Si_element : 002"  # scripted group (container) (typed FeaturePython)
  n = 1
  ref = Si_element
FEATURE [App::DocumentObjectGroupPython] G4_Si  # scripted group (container) (typed FeaturePython)
  Dunit = g/cm3
  Dvalue = 2.33
  Group = -> [Si_element007]
  conduct = 2
  density = 1
  expand = 3
  formula = Si
  name = G4_Si
  specific = 4
FEATURE [App::DocumentObjectGroupPython] P_element013  label="P_element : 002"  # scripted group (container) (typed FeaturePython)
  n = 1
  ref = P_element
FEATURE [App::DocumentObjectGroupPython] G4_P  # scripted group (container) (typed FeaturePython)
  Dunit = g/cm3
  Dvalue = 2.2
  Group = -> [P_element013]
  conduct = 2
  density = 1
  expand = 3
  formula = P
  name = G4_P
  specific = 4
FEATURE [App::DocumentObjectGroupPython] S_element023  label="S_element : 007"  # scripted group (container) (typed FeaturePython)
  n = 1
  ref = S_element
FEATURE [App::DocumentObjectGroupPython] G4_S  # scripted group (container) (typed FeaturePython)
  Dunit = g/cm3
  Dvalue = 2
  Group = -> [S_element023]
  conduct = 2
  density = 1
  expand = 3
  formula = S
  name = G4_S
  specific = 4
FEATURE [App::DocumentObjectGroupPython] Cl_element029  label="Cl_element : 015"  # scripted group (container) (typed FeaturePython)
  n = 1
  ref = Cl_element
FEATURE [App::DocumentObjectGroupPython] G4_Cl  # scripted group (container) (typed FeaturePython)
  Dunit = g/cm3
  Dvalue = 0.00299473
  Group = -> [Cl_element029]
  conduct = 2
  density = 1
  expand = 3
  formula = Cl
  name = G4_Cl
  specific = 4
FEATURE [App::DocumentObjectGroupPython] Ar_element002  label="Ar_element : 1"  # scripted group (container) (typed FeaturePython)
  n = 1
  ref = Ar_element
FEATURE [App::DocumentObjectGroupPython] G4_Ar  # scripted group (container) (typed FeaturePython)
  Dunit = g/cm3
  Dvalue = 0.00166201
  Group = -> [Ar_element002]
  conduct = 2
  density = 1
  expand = 3
  formula = Ar
  name = G4_Ar
  specific = 4
FEATURE [App::DocumentObjectGroupPython] K_element013  label="K_element : 003"  # scripted group (container) (typed FeaturePython)
  n = 1
  ref = K_element
FEATURE [App::DocumentObjectGroupPython] G4_K  # scripted group (container) (typed FeaturePython)
  Dunit = g/cm3
  Dvalue = 0.862
  Group = -> [K_element013]
  conduct = 2
  density = 1
  expand = 3
  formula = K
  name = G4_K
  specific = 4
FEATURE [App::DocumentObjectGroupPython] Ca_element014  label="Ca_element : 007"  # scripted group (container) (typed FeaturePython)
  n = 1
  ref = Ca_element
FEATURE [App::DocumentObjectGroupPython] G4_Ca  # scripted group (container) (typed FeaturePython)
  Dunit = g/cm3
  Dvalue = 1.55
  Group = -> [Ca_element014]
  conduct = 2
  density = 1
  expand = 3
  formula = Ca
  name = G4_Ca
  specific = 4
FEATURE [App::DocumentObjectGroupPython] Sc_element001  label="Sc_element : 1"  # scripted group (container) (typed FeaturePython)
  n = 1
  ref = Sc_element
FEATURE [App::DocumentObjectGroupPython] G4_Sc  # scripted group (container) (typed FeaturePython)
  Dunit = g/cm3
  Dvalue = 2.989
  Group = -> [Sc_element001]
  conduct = 2
  density = 1
  expand = 3
  formula = Sc
  name = G4_Sc
  specific = 4
FEATURE [App::DocumentObjectGroupPython] Ti_element004  label="Ti_element : 002"  # scripted group (container) (typed FeaturePython)
  n = 1
  ref = Ti_element
FEATURE [App::DocumentObjectGroupPython] G4_Ti  # scripted group (container) (typed FeaturePython)
  Dunit = g/cm3
  Dvalue = 4.54
  Group = -> [Ti_element004]
  conduct = 2
  density = 1
  expand = 3
  formula = Ti
  name = G4_Ti
  specific = 4
FEATURE [App::DocumentObjectGroupPython] V_element001  label="V_element : 1"  # scripted group (container) (typed FeaturePython)
  n = 1
  ref = V_element
FEATURE [App::DocumentObjectGroupPython] G4_V  # scripted group (container) (typed FeaturePython)
  Dunit = g/cm3
  Dvalue = 6.11
  Group = -> [V_element001]
  conduct = 2
  density = 1
  expand = 3
  formula = V
  name = G4_V
  specific = 4
FEATURE [App::DocumentObjectGroupPython] Cr_element001  label="Cr_element : 1"  # scripted group (container) (typed FeaturePython)
  n = 1
  ref = Cr_element
FEATURE [App::DocumentObjectGroupPython] G4_Cr  # scripted group (container) (typed FeaturePython)
  Dunit = g/cm3
  Dvalue = 7.18
  Group = -> [Cr_element001]
  conduct = 2
  density = 1
  expand = 3
  formula = Cr
  name = G4_Cr
  specific = 4
FEATURE [App::DocumentObjectGroupPython] Mn_element001  label="Mn_element : 1"  # scripted group (container) (typed FeaturePython)
  n = 1
  ref = Mn_element
FEATURE [App::DocumentObjectGroupPython] G4_Mn  # scripted group (container) (typed FeaturePython)
  Dunit = g/cm3
  Dvalue = 7.44
  Group = -> [Mn_element001]
  conduct = 2
  density = 1
  expand = 3
  formula = Mn
  name = G4_Mn
  specific = 4
FEATURE [App::DocumentObjectGroupPython] Fe_element007  label="Fe_element : 004"  # scripted group (container) (typed FeaturePython)
  n = 1
  ref = Fe_element
FEATURE [App::DocumentObjectGroupPython] G4_Fe  # scripted group (container) (typed FeaturePython)
  Dunit = g/cm3
  Dvalue = 7.874
  Group = -> [Fe_element007]
  conduct = 2
  density = 1
  expand = 3
  formula = Fe
  name = G4_Fe
  specific = 4
FEATURE [App::DocumentObjectGroupPython] Co_element001  label="Co_element : 1"  # scripted group (container) (typed FeaturePython)
  n = 1
  ref = Co_element
FEATURE [App::DocumentObjectGroupPython] G4_Co  # scripted group (container) (typed FeaturePython)
  Dunit = g/cm3
  Dvalue = 8.9
  Group = -> [Co_element001]
  conduct = 2
  density = 1
  expand = 3
  formula = Co
  name = G4_Co
  specific = 4
FEATURE [App::DocumentObjectGroupPython] Ni_element001  label="Ni_element : 1"  # scripted group (container) (typed FeaturePython)
  n = 1
  ref = Ni_element
FEATURE [App::DocumentObjectGroupPython] G4_Ni  # scripted group (container) (typed FeaturePython)
  Dunit = g/cm3
  Dvalue = 8.902
  Group = -> [Ni_element001]
  conduct = 2
  density = 1
  expand = 3
  formula = Ni
  name = G4_Ni
  specific = 4
FEATURE [App::DocumentObjectGroupPython] Cu_element001  label="Cu_element : 1"  # scripted group (container) (typed FeaturePython)
  n = 1
  ref = Cu_element
FEATURE [App::DocumentObjectGroupPython] G4_Cu  # scripted group (container) (typed FeaturePython)
  Dunit = g/cm3
  Dvalue = 8.96
  Group = -> [Cu_element001]
  conduct = 2
  density = 1
  expand = 3
  formula = Cu
  name = G4_Cu
  specific = 4
FEATURE [App::DocumentObjectGroupPython] Zn_element001  label="Zn_element : 1"  # scripted group (container) (typed FeaturePython)
  n = 1
  ref = Zn_element
FEATURE [App::DocumentObjectGroupPython] G4_Zn  # scripted group (container) (typed FeaturePython)
  Dunit = g/cm3
  Dvalue = 7.133
  Group = -> [Zn_element001]
  conduct = 2
  density = 1
  expand = 3
  formula = Zn
  name = G4_Zn
  specific = 4
FEATURE [App::DocumentObjectGroupPython] Ga_element002  label="Ga_element : 002"  # scripted group (container) (typed FeaturePython)
  n = 1
  ref = Ga_element
FEATURE [App::DocumentObjectGroupPython] G4_Ga  # scripted group (container) (typed FeaturePython)
  Dunit = g/cm3
  Dvalue = 5.904
  Group = -> [Ga_element002]
  conduct = 2
  density = 1
  expand = 3
  formula = Ga
  name = G4_Ga
  specific = 4
FEATURE [App::DocumentObjectGroupPython] Ge_element002  label="Ge_element : 1"  # scripted group (container) (typed FeaturePython)
  n = 1
  ref = Ge_element
FEATURE [App::DocumentObjectGroupPython] G4_Ge  # scripted group (container) (typed FeaturePython)
  Dunit = g/cm3
  Dvalue = 5.323
  Group = -> [Ge_element002]
  conduct = 2
  density = 1
  expand = 3
  formula = Ge
  name = G4_Ge
  specific = 4
FEATURE [App::DocumentObjectGroupPython] As_element003  label="As_element : 002"  # scripted group (container) (typed FeaturePython)
  n = 1
  ref = As_element
FEATURE [App::DocumentObjectGroupPython] G4_As  # scripted group (container) (typed FeaturePython)
  Dunit = g/cm3
  Dvalue = 5.73
  Group = -> [As_element003]
  conduct = 2
  density = 1
  expand = 3
  formula = As
  name = G4_As
  specific = 4
FEATURE [App::DocumentObjectGroupPython] Se_element001  label="Se_element : 1"  # scripted group (container) (typed FeaturePython)
  n = 1
  ref = Se_element
FEATURE [App::DocumentObjectGroupPython] G4_Se  # scripted group (container) (typed FeaturePython)
  Dunit = g/cm3
  Dvalue = 4.5
  Group = -> [Se_element001]
  conduct = 2
  density = 1
  expand = 3
  formula = Se
  name = G4_Se
  specific = 4
FEATURE [App::DocumentObjectGroupPython] Br_element007  label="Br_element : 004"  # scripted group (container) (typed FeaturePython)
  n = 1
  ref = Br_element
FEATURE [App::DocumentObjectGroupPython] G4_Br  # scripted group (container) (typed FeaturePython)
  Dunit = g/cm3
  Dvalue = 0.0070721
  Group = -> [Br_element007]
  conduct = 2
  density = 1
  expand = 3
  formula = Br
  name = G4_Br
  specific = 4
FEATURE [App::DocumentObjectGroupPython] Kr_element001  label="Kr_element : 1"  # scripted group (container) (typed FeaturePython)
  n = 1
  ref = Kr_element
FEATURE [App::DocumentObjectGroupPython] G4_Kr  # scripted group (container) (typed FeaturePython)
  Dunit = g/cm3
  Dvalue = 0.00347832
  Group = -> [Kr_element001]
  conduct = 2
  density = 1
  expand = 3
  formula = Kr
  name = G4_Kr
  specific = 4
FEATURE [App::DocumentObjectGroupPython] Rb_element001  label="Rb_element : 1"  # scripted group (container) (typed FeaturePython)
  n = 1
  ref = Rb_element
FEATURE [App::DocumentObjectGroupPython] G4_Rb  # scripted group (container) (typed FeaturePython)
  Dunit = g/cm3
  Dvalue = 1.532
  Group = -> [Rb_element001]
  conduct = 2
  density = 1
  expand = 3
  formula = Rb
  name = G4_Rb
  specific = 4
FEATURE [App::DocumentObjectGroupPython] Sr_element001  label="Sr_element : 1"  # scripted group (container) (typed FeaturePython)
  n = 1
  ref = Sr_element
FEATURE [App::DocumentObjectGroupPython] G4_Sr  # scripted group (container) (typed FeaturePython)
  Dunit = g/cm3
  Dvalue = 2.54
  Group = -> [Sr_element001]
  conduct = 2
  density = 1
  expand = 3
  formula = Sr
  name = G4_Sr
  specific = 4
FEATURE [App::DocumentObjectGroupPython] Y_element001  label="Y_element : 1"  # scripted group (container) (typed FeaturePython)
  n = 1
  ref = Y_element
FEATURE [App::DocumentObjectGroupPython] G4_Y  # scripted group (container) (typed FeaturePython)
  Dunit = g/cm3
  Dvalue = 4.469
  Group = -> [Y_element001]
  conduct = 2
  density = 1
  expand = 3
  formula = Y
  name = G4_Y
  specific = 4
FEATURE [App::DocumentObjectGroupPython] Zr_element001  label="Zr_element : 1"  # scripted group (container) (typed FeaturePython)
  n = 1
  ref = Zr_element
FEATURE [App::DocumentObjectGroupPython] G4_Zr  # scripted group (container) (typed FeaturePython)
  Dunit = g/cm3
  Dvalue = 6.506
  Group = -> [Zr_element001]
  conduct = 2
  density = 1
  expand = 3
  formula = Zr
  name = G4_Zr
  specific = 4
FEATURE [App::DocumentObjectGroupPython] Nb_element001  label="Nb_element : 1"  # scripted group (container) (typed FeaturePython)
  n = 1
  ref = Nb_element
FEATURE [App::DocumentObjectGroupPython] G4_Nb  # scripted group (container) (typed FeaturePython)
  Dunit = g/cm3
  Dvalue = 8.57
  Group = -> [Nb_element001]
  conduct = 2
  density = 1
  expand = 3
  formula = Nb
  name = G4_Nb
  specific = 4
FEATURE [App::DocumentObjectGroupPython] Mo_element001  label="Mo_element : 1"  # scripted group (container) (typed FeaturePython)
  n = 1
  ref = Mo_element
FEATURE [App::DocumentObjectGroupPython] G4_Mo  # scripted group (container) (typed FeaturePython)
  Dunit = g/cm3
  Dvalue = 10.22
  Group = -> [Mo_element001]
  conduct = 2
  density = 1
  expand = 3
  formula = Mo
  name = G4_Mo
  specific = 4
FEATURE [App::DocumentObjectGroupPython] Tc_element001  label="Tc_element : 1"  # scripted group (container) (typed FeaturePython)
  n = 1
  ref = Tc_element
FEATURE [App::DocumentObjectGroupPython] G4_Tc  # scripted group (container) (typed FeaturePython)
  Dunit = g/cm3
  Dvalue = 11.5
  Group = -> [Tc_element001]
  conduct = 2
  density = 1
  expand = 3
  formula = Tc
  name = G4_Tc
  specific = 4
FEATURE [App::DocumentObjectGroupPython] Ru_element001  label="Ru_element : 1"  # scripted group (container) (typed FeaturePython)
  n = 1
  ref = Ru_element
FEATURE [App::DocumentObjectGroupPython] G4_Ru  # scripted group (container) (typed FeaturePython)
  Dunit = g/cm3
  Dvalue = 12.41
  Group = -> [Ru_element001]
  conduct = 2
  density = 1
  expand = 3
  formula = Ru
  name = G4_Ru
  specific = 4
FEATURE [App::DocumentObjectGroupPython] Rh_element001  label="Rh_element : 1"  # scripted group (container) (typed FeaturePython)
  n = 1
  ref = Rh_element
FEATURE [App::DocumentObjectGroupPython] G4_Rh  # scripted group (container) (typed FeaturePython)
  Dunit = g/cm3
  Dvalue = 12.41
  Group = -> [Rh_element001]
  conduct = 2
  density = 1
  expand = 3
  formula = Rh
  name = G4_Rh
  specific = 4
FEATURE [App::DocumentObjectGroupPython] Pd_element001  label="Pd_element : 1"  # scripted group (container) (typed FeaturePython)
  n = 1
  ref = Pd_element
FEATURE [App::DocumentObjectGroupPython] G4_Pd  # scripted group (container) (typed FeaturePython)
  Dunit = g/cm3
  Dvalue = 12.02
  Group = -> [Pd_element001]
  conduct = 2
  density = 1
  expand = 3
  formula = Pd
  name = G4_Pd
  specific = 4
FEATURE [App::DocumentObjectGroupPython] Ag_element006  label="Ag_element : 004"  # scripted group (container) (typed FeaturePython)
  n = 1
  ref = Ag_element
FEATURE [App::DocumentObjectGroupPython] G4_Ag  # scripted group (container) (typed FeaturePython)
  Dunit = g/cm3
  Dvalue = 10.5
  Group = -> [Ag_element006]
  conduct = 2
  density = 1
  expand = 3
  formula = Ag
  name = G4_Ag
  specific = 4
FEATURE [App::DocumentObjectGroupPython] Cd_element003  label="Cd_element : 003"  # scripted group (container) (typed FeaturePython)
  n = 1
  ref = Cd_element
FEATURE [App::DocumentObjectGroupPython] G4_Cd  # scripted group (container) (typed FeaturePython)
  Dunit = g/cm3
  Dvalue = 8.65
  Group = -> [Cd_element003]
  conduct = 2
  density = 1
  expand = 3
  formula = Cd
  name = G4_Cd
  specific = 4
FEATURE [App::DocumentObjectGroupPython] In_element001  label="In_element : 1"  # scripted group (container) (typed FeaturePython)
  n = 1
  ref = In_element
FEATURE [App::DocumentObjectGroupPython] G4_In  # scripted group (container) (typed FeaturePython)
  Dunit = g/cm3
  Dvalue = 7.31
  Group = -> [In_element001]
  conduct = 2
  density = 1
  expand = 3
  formula = In
  name = G4_In
  specific = 4
FEATURE [App::DocumentObjectGroupPython] Sn_element001  label="Sn_element : 1"  # scripted group (container) (typed FeaturePython)
  n = 1
  ref = Sn_element
FEATURE [App::DocumentObjectGroupPython] G4_Sn  # scripted group (container) (typed FeaturePython)
  Dunit = g/cm3
  Dvalue = 7.31
  Group = -> [Sn_element001]
  conduct = 2
  density = 1
  expand = 3
  formula = Sn
  name = G4_Sn
  specific = 4
FEATURE [App::DocumentObjectGroupPython] Sb_element001  label="Sb_element : 1"  # scripted group (container) (typed FeaturePython)
  n = 1
  ref = Sb_element
FEATURE [App::DocumentObjectGroupPython] G4_Sb  # scripted group (container) (typed FeaturePython)
  Dunit = g/cm3
  Dvalue = 6.691
  Group = -> [Sb_element001]
  conduct = 2
  density = 1
  expand = 3
  formula = Sb
  name = G4_Sb
  specific = 4
FEATURE [App::DocumentObjectGroupPython] Te_element002  label="Te_element : 002"  # scripted group (container) (typed FeaturePython)
  n = 1
  ref = Te_element
FEATURE [App::DocumentObjectGroupPython] G4_Te  # scripted group (container) (typed FeaturePython)
  Dunit = g/cm3
  Dvalue = 6.24
  Group = -> [Te_element002]
  conduct = 2
  density = 1
  expand = 3
  formula = Te
  name = G4_Te
  specific = 4
FEATURE [App::DocumentObjectGroupPython] I_element010  label="I_element : 006"  # scripted group (container) (typed FeaturePython)
  n = 1
  ref = I_element
FEATURE [App::DocumentObjectGroupPython] G4_I  # scripted group (container) (typed FeaturePython)
  Dunit = g/cm3
  Dvalue = 4.93
  Group = -> [I_element010]
  conduct = 2
  density = 1
  expand = 3
  formula = I
  name = G4_I
  specific = 4
FEATURE [App::DocumentObjectGroupPython] Xe_element001  label="Xe_element : 1"  # scripted group (container) (typed FeaturePython)
  n = 1
  ref = Xe_element
FEATURE [App::DocumentObjectGroupPython] G4_Xe  # scripted group (container) (typed FeaturePython)
  Dunit = g/cm3
  Dvalue = 0.00548536
  Group = -> [Xe_element001]
  conduct = 2
  density = 1
  expand = 3
  formula = Xe
  name = G4_Xe
  specific = 4
FEATURE [App::DocumentObjectGroupPython] Cs_element003  label="Cs_element : 003"  # scripted group (container) (typed FeaturePython)
  n = 1
  ref = Cs_element
FEATURE [App::DocumentObjectGroupPython] G4_Cs  # scripted group (container) (typed FeaturePython)
  Dunit = g/cm3
  Dvalue = 1.873
  Group = -> [Cs_element003]
  conduct = 2
  density = 1
  expand = 3
  formula = Cs
  name = G4_Cs
  specific = 4
FEATURE [App::DocumentObjectGroupPython] Ba_element003  label="Ba_element : 003"  # scripted group (container) (typed FeaturePython)
  n = 1
  ref = Ba_element
FEATURE [App::DocumentObjectGroupPython] G4_Ba  # scripted group (container) (typed FeaturePython)
  Dunit = g/cm3
  Dvalue = 3.5
  Group = -> [Ba_element003]
  conduct = 2
  density = 1
  expand = 3
  formula = Ba
  name = G4_Ba
  specific = 4
FEATURE [App::DocumentObjectGroupPython] La_element003  label="La_element : 003"  # scripted group (container) (typed FeaturePython)
  n = 1
  ref = La_element
FEATURE [App::DocumentObjectGroupPython] G4_La  # scripted group (container) (typed FeaturePython)
  Dunit = g/cm3
  Dvalue = 6.154
  Group = -> [La_element003]
  conduct = 2
  density = 1
  expand = 3
  formula = La
  name = G4_La
  specific = 4
FEATURE [App::DocumentObjectGroupPython] Ce_element002  label="Ce_element : 1"  # scripted group (container) (typed FeaturePython)
  n = 1
  ref = Ce_element
FEATURE [App::DocumentObjectGroupPython] G4_Ce  # scripted group (container) (typed FeaturePython)
  Dunit = g/cm3
  Dvalue = 6.657
  Group = -> [Ce_element002]
  conduct = 2
  density = 1
  expand = 3
  formula = Ce
  name = G4_Ce
  specific = 4
FEATURE [App::DocumentObjectGroupPython] Pr_element001  label="Pr_element : 1"  # scripted group (container) (typed FeaturePython)
  n = 1
  ref = Pr_element
FEATURE [App::DocumentObjectGroupPython] G4_Pr  # scripted group (container) (typed FeaturePython)
  Dunit = g/cm3
  Dvalue = 6.71
  Group = -> [Pr_element001]
  conduct = 2
  density = 1
  expand = 3
  formula = Pr
  name = G4_Pr
  specific = 4
FEATURE [App::DocumentObjectGroupPython] Nd_element001  label="Nd_element : 1"  # scripted group (container) (typed FeaturePython)
  n = 1
  ref = Nd_element
FEATURE [App::DocumentObjectGroupPython] G4_Nd  # scripted group (container) (typed FeaturePython)
  Dunit = g/cm3
  Dvalue = 6.9
  Group = -> [Nd_element001]
  conduct = 2
  density = 1
  expand = 3
  formula = Nd
  name = G4_Nd
  specific = 4
FEATURE [App::DocumentObjectGroupPython] Pm_element001  label="Pm_element : 1"  # scripted group (container) (typed FeaturePython)
  n = 1
  ref = Pm_element
FEATURE [App::DocumentObjectGroupPython] G4_Pm  # scripted group (container) (typed FeaturePython)
  Dunit = g/cm3
  Dvalue = 7.22
  Group = -> [Pm_element001]
  conduct = 2
  density = 1
  expand = 3
  formula = Pm
  name = G4_Pm
  specific = 4
FEATURE [App::DocumentObjectGroupPython] Sm_element001  label="Sm_element : 1"  # scripted group (container) (typed FeaturePython)
  n = 1
  ref = Sm_element
FEATURE [App::DocumentObjectGroupPython] G4_Sm  # scripted group (container) (typed FeaturePython)
  Dunit = g/cm3
  Dvalue = 7.46
  Group = -> [Sm_element001]
  conduct = 2
  density = 1
  expand = 3
  formula = Sm
  name = G4_Sm
  specific = 4
FEATURE [App::DocumentObjectGroupPython] Eu_element001  label="Eu_element : 1"  # scripted group (container) (typed FeaturePython)
  n = 1
  ref = Eu_element
FEATURE [App::DocumentObjectGroupPython] G4_Eu  # scripted group (container) (typed FeaturePython)
  Dunit = g/cm3
  Dvalue = 5.243
  Group = -> [Eu_element001]
  conduct = 2
  density = 1
  expand = 3
  formula = Eu
  name = G4_Eu
  specific = 4
FEATURE [App::DocumentObjectGroupPython] Gd_element002  label="Gd_element : 1"  # scripted group (container) (typed FeaturePython)
  n = 1
  ref = Gd_element
FEATURE [App::DocumentObjectGroupPython] G4_Gd  # scripted group (container) (typed FeaturePython)
  Dunit = g/cm3
  Dvalue = 7.9004
  Group = -> [Gd_element002]
  conduct = 2
  density = 1
  expand = 3
  formula = Gd
  name = G4_Gd
  specific = 4
FEATURE [App::DocumentObjectGroupPython] Tb_element001  label="Tb_element : 1"  # scripted group (container) (typed FeaturePython)
  n = 1
  ref = Tb_element
FEATURE [App::DocumentObjectGroupPython] G4_Tb  # scripted group (container) (typed FeaturePython)
  Dunit = g/cm3
  Dvalue = 8.229
  Group = -> [Tb_element001]
  conduct = 2
  density = 1
  expand = 3
  formula = Tb
  name = G4_Tb
  specific = 4
FEATURE [App::DocumentObjectGroupPython] Dy_element001  label="Dy_element : 1"  # scripted group (container) (typed FeaturePython)
  n = 1
  ref = Dy_element
FEATURE [App::DocumentObjectGroupPython] G4_Dy  # scripted group (container) (typed FeaturePython)
  Dunit = g/cm3
  Dvalue = 8.55
  Group = -> [Dy_element001]
  conduct = 2
  density = 1
  expand = 3
  formula = Dy
  name = G4_Dy
  specific = 4
FEATURE [App::DocumentObjectGroupPython] Ho_element001  label="Ho_element : 1"  # scripted group (container) (typed FeaturePython)
  n = 1
  ref = Ho_element
FEATURE [App::DocumentObjectGroupPython] G4_Ho  # scripted group (container) (typed FeaturePython)
  Dunit = g/cm3
  Dvalue = 8.795
  Group = -> [Ho_element001]
  conduct = 2
  density = 1
  expand = 3
  formula = Ho
  name = G4_Ho
  specific = 4
FEATURE [App::DocumentObjectGroupPython] Er_element001  label="Er_element : 1"  # scripted group (container) (typed FeaturePython)
  n = 1
  ref = Er_element
FEATURE [App::DocumentObjectGroupPython] G4_Er  # scripted group (container) (typed FeaturePython)
  Dunit = g/cm3
  Dvalue = 9.066
  Group = -> [Er_element001]
  conduct = 2
  density = 1
  expand = 3
  formula = Er
  name = G4_Er
  specific = 4
FEATURE [App::DocumentObjectGroupPython] Tm_element001  label="Tm_element : 1"  # scripted group (container) (typed FeaturePython)
  n = 1
  ref = Tm_element
FEATURE [App::DocumentObjectGroupPython] G4_Tm  # scripted group (container) (typed FeaturePython)
  Dunit = g/cm3
  Dvalue = 9.321
  Group = -> [Tm_element001]
  conduct = 2
  density = 1
  expand = 3
  formula = Tm
  name = G4_Tm
  specific = 4
FEATURE [App::DocumentObjectGroupPython] Yb_element001  label="Yb_element : 1"  # scripted group (container) (typed FeaturePython)
  n = 1
  ref = Yb_element
FEATURE [App::DocumentObjectGroupPython] G4_Yb  # scripted group (container) (typed FeaturePython)
  Dunit = g/cm3
  Dvalue = 6.73
  Group = -> [Yb_element001]
  conduct = 2
  density = 1
  expand = 3
  formula = Yb
  name = G4_Yb
  specific = 4
FEATURE [App::DocumentObjectGroupPython] Lu_element001  label="Lu_element : 1"  # scripted group (container) (typed FeaturePython)
  n = 1
  ref = Lu_element
FEATURE [App::DocumentObjectGroupPython] G4_Lu  # scripted group (container) (typed FeaturePython)
  Dunit = g/cm3
  Dvalue = 9.84
  Group = -> [Lu_element001]
  conduct = 2
  density = 1
  expand = 3
  formula = Lu
  name = G4_Lu
  specific = 4
FEATURE [App::DocumentObjectGroupPython] Hf_element001  label="Hf_element : 1"  # scripted group (container) (typed FeaturePython)
  n = 1
  ref = Hf_element
FEATURE [App::DocumentObjectGroupPython] G4_Hf  # scripted group (container) (typed FeaturePython)
  Dunit = g/cm3
  Dvalue = 13.31
  Group = -> [Hf_element001]
  conduct = 2
  density = 1
  expand = 3
  formula = Hf
  name = G4_Hf
  specific = 4
FEATURE [App::DocumentObjectGroupPython] Ta_element001  label="Ta_element : 1"  # scripted group (container) (typed FeaturePython)
  n = 1
  ref = Ta_element
FEATURE [App::DocumentObjectGroupPython] G4_Ta  # scripted group (container) (typed FeaturePython)
  Dunit = g/cm3
  Dvalue = 16.654
  Group = -> [Ta_element001]
  conduct = 2
  density = 1
  expand = 3
  formula = Ta
  name = G4_Ta
  specific = 4
FEATURE [App::DocumentObjectGroupPython] W_element004  label="W_element : 004"  # scripted group (container) (typed FeaturePython)
  n = 1
  ref = W_element
FEATURE [App::DocumentObjectGroupPython] G4_W  # scripted group (container) (typed FeaturePython)
  Dunit = g/cm3
  Dvalue = 19.3
  Group = -> [W_element004]
  conduct = 2
  density = 1
  expand = 3
  formula = W
  name = G4_W
  specific = 4
FEATURE [App::DocumentObjectGroupPython] Re_element001  label="Re_element : 1"  # scripted group (container) (typed FeaturePython)
  n = 1
  ref = Re_element
FEATURE [App::DocumentObjectGroupPython] G4_Re  # scripted group (container) (typed FeaturePython)
  Dunit = g/cm3
  Dvalue = 21.02
  Group = -> [Re_element001]
  conduct = 2
  density = 1
  expand = 3
  formula = Re
  name = G4_Re
  specific = 4
FEATURE [App::DocumentObjectGroupPython] Os_element001  label="Os_element : 1"  # scripted group (container) (typed FeaturePython)
  n = 1
  ref = Os_element
FEATURE [App::DocumentObjectGroupPython] G4_Os  # scripted group (container) (typed FeaturePython)
  Dunit = g/cm3
  Dvalue = 22.57
  Group = -> [Os_element001]
  conduct = 2
  density = 1
  expand = 3
  formula = Os
  name = G4_Os
  specific = 4
FEATURE [App::DocumentObjectGroupPython] Ir_element001  label="Ir_element : 1"  # scripted group (container) (typed FeaturePython)
  n = 1
  ref = Ir_element
FEATURE [App::DocumentObjectGroupPython] G4_Ir  # scripted group (container) (typed FeaturePython)
  Dunit = g/cm3
  Dvalue = 22.42
  Group = -> [Ir_element001]
  conduct = 2
  density = 1
  expand = 3
  formula = Ir
  name = G4_Ir
  specific = 4
FEATURE [App::DocumentObjectGroupPython] Pt_element001  label="Pt_element : 1"  # scripted group (container) (typed FeaturePython)
  n = 1
  ref = Pt_element
FEATURE [App::DocumentObjectGroupPython] G4_Pt  # scripted group (container) (typed FeaturePython)
  Dunit = g/cm3
  Dvalue = 21.45
  Group = -> [Pt_element001]
  conduct = 2
  density = 1
  expand = 3
  formula = Pt
  name = G4_Pt
  specific = 4
FEATURE [App::DocumentObjectGroupPython] Au_element001  label="Au_element : 1"  # scripted group (container) (typed FeaturePython)
  n = 1
  ref = Au_element
FEATURE [App::DocumentObjectGroupPython] G4_Au  # scripted group (container) (typed FeaturePython)
  Dunit = g/cm3
  Dvalue = 19.32
  Group = -> [Au_element001]
  conduct = 2
  density = 1
  expand = 3
  formula = Au
  name = G4_Au
  specific = 4
FEATURE [App::DocumentObjectGroupPython] Hg_element002  label="Hg_element : 002"  # scripted group (container) (typed FeaturePython)
  n = 1
  ref = Hg_element
FEATURE [App::DocumentObjectGroupPython] G4_Hg  # scripted group (container) (typed FeaturePython)
  Dunit = g/cm3
  Dvalue = 13.546
  Group = -> [Hg_element002]
  conduct = 2
  density = 1
  expand = 3
  formula = Hg
  name = G4_Hg
  specific = 4
FEATURE [App::DocumentObjectGroupPython] Tl_element002  label="Tl_element : 002"  # scripted group (container) (typed FeaturePython)
  n = 1
  ref = Tl_element
FEATURE [App::DocumentObjectGroupPython] G4_Tl  # scripted group (container) (typed FeaturePython)
  Dunit = g/cm3
  Dvalue = 11.72
  Group = -> [Tl_element002]
  conduct = 2
  density = 1
  expand = 3
  formula = Tl
  name = G4_Tl
  specific = 4
FEATURE [App::DocumentObjectGroupPython] Pb_element003  label="Pb_element : 1"  # scripted group (container) (typed FeaturePython)
  n = 1
  ref = Pb_element
FEATURE [App::DocumentObjectGroupPython] G4_Pb  # scripted group (container) (typed FeaturePython)
  Dunit = g/cm3
  Dvalue = 11.35
  Group = -> [Pb_element003]
  conduct = 2
  density = 1
  expand = 3
  formula = Pb
  name = G4_Pb
  specific = 4
FEATURE [App::DocumentObjectGroupPython] Bi_element002  label="Bi_element : 1"  # scripted group (container) (typed FeaturePython)
  n = 1
  ref = Bi_element
FEATURE [App::DocumentObjectGroupPython] G4_Bi  # scripted group (container) (typed FeaturePython)
  Dunit = g/cm3
  Dvalue = 9.747
  Group = -> [Bi_element002]
  conduct = 2
  density = 1
  expand = 3
  formula = Bi
  name = G4_Bi
  specific = 4
FEATURE [App::DocumentObjectGroupPython] Po_element001  label="Po_element : 1"  # scripted group (container) (typed FeaturePython)
  n = 1
  ref = Po_element
FEATURE [App::DocumentObjectGroupPython] G4_Po  # scripted group (container) (typed FeaturePython)
  Dunit = g/cm3
  Dvalue = 9.32
  Group = -> [Po_element001]
  conduct = 2
  density = 1
  expand = 3
  formula = Po
  name = G4_Po
  specific = 4
FEATURE [App::DocumentObjectGroupPython] At_element001  label="At_element : 1"  # scripted group (container) (typed FeaturePython)
  n = 1
  ref = At_element
FEATURE [App::DocumentObjectGroupPython] G4_At  # scripted group (container) (typed FeaturePython)
  Dunit = g/cm3
  Dvalue = 9.32
  Group = -> [At_element001]
  conduct = 2
  density = 1
  expand = 3
  formula = At
  name = G4_At
  specific = 4
FEATURE [App::DocumentObjectGroupPython] Rn_element001  label="Rn_element : 1"  # scripted group (container) (typed FeaturePython)
  n = 1
  ref = Rn_element
FEATURE [App::DocumentObjectGroupPython] G4_Rn  # scripted group (container) (typed FeaturePython)
  Dunit = g/cm3
  Dvalue = 0.00900662
  Group = -> [Rn_element001]
  conduct = 2
  density = 1
  expand = 3
  formula = Rn
  name = G4_Rn
  specific = 4
FEATURE [App::DocumentObjectGroupPython] Fr_element001  label="Fr_element : 1"  # scripted group (container) (typed FeaturePython)
  n = 1
  ref = Fr_element
FEATURE [App::DocumentObjectGroupPython] G4_Fr  # scripted group (container) (typed FeaturePython)
  Dunit = g/cm3
  Dvalue = 1
  Group = -> [Fr_element001]
  conduct = 2
  density = 1
  expand = 3
  formula = Fr
  name = G4_Fr
  specific = 4
FEATURE [App::DocumentObjectGroupPython] Ra_element001  label="Ra_element : 1"  # scripted group (container) (typed FeaturePython)
  n = 1
  ref = Ra_element
FEATURE [App::DocumentObjectGroupPython] G4_Ra  # scripted group (container) (typed FeaturePython)
  Dunit = g/cm3
  Dvalue = 5
  Group = -> [Ra_element001]
  conduct = 2
  density = 1
  expand = 3
  formula = Ra
  name = G4_Ra
  specific = 4
FEATURE [App::DocumentObjectGroupPython] Ac_element001  label="Ac_element : 1"  # scripted group (container) (typed FeaturePython)
  n = 1
  ref = Ac_element
FEATURE [App::DocumentObjectGroupPython] G4_Ac  # scripted group (container) (typed FeaturePython)
  Dunit = g/cm3
  Dvalue = 10.07
  Group = -> [Ac_element001]
  conduct = 2
  density = 1
  expand = 3
  formula = Ac
  name = G4_Ac
  specific = 4
FEATURE [App::DocumentObjectGroupPython] Th_element001  label="Th_element : 1"  # scripted group (container) (typed FeaturePython)
  n = 1
  ref = Th_element
FEATURE [App::DocumentObjectGroupPython] G4_Th  # scripted group (container) (typed FeaturePython)
  Dunit = g/cm3
  Dvalue = 11.72
  Group = -> [Th_element001]
  conduct = 2
  density = 1
  expand = 3
  formula = Th
  name = G4_Th
  specific = 4
FEATURE [App::DocumentObjectGroupPython] Pa_element001  label="Pa_element : 1"  # scripted group (container) (typed FeaturePython)
  n = 1
  ref = Pa_element
FEATURE [App::DocumentObjectGroupPython] G4_Pa  # scripted group (container) (typed FeaturePython)
  Dunit = g/cm3
  Dvalue = 15.37
  Group = -> [Pa_element001]
  conduct = 2
  density = 1
  expand = 3
  formula = Pa
  name = G4_Pa
  specific = 4
FEATURE [App::DocumentObjectGroupPython] U_element004  label="U_element : 004"  # scripted group (container) (typed FeaturePython)
  n = 1
  ref = U_element
FEATURE [App::DocumentObjectGroupPython] G4_U  # scripted group (container) (typed FeaturePython)
  Dunit = g/cm3
  Dvalue = 18.95
  Group = -> [U_element004]
  conduct = 2
  density = 1
  expand = 3
  formula = U
  name = G4_U
  specific = 4
FEATURE [App::DocumentObjectGroupPython] Np_element001  label="Np_element : 1"  # scripted group (container) (typed FeaturePython)
  n = 1
  ref = Np_element
FEATURE [App::DocumentObjectGroupPython] G4_Np  # scripted group (container) (typed FeaturePython)
  Dunit = g/cm3
  Dvalue = 20.25
  Group = -> [Np_element001]
  conduct = 2
  density = 1
  expand = 3
  formula = Np
  name = G4_Np
  specific = 4
FEATURE [App::DocumentObjectGroupPython] Pu_element002  label="Pu_element : 002"  # scripted group (container) (typed FeaturePython)
  n = 1
  ref = Pu_element
FEATURE [App::DocumentObjectGroupPython] G4_Pu  # scripted group (container) (typed FeaturePython)
  Dunit = g/cm3
  Dvalue = 19.84
  Group = -> [Pu_element002]
  conduct = 2
  density = 1
  expand = 3
  formula = Pu
  name = G4_Pu
  specific = 4
FEATURE [App::DocumentObjectGroupPython] Am_element001  label="Am_element : 1"  # scripted group (container) (typed FeaturePython)
  n = 1
  ref = Am_element
FEATURE [App::DocumentObjectGroupPython] G4_Am  # scripted group (container) (typed FeaturePython)
  Dunit = g/cm3
  Dvalue = 13.67
  Group = -> [Am_element001]
  conduct = 2
  density = 1
  expand = 3
  formula = Am
  name = G4_Am
  specific = 4
FEATURE [App::DocumentObjectGroupPython] Cm_element001  label="Cm_element : 1"  # scripted group (container) (typed FeaturePython)
  n = 1
  ref = Cm_element
FEATURE [App::DocumentObjectGroupPython] G4_Cm  # scripted group (container) (typed FeaturePython)
  Dunit = g/cm3
  Dvalue = 13.51
  Group = -> [Cm_element001]
  conduct = 2
  density = 1
  expand = 3
  formula = Cm
  name = G4_Cm
  specific = 4
FEATURE [App::DocumentObjectGroupPython] Bk_element001  label="Bk_element : 1"  # scripted group (container) (typed FeaturePython)
  n = 1
  ref = Bk_element
FEATURE [App::DocumentObjectGroupPython] G4_Bk  # scripted group (container) (typed FeaturePython)
  Dunit = g/cm3
  Dvalue = 14
  Group = -> [Bk_element001]
  conduct = 2
  density = 1
  expand = 3
  formula = Bk
  name = G4_Bk
  specific = 4
FEATURE [App::DocumentObjectGroupPython] Cf_element001  label="Cf_element : 1"  # scripted group (container) (typed FeaturePython)
  n = 1
  ref = Cf_element
FEATURE [App::DocumentObjectGroupPython] G4_Cf  # scripted group (container) (typed FeaturePython)
  Dunit = g/cm3
  Dvalue = 10
  Group = -> [Cf_element001]
  conduct = 2
  density = 1
  expand = 3
  formula = Cf
  name = G4_Cf
  specific = 4
FEATURE [App::DocumentObjectGroupPython] Element  # scripted group (container) (typed FeaturePython)
  Group = -> [G4_H,G4_He,G4_Li,G4_Be,G4_B,G4_C,G4_N,G4_O,G4_F,G4_Ne,G4_Na,G4_Mg,G4_Al,G4_Si,G4_P,G4_S,G4_Cl,G4_Ar,G4_K,G4_Ca,G4_Sc,G4_Ti,G4_V,G4_Cr,G4_Mn,G4_Fe,G4_Co,G4_Ni,G4_Cu,G4_Zn,G4_Ga,G4_Ge,G4_As,G4_Se,G4_Br,G4_Kr,G4_Rb,G4_Sr,G4_Y,G4_Zr,G4_Nb,G4_Mo,G4_Tc,G4_Ru,G4_Rh,G4_Pd,G4_Ag,G4_Cd,G4_In,G4_Sn,G4_Sb,G4_Te,G4_I,G4_Xe,G4_Cs,G4_Ba,G4_La,G4_Ce,G4_Pr,G4_Nd,G4_Pm,G4_Sm,G4_Eu,G4_Gd,G4_Tb,G4_Dy,G4_Ho,G4_Er,+30 more]
FEATURE [App::DocumentObjectGroupPython] H_element114  label="H_element : 063"  # scripted group (container) (typed FeaturePython)
  n = 2
  ref = H_element
FEATURE [App::DocumentObjectGroupPython] G4_lH2  # scripted group (container) (typed FeaturePython)
  Dunit = g/cm3
  Dvalue = 0.0708
  Group = -> [H_element114]
  conduct = 2
  density = 1
  expand = 3
  formula = G4_lH2
  name = G4_lH2
  specific = 4
FEATURE [App::DocumentObjectGroupPython] N_element049  label="N_element : 022"  # scripted group (container) (typed FeaturePython)
  n = 2
  ref = N_element
FEATURE [App::DocumentObjectGroupPython] G4_lN2  # scripted group (container) (typed FeaturePython)
  Dunit = g/cm3
  Dvalue = 0.807
  Group = -> [N_element049]
  conduct = 2
  density = 1
  expand = 3
  formula = G4_lN2
  name = G4_lN2
  specific = 4
FEATURE [App::DocumentObjectGroupPython] O_element106  label="O_element : 060"  # scripted group (container) (typed FeaturePython)
  n = 2
  ref = O_element
FEATURE [App::DocumentObjectGroupPython] G4_lO2  # scripted group (container) (typed FeaturePython)
  Dunit = g/cm3
  Dvalue = 1.141
  Group = -> [O_element106]
  conduct = 2
  density = 1
  expand = 3
  formula = G4_lO2
  name = G4_lO2
  specific = 4
FEATURE [App::DocumentObjectGroupPython] Ar_element003  label="Ar_element : 002"  # scripted group (container) (typed FeaturePython)
  n = 1
  ref = Ar_element
FEATURE [App::DocumentObjectGroupPython] G4_lAr  # scripted group (container) (typed FeaturePython)
  Dunit = g/cm3
  Dvalue = 1.396
  Group = -> [Ar_element003]
  conduct = 2
  density = 1
  expand = 3
  formula = G4_lAr
  name = G4_lAr
  specific = 4
FEATURE [App::DocumentObjectGroupPython] Br_element008  label="Br_element : 005"  # scripted group (container) (typed FeaturePython)
  n = 1
  ref = Br_element
FEATURE [App::DocumentObjectGroupPython] G4_lBr  # scripted group (container) (typed FeaturePython)
  Dunit = g/cm3
  Dvalue = 3.1028
  Group = -> [Br_element008]
  conduct = 2
  density = 1
  expand = 3
  formula = G4_lBr
  name = G4_lBr
  specific = 4
FEATURE [App::DocumentObjectGroupPython] Kr_element002  label="Kr_element : 002"  # scripted group (container) (typed FeaturePython)
  n = 1
  ref = Kr_element
FEATURE [App::DocumentObjectGroupPython] G4_lKr  # scripted group (container) (typed FeaturePython)
  Dunit = g/cm3
  Dvalue = 2.418
  Group = -> [Kr_element002]
  conduct = 2
  density = 1
  expand = 3
  formula = G4_lKr
  name = G4_lKr
  specific = 4
FEATURE [App::DocumentObjectGroupPython] Xe_element002  label="Xe_element : 002"  # scripted group (container) (typed FeaturePython)
  n = 1
  ref = Xe_element
FEATURE [App::DocumentObjectGroupPython] G4_lXe  # scripted group (container) (typed FeaturePython)
  Dunit = g/cm3
  Dvalue = 2.953
  Group = -> [Xe_element002]
  conduct = 2
  density = 1
  expand = 3
  formula = G4_lXe
  name = G4_lXe
  specific = 4
FEATURE [App::DocumentObjectGroupPython] O_element107  label="O_element : 061"  # scripted group (container) (typed FeaturePython)
  n = 4
  ref = O_element
FEATURE [App::DocumentObjectGroupPython] Pb_element004  label="Pb_element : 002"  # scripted group (container) (typed FeaturePython)
  n = 1
  ref = Pb_element
FEATURE [App::DocumentObjectGroupPython] W_element005  label="W_element : 005"  # scripted group (container) (typed FeaturePython)
  n = 1
  ref = W_element
FEATURE [App::DocumentObjectGroupPython] G4_PbWO4  # scripted group (container) (typed FeaturePython)
  Dunit = g/cm3
  Dvalue = 8.28
  Group = -> [O_element107,Pb_element004,W_element005]
  conduct = 2
  density = 1
  expand = 3
  formula = G4_PbWO4
  name = G4_PbWO4
  specific = 4
FEATURE [App::DocumentObjectGroupPython] H_element115  label="H_element : 064"  # scripted group (container) (typed FeaturePython)
  n = 1
  ref = H_element
FEATURE [App::DocumentObjectGroupPython] G4_Galactic  # scripted group (container) (typed FeaturePython)
  Dunit = g/cm3
  Dvalue = 0
  Group = -> [H_element115]
  conduct = 2
  density = 1
  expand = 3
  formula = G4_Galactic
  name = G4_Galactic
  specific = 4
FEATURE [App::DocumentObjectGroupPython] C_element125  label="C_element : 071"  # scripted group (container) (typed FeaturePython)
  n = 1
  ref = C_element
FEATURE [App::DocumentObjectGroupPython] G4_GRAPHITE_POROUS  # scripted group (container) (typed FeaturePython)
  Dunit = g/cm3
  Dvalue = 1.7
  Group = -> [C_element125]
  conduct = 2
  density = 1
  expand = 3
  formula = G4_GRAPHITE_POROUS
  name = G4_GRAPHITE_POROUS
  specific = 4
FEATURE [App::DocumentObjectGroupPython] H_element116  label="H_element : 0.150"  # scripted group (container) (typed FeaturePython)
  n = 0.080538
FEATURE [App::DocumentObjectGroupPython] C_element126  label="C_element : 0.600"  # scripted group (container) (typed FeaturePython)
  n = 0.599848
FEATURE [App::DocumentObjectGroupPython] O_element108  label="O_element : 0.320"  # scripted group (container) (typed FeaturePython)
  n = 0.319614
FEATURE [App::DocumentObjectGroupPython] G4_LUCITE  # scripted group (container) (typed FeaturePython)
  Dunit = g/cm3
  Dvalue = 1.19
  Group = -> [H_element116,C_element126,O_element108]
  conduct = 2
  density = 1
  expand = 3
  formula = G4_LUCITE
  name = G4_LUCITE
  specific = 4
FEATURE [App::DocumentObjectGroupPython] Cu_element002  label="Cu_element : 62"  # scripted group (container) (typed FeaturePython)
  n = 62
  ref = Cu_element
FEATURE [App::DocumentObjectGroupPython] Zn_element002  label="Zn_element : 35"  # scripted group (container) (typed FeaturePython)
  n = 35
  ref = Zn_element
FEATURE [App::DocumentObjectGroupPython] Pb_element005  label="Pb_element : 3"  # scripted group (container) (typed FeaturePython)
  n = 3
  ref = Pb_element
FEATURE [App::DocumentObjectGroupPython] G4_BRASS  # scripted group (container) (typed FeaturePython)
  Dunit = g/cm3
  Dvalue = 8.52
  Group = -> [Cu_element002,Zn_element002,Pb_element005]
  conduct = 2
  density = 1
  expand = 3
  formula = G4_BRASS
  name = G4_BRASS
  specific = 4
FEATURE [App::DocumentObjectGroupPython] Cu_element003  label="Cu_element : 89"  # scripted group (container) (typed FeaturePython)
  n = 89
  ref = Cu_element
FEATURE [App::DocumentObjectGroupPython] Zn_element003  label="Zn_element : 9"  # scripted group (container) (typed FeaturePython)
  n = 9
  ref = Zn_element
FEATURE [App::DocumentObjectGroupPython] Pb_element006  label="Pb_element : 2"  # scripted group (container) (typed FeaturePython)
  n = 2
  ref = Pb_element
FEATURE [App::DocumentObjectGroupPython] G4_BRONZE  # scripted group (container) (typed FeaturePython)
  Dunit = g/cm3
  Dvalue = 8.82
  Group = -> [Cu_element003,Zn_element003,Pb_element006]
  conduct = 2
  density = 1
  expand = 3
  formula = G4_BRONZE
  name = G4_BRONZE
  specific = 4
FEATURE [App::DocumentObjectGroupPython] Fe_element008  label="Fe_element : 74"  # scripted group (container) (typed FeaturePython)
  n = 74
  ref = Fe_element
FEATURE [App::DocumentObjectGroupPython] Cr_element002  label="Cr_element : 18"  # scripted group (container) (typed FeaturePython)
  n = 18
  ref = Cr_element
FEATURE [App::DocumentObjectGroupPython] Ni_element002  label="Ni_element : 8"  # scripted group (container) (typed FeaturePython)
  n = 8
  ref = Ni_element
FEATURE [App::DocumentObjectGroupPython] G4_STAINLESS_STEEL  label="G4_STAINLESS-STEEL"  # scripted group (container) (typed FeaturePython)
  Dunit = g/cm3
  Dvalue = 8
  Group = -> [Fe_element008,Cr_element002,Ni_element002]
  conduct = 2
  density = 1
  expand = 3
  formula = G4_STAINLESS-STEEL
  name = G4_STAINLESS-STEEL
  specific = 4
FEATURE [App::DocumentObjectGroupPython] H_element117  label="H_element : 065"  # scripted group (container) (typed FeaturePython)
  n = 18
  ref = H_element
FEATURE [App::DocumentObjectGroupPython] C_element127  label="C_element : 072"  # scripted group (container) (typed FeaturePython)
  n = 12
  ref = C_element
FEATURE [App::DocumentObjectGroupPython] O_element109  label="O_element : 062"  # scripted group (container) (typed FeaturePython)
  n = 7
  ref = O_element
FEATURE [App::DocumentObjectGroupPython] G4_CR39  # scripted group (container) (typed FeaturePython)
  Dunit = g/cm3
  Dvalue = 1.32
  Group = -> [H_element117,C_element127,O_element109]
  conduct = 2
  density = 1
  expand = 3
  formula = G4_CR39
  name = G4_CR39
  specific = 4
FEATURE [App::DocumentObjectGroupPython] H_element118  label="H_element : 38"  # scripted group (container) (typed FeaturePython)
  n = 38
  ref = H_element
FEATURE [App::DocumentObjectGroupPython] C_element128  label="C_element : 073"  # scripted group (container) (typed FeaturePython)
  n = 18
  ref = C_element
FEATURE [App::DocumentObjectGroupPython] O_element110  label="O_element : 063"  # scripted group (container) (typed FeaturePython)
  n = 1
  ref = O_element
FEATURE [App::DocumentObjectGroupPython] G4_OCTADECANOL  # scripted group (container) (typed FeaturePython)
  Dunit = g/cm3
  Dvalue = 0.812
  Group = -> [H_element118,C_element128,O_element110]
  conduct = 2
  density = 1
  expand = 3
  formula = G4_OCTADECANOL
  name = G4_OCTADECANOL
  specific = 4
FEATURE [App::DocumentObjectGroupPython] HEP  # scripted group (container) (typed FeaturePython)
  Group = -> [G4_lH2,G4_lN2,G4_lO2,G4_lAr,G4_lBr,G4_lKr,G4_lXe,G4_PbWO4,G4_Galactic,G4_GRAPHITE_POROUS,G4_LUCITE,G4_BRASS,G4_BRONZE,G4_STAINLESS_STEEL,G4_CR39,G4_OCTADECANOL]
FEATURE [App::DocumentObjectGroupPython] C_element129  label="C_element : 074"  # scripted group (container) (typed FeaturePython)
  n = 14
  ref = C_element
FEATURE [App::DocumentObjectGroupPython] H_element119  label="H_element : 066"  # scripted group (container) (typed FeaturePython)
  n = 10
  ref = H_element
FEATURE [App::DocumentObjectGroupPython] O_element111  label="O_element : 064"  # scripted group (container) (typed FeaturePython)
  n = 2
  ref = O_element
FEATURE [App::DocumentObjectGroupPython] N_element050  label="N_element : 023"  # scripted group (container) (typed FeaturePython)
  n = 2
  ref = N_element
FEATURE [App::DocumentObjectGroupPython] G4_KEVLAR  # scripted group (container) (typed FeaturePython)
  Dunit = g/cm3
  Dvalue = 1.44
  Group = -> [C_element129,H_element119,O_element111,N_element050]
  conduct = 2
  density = 1
  expand = 3
  formula = G4_KEVLAR
  name = G4_KEVLAR
  specific = 4
FEATURE [App::DocumentObjectGroupPython] C_element130  label="C_element : 075"  # scripted group (container) (typed FeaturePython)
  n = 10
  ref = C_element
FEATURE [App::DocumentObjectGroupPython] H_element120  label="H_element : 067"  # scripted group (container) (typed FeaturePython)
  n = 8
  ref = H_element
FEATURE [App::DocumentObjectGroupPython] O_element112  label="O_element : 065"  # scripted group (container) (typed FeaturePython)
  n = 4
  ref = O_element
FEATURE [App::DocumentObjectGroupPython] G4_DACRON  # scripted group (container) (typed FeaturePython)
  Dunit = g/cm3
  Dvalue = 1.4
  Group = -> [C_element130,H_element120,O_element112]
  conduct = 2
  density = 1
  expand = 3
  formula = G4_DACRON
  name = G4_DACRON
  specific = 4
FEATURE [App::DocumentObjectGroupPython] C_element131  label="C_element : 076"  # scripted group (container) (typed FeaturePython)
  n = 4
  ref = C_element
FEATURE [App::DocumentObjectGroupPython] H_element121  label="H_element : 068"  # scripted group (container) (typed FeaturePython)
  n = 5
  ref = H_element
FEATURE [App::DocumentObjectGroupPython] Cl_element030  label="Cl_element : 016"  # scripted group (container) (typed FeaturePython)
  n = 1
  ref = Cl_element
FEATURE [App::DocumentObjectGroupPython] G4_NEOPRENE  # scripted group (container) (typed FeaturePython)
  Dunit = g/cm3
  Dvalue = 1.23
  Group = -> [C_element131,H_element121,Cl_element030]
  conduct = 2
  density = 1
  expand = 3
  formula = G4_NEOPRENE
  name = G4_NEOPRENE
  specific = 4
FEATURE [App::DocumentObjectGroupPython] Space  # scripted group (container) (typed FeaturePython)
  Group = -> [G4_KEVLAR,G4_DACRON,G4_NEOPRENE]
FEATURE [App::DocumentObjectGroupPython] H_element122  label="H_element : 069"  # scripted group (container) (typed FeaturePython)
  n = 5
  ref = H_element
FEATURE [App::DocumentObjectGroupPython] C_element132  label="C_element : 077"  # scripted group (container) (typed FeaturePython)
  n = 4
  ref = C_element
FEATURE [App::DocumentObjectGroupPython] N_element051  label="N_element : 3"  # scripted group (container) (typed FeaturePython)
  n = 3
  ref = N_element
FEATURE [App::DocumentObjectGroupPython] O_element113  label="O_element : 066"  # scripted group (container) (typed FeaturePython)
  n = 1
  ref = O_element
FEATURE [App::DocumentObjectGroupPython] G4_CYTOSINE  # scripted group (container) (typed FeaturePython)
  Dunit = g/cm3
  Dvalue = 1.55
  Group = -> [H_element122,C_element132,N_element051,O_element113]
  conduct = 2
  density = 1
  expand = 3
  formula = G4_CYTOSINE
  name = G4_CYTOSINE
  specific = 4
FEATURE [App::DocumentObjectGroupPython] H_element123  label="H_element : 070"  # scripted group (container) (typed FeaturePython)
  n = 6
  ref = H_element
FEATURE [App::DocumentObjectGroupPython] C_element133  label="C_element : 078"  # scripted group (container) (typed FeaturePython)
  n = 5
  ref = C_element
FEATURE [App::DocumentObjectGroupPython] N_element052  label="N_element : 024"  # scripted group (container) (typed FeaturePython)
  n = 2
  ref = N_element
FEATURE [App::DocumentObjectGroupPython] O_element114  label="O_element : 067"  # scripted group (container) (typed FeaturePython)
  n = 2
  ref = O_element
FEATURE [App::DocumentObjectGroupPython] G4_THYMINE  # scripted group (container) (typed FeaturePython)
  Dunit = g/cm3
  Dvalue = 1.23
  Group = -> [H_element123,C_element133,N_element052,O_element114]
  conduct = 2
  density = 1
  expand = 3
  formula = G4_THYMINE
  name = G4_THYMINE
  specific = 4
FEATURE [App::DocumentObjectGroupPython] H_element124  label="H_element : 071"  # scripted group (container) (typed FeaturePython)
  n = 4
  ref = H_element
FEATURE [App::DocumentObjectGroupPython] C_element134  label="C_element : 079"  # scripted group (container) (typed FeaturePython)
  n = 4
  ref = C_element
FEATURE [App::DocumentObjectGroupPython] N_element053  label="N_element : 025"  # scripted group (container) (typed FeaturePython)
  n = 2
  ref = N_element
FEATURE [App::DocumentObjectGroupPython] O_element115  label="O_element : 068"  # scripted group (container) (typed FeaturePython)
  n = 2
  ref = O_element
FEATURE [App::DocumentObjectGroupPython] G4_URACIL  # scripted group (container) (typed FeaturePython)
  Dunit = g/cm3
  Dvalue = 1.32
  Group = -> [H_element124,C_element134,N_element053,O_element115]
  conduct = 2
  density = 1
  expand = 3
  formula = G4_URACIL
  name = G4_URACIL
  specific = 4
FEATURE [App::DocumentObjectGroupPython] H_element125  label="H_element : 072"  # scripted group (container) (typed FeaturePython)
  n = 4
  ref = H_element
FEATURE [App::DocumentObjectGroupPython] C_element135  label="C_element : 080"  # scripted group (container) (typed FeaturePython)
  n = 5
  ref = C_element
FEATURE [App::DocumentObjectGroupPython] N_element054  label="N_element : 026"  # scripted group (container) (typed FeaturePython)
  n = 5
  ref = N_element
FEATURE [App::DocumentObjectGroupPython] G4_DNA_ADENINE  # scripted group (container) (typed FeaturePython)
  Dunit = g/cm3
  Dvalue = 1
  Group = -> [H_element125,C_element135,N_element054]
  conduct = 2
  density = 1
  expand = 3
  formula = G4_DNA_ADENINE
  name = G4_DNA_ADENINE
  specific = 4
FEATURE [App::DocumentObjectGroupPython] H_element126  label="H_element : 073"  # scripted group (container) (typed FeaturePython)
  n = 4
  ref = H_element
FEATURE [App::DocumentObjectGroupPython] C_element136  label="C_element : 081"  # scripted group (container) (typed FeaturePython)
  n = 5
  ref = C_element
FEATURE [App::DocumentObjectGroupPython] N_element055  label="N_element : 027"  # scripted group (container) (typed FeaturePython)
  n = 5
  ref = N_element
FEATURE [App::DocumentObjectGroupPython] O_element116  label="O_element : 069"  # scripted group (container) (typed FeaturePython)
  n = 1
  ref = O_element
FEATURE [App::DocumentObjectGroupPython] G4_DNA_GUANINE  # scripted group (container) (typed FeaturePython)
  Dunit = g/cm3
  Dvalue = 1
  Group = -> [H_element126,C_element136,N_element055,O_element116]
  conduct = 2
  density = 1
  expand = 3
  formula = G4_DNA_GUANINE
  name = G4_DNA_GUANINE
  specific = 4
FEATURE [App::DocumentObjectGroupPython] H_element127  label="H_element : 074"  # scripted group (container) (typed FeaturePython)
  n = 4
  ref = H_element
FEATURE [App::DocumentObjectGroupPython] C_element137  label="C_element : 082"  # scripted group (container) (typed FeaturePython)
  n = 4
  ref = C_element
FEATURE [App::DocumentObjectGroupPython] N_element056  label="N_element : 028"  # scripted group (container) (typed FeaturePython)
  n = 3
  ref = N_element
FEATURE [App::DocumentObjectGroupPython] O_element117  label="O_element : 070"  # scripted group (container) (typed FeaturePython)
  n = 1
  ref = O_element
FEATURE [App::DocumentObjectGroupPython] G4_DNA_CYTOSINE  # scripted group (container) (typed FeaturePython)
  Dunit = g/cm3
  Dvalue = 1
  Group = -> [H_element127,C_element137,N_element056,O_element117]
  conduct = 2
  density = 1
  expand = 3
  formula = G4_DNA_CYTOSINE
  name = G4_DNA_CYTOSINE
  specific = 4
FEATURE [App::DocumentObjectGroupPython] H_element128  label="H_element : 075"  # scripted group (container) (typed FeaturePython)
  n = 5
  ref = H_element
FEATURE [App::DocumentObjectGroupPython] C_element138  label="C_element : 083"  # scripted group (container) (typed FeaturePython)
  n = 5
  ref = C_element
FEATURE [App::DocumentObjectGroupPython] N_element057  label="N_element : 029"  # scripted group (container) (typed FeaturePython)
  n = 2
  ref = N_element
FEATURE [App::DocumentObjectGroupPython] O_element118  label="O_element : 071"  # scripted group (container) (typed FeaturePython)
  n = 2
  ref = O_element
FEATURE [App::DocumentObjectGroupPython] G4_DNA_THYMINE  # scripted group (container) (typed FeaturePython)
  Dunit = g/cm3
  Dvalue = 1
  Group = -> [H_element128,C_element138,N_element057,O_element118]
  conduct = 2
  density = 1
  expand = 3
  formula = G4_DNA_THYMINE
  name = G4_DNA_THYMINE
  specific = 4
FEATURE [App::DocumentObjectGroupPython] H_element129  label="H_element : 076"  # scripted group (container) (typed FeaturePython)
  n = 3
  ref = H_element
FEATURE [App::DocumentObjectGroupPython] C_element139  label="C_element : 084"  # scripted group (container) (typed FeaturePython)
  n = 4
  ref = C_element
FEATURE [App::DocumentObjectGroupPython] N_element058  label="N_element : 030"  # scripted group (container) (typed FeaturePython)
  n = 2
  ref = N_element
FEATURE [App::DocumentObjectGroupPython] O_element119  label="O_element : 072"  # scripted group (container) (typed FeaturePython)
  n = 2
  ref = O_element
FEATURE [App::DocumentObjectGroupPython] G4_DNA_URACIL  # scripted group (container) (typed FeaturePython)
  Dunit = g/cm3
  Dvalue = 1
  Group = -> [H_element129,C_element139,N_element058,O_element119]
  conduct = 2
  density = 1
  expand = 3
  formula = G4_DNA_URACIL
  name = G4_DNA_URACIL
  specific = 4
FEATURE [App::DocumentObjectGroupPython] H_element130  label="H_element : 077"  # scripted group (container) (typed FeaturePython)
  n = 10
  ref = H_element
FEATURE [App::DocumentObjectGroupPython] C_element140  label="C_element : 085"  # scripted group (container) (typed FeaturePython)
  n = 10
  ref = C_element
FEATURE [App::DocumentObjectGroupPython] N_element059  label="N_element : 031"  # scripted group (container) (typed FeaturePython)
  n = 5
  ref = N_element
FEATURE [App::DocumentObjectGroupPython] O_element120  label="O_element : 073"  # scripted group (container) (typed FeaturePython)
  n = 4
  ref = O_element
FEATURE [App::DocumentObjectGroupPython] G4_DNA_ADENOSINE  # scripted group (container) (typed FeaturePython)
  Dunit = g/cm3
  Dvalue = 1
  Group = -> [H_element130,C_element140,N_element059,O_element120]
  conduct = 2
  density = 1
  expand = 3
  formula = G4_DNA_ADENOSINE
  name = G4_DNA_ADENOSINE
  specific = 4
FEATURE [App::DocumentObjectGroupPython] H_element131  label="H_element : 078"  # scripted group (container) (typed FeaturePython)
  n = 10
  ref = H_element
FEATURE [App::DocumentObjectGroupPython] C_element141  label="C_element : 086"  # scripted group (container) (typed FeaturePython)
  n = 10
  ref = C_element
FEATURE [App::DocumentObjectGroupPython] N_element060  label="N_element : 032"  # scripted group (container) (typed FeaturePython)
  n = 5
  ref = N_element
FEATURE [App::DocumentObjectGroupPython] O_element121  label="O_element : 074"  # scripted group (container) (typed FeaturePython)
  n = 5
  ref = O_element
FEATURE [App::DocumentObjectGroupPython] G4_DNA_GUANOSINE  # scripted group (container) (typed FeaturePython)
  Dunit = g/cm3
  Dvalue = 1
  Group = -> [H_element131,C_element141,N_element060,O_element121]
  conduct = 2
  density = 1
  expand = 3
  formula = G4_DNA_GUANOSINE
  name = G4_DNA_GUANOSINE
  specific = 4
FEATURE [App::DocumentObjectGroupPython] H_element132  label="H_element : 079"  # scripted group (container) (typed FeaturePython)
  n = 10
  ref = H_element
FEATURE [App::DocumentObjectGroupPython] C_element142  label="C_element : 087"  # scripted group (container) (typed FeaturePython)
  n = 9
  ref = C_element
FEATURE [App::DocumentObjectGroupPython] N_element061  label="N_element : 033"  # scripted group (container) (typed FeaturePython)
  n = 3
  ref = N_element
FEATURE [App::DocumentObjectGroupPython] O_element122  label="O_element : 075"  # scripted group (container) (typed FeaturePython)
  n = 5
  ref = O_element
FEATURE [App::DocumentObjectGroupPython] G4_DNA_CYTIDINE  # scripted group (container) (typed FeaturePython)
  Dunit = g/cm3
  Dvalue = 1
  Group = -> [H_element132,C_element142,N_element061,O_element122]
  conduct = 2
  density = 1
  expand = 3
  formula = G4_DNA_CYTIDINE
  name = G4_DNA_CYTIDINE
  specific = 4
FEATURE [App::DocumentObjectGroupPython] H_element133  label="H_element : 080"  # scripted group (container) (typed FeaturePython)
  n = 9
  ref = H_element
FEATURE [App::DocumentObjectGroupPython] C_element143  label="C_element : 088"  # scripted group (container) (typed FeaturePython)
  n = 9
  ref = C_element
FEATURE [App::DocumentObjectGroupPython] N_element062  label="N_element : 034"  # scripted group (container) (typed FeaturePython)
  n = 2
  ref = N_element
FEATURE [App::DocumentObjectGroupPython] O_element123  label="O_element : 076"  # scripted group (container) (typed FeaturePython)
  n = 6
  ref = O_element
FEATURE [App::DocumentObjectGroupPython] G4_DNA_URIDINE  # scripted group (container) (typed FeaturePython)
  Dunit = g/cm3
  Dvalue = 1
  Group = -> [H_element133,C_element143,N_element062,O_element123]
  conduct = 2
  density = 1
  expand = 3
  formula = G4_DNA_URIDINE
  name = G4_DNA_URIDINE
  specific = 4
FEATURE [App::DocumentObjectGroupPython] H_element134  label="H_element : 081"  # scripted group (container) (typed FeaturePython)
  n = 11
  ref = H_element
FEATURE [App::DocumentObjectGroupPython] C_element144  label="C_element : 089"  # scripted group (container) (typed FeaturePython)
  n = 10
  ref = C_element
FEATURE [App::DocumentObjectGroupPython] N_element063  label="N_element : 035"  # scripted group (container) (typed FeaturePython)
  n = 2
  ref = N_element
FEATURE [App::DocumentObjectGroupPython] O_element124  label="O_element : 077"  # scripted group (container) (typed FeaturePython)
  n = 6
  ref = O_element
FEATURE [App::DocumentObjectGroupPython] G4_DNA_METHYLURIDINE  # scripted group (container) (typed FeaturePython)
  Dunit = g/cm3
  Dvalue = 1
  Group = -> [H_element134,C_element144,N_element063,O_element124]
  conduct = 2
  density = 1
  expand = 3
  formula = G4_DNA_METHYLURIDINE
  name = G4_DNA_METHYLURIDINE
  specific = 4
FEATURE [App::DocumentObjectGroupPython] P_element014  label="P_element : 003"  # scripted group (container) (typed FeaturePython)
  n = 1
  ref = P_element
FEATURE [App::DocumentObjectGroupPython] O_element125  label="O_element : 078"  # scripted group (container) (typed FeaturePython)
  n = 3
  ref = O_element
FEATURE [App::DocumentObjectGroupPython] G4_DNA_MONOPHOSPHATE  # scripted group (container) (typed FeaturePython)
  Dunit = g/cm3
  Dvalue = 1
  Group = -> [P_element014,O_element125]
  conduct = 2
  density = 1
  expand = 3
  formula = G4_DNA_MONOPHOSPHATE
  name = G4_DNA_MONOPHOSPHATE
  specific = 4
FEATURE [App::DocumentObjectGroupPython] H_element135  label="H_element : 082"  # scripted group (container) (typed FeaturePython)
  n = 10
  ref = H_element
FEATURE [App::DocumentObjectGroupPython] C_element145  label="C_element : 090"  # scripted group (container) (typed FeaturePython)
  n = 10
  ref = C_element
FEATURE [App::DocumentObjectGroupPython] N_element064  label="N_element : 036"  # scripted group (container) (typed FeaturePython)
  n = 5
  ref = N_element
FEATURE [App::DocumentObjectGroupPython] O_element126  label="O_element : 079"  # scripted group (container) (typed FeaturePython)
  n = 7
  ref = O_element
FEATURE [App::DocumentObjectGroupPython] P_element015  label="P_element : 004"  # scripted group (container) (typed FeaturePython)
  n = 1
  ref = P_element
FEATURE [App::DocumentObjectGroupPython] G4_DNA_A  # scripted group (container) (typed FeaturePython)
  Dunit = g/cm3
  Dvalue = 1
  Group = -> [H_element135,C_element145,N_element064,O_element126,P_element015]
  conduct = 2
  density = 1
  expand = 3
  formula = G4_DNA_A
  name = G4_DNA_A
  specific = 4
FEATURE [App::DocumentObjectGroupPython] H_element136  label="H_element : 083"  # scripted group (container) (typed FeaturePython)
  n = 10
  ref = H_element
FEATURE [App::DocumentObjectGroupPython] C_element146  label="C_element : 091"  # scripted group (container) (typed FeaturePython)
  n = 10
  ref = C_element
FEATURE [App::DocumentObjectGroupPython] N_element065  label="N_element : 037"  # scripted group (container) (typed FeaturePython)
  n = 5
  ref = N_element
FEATURE [App::DocumentObjectGroupPython] O_element127  label="O_element : 8"  # scripted group (container) (typed FeaturePython)
  n = 8
  ref = O_element
FEATURE [App::DocumentObjectGroupPython] P_element016  label="P_element : 005"  # scripted group (container) (typed FeaturePython)
  n = 1
  ref = P_element
FEATURE [App::DocumentObjectGroupPython] G4_DNA_G  # scripted group (container) (typed FeaturePython)
  Dunit = g/cm3
  Dvalue = 1
  Group = -> [H_element136,C_element146,N_element065,O_element127,P_element016]
  conduct = 2
  density = 1
  expand = 3
  formula = G4_DNA_G
  name = G4_DNA_G
  specific = 4
FEATURE [App::DocumentObjectGroupPython] H_element137  label="H_element : 084"  # scripted group (container) (typed FeaturePython)
  n = 10
  ref = H_element
FEATURE [App::DocumentObjectGroupPython] C_element147  label="C_element : 092"  # scripted group (container) (typed FeaturePython)
  n = 9
  ref = C_element
FEATURE [App::DocumentObjectGroupPython] N_element066  label="N_element : 038"  # scripted group (container) (typed FeaturePython)
  n = 3
  ref = N_element
FEATURE [App::DocumentObjectGroupPython] O_element128  label="O_element : 080"  # scripted group (container) (typed FeaturePython)
  n = 8
  ref = O_element
FEATURE [App::DocumentObjectGroupPython] P_element017  label="P_element : 006"  # scripted group (container) (typed FeaturePython)
  n = 1
  ref = P_element
FEATURE [App::DocumentObjectGroupPython] G4_DNA_C  # scripted group (container) (typed FeaturePython)
  Dunit = g/cm3
  Dvalue = 1
  Group = -> [H_element137,C_element147,N_element066,O_element128,P_element017]
  conduct = 2
  density = 1
  expand = 3
  formula = G4_DNA_C
  name = G4_DNA_C
  specific = 4
FEATURE [App::DocumentObjectGroupPython] H_element138  label="H_element : 085"  # scripted group (container) (typed FeaturePython)
  n = 9
  ref = H_element
FEATURE [App::DocumentObjectGroupPython] C_element148  label="C_element : 093"  # scripted group (container) (typed FeaturePython)
  n = 9
  ref = C_element
FEATURE [App::DocumentObjectGroupPython] N_element067  label="N_element : 039"  # scripted group (container) (typed FeaturePython)
  n = 2
  ref = N_element
FEATURE [App::DocumentObjectGroupPython] O_element129  label="O_element : 9"  # scripted group (container) (typed FeaturePython)
  n = 9
  ref = O_element
FEATURE [App::DocumentObjectGroupPython] P_element018  label="P_element : 007"  # scripted group (container) (typed FeaturePython)
  n = 1
  ref = P_element
FEATURE [App::DocumentObjectGroupPython] G4_DNA_U  # scripted group (container) (typed FeaturePython)
  Dunit = g/cm3
  Dvalue = 1
  Group = -> [H_element138,C_element148,N_element067,O_element129,P_element018]
  conduct = 2
  density = 1
  expand = 3
  formula = G4_DNA_U
  name = G4_DNA_U
  specific = 4
FEATURE [App::DocumentObjectGroupPython] H_element139  label="H_element : 086"  # scripted group (container) (typed FeaturePython)
  n = 11
  ref = H_element
FEATURE [App::DocumentObjectGroupPython] C_element149  label="C_element : 094"  # scripted group (container) (typed FeaturePython)
  n = 10
  ref = C_element
FEATURE [App::DocumentObjectGroupPython] N_element068  label="N_element : 040"  # scripted group (container) (typed FeaturePython)
  n = 2
  ref = N_element
FEATURE [App::DocumentObjectGroupPython] O_element130  label="O_element : 081"  # scripted group (container) (typed FeaturePython)
  n = 9
  ref = O_element
FEATURE [App::DocumentObjectGroupPython] P_element019  label="P_element : 008"  # scripted group (container) (typed FeaturePython)
  n = 1
  ref = P_element
FEATURE [App::DocumentObjectGroupPython] G4_DNA_MU  # scripted group (container) (typed FeaturePython)
  Dunit = g/cm3
  Dvalue = 1
  Group = -> [H_element139,C_element149,N_element068,O_element130,P_element019]
  conduct = 2
  density = 1
  expand = 3
  formula = G4_DNA_MU
  name = G4_DNA_MU
  specific = 4
FEATURE [App::DocumentObjectGroupPython] BioChemical  # scripted group (container) (typed FeaturePython)
  Group = -> [G4_CYTOSINE,G4_THYMINE,G4_URACIL,G4_DNA_ADENINE,G4_DNA_GUANINE,G4_DNA_CYTOSINE,G4_DNA_THYMINE,G4_DNA_URACIL,G4_DNA_ADENOSINE,G4_DNA_GUANOSINE,G4_DNA_CYTIDINE,G4_DNA_URIDINE,G4_DNA_METHYLURIDINE,G4_DNA_MONOPHOSPHATE,G4_DNA_A,G4_DNA_G,G4_DNA_C,G4_DNA_U,G4_DNA_MU]
FEATURE [App::DocumentObjectGroupPython] G4Materials  # scripted group (container) (typed FeaturePython)
  Group = -> [NIST,Element,HEP,Space,BioChemical]
  version = 1
FEATURE [App::DocumentObjectGroupPython] Geant4  # scripted group (container) (typed FeaturePython)
  Group = -> [G4Isotopes,G4Elements,G4Materials]
FEATURE [App::DocumentObjectGroupPython] Materials  # scripted group (container) (typed FeaturePython)
  Group = -> [Geant4]
FEATURE [Part::FeaturePython] GDMLBox_WorldBox  # WARN: FeaturePython — macro-defined, semantics opaque (R4)
  lunit = 2
  material = 5
  x = 200.2
  y = 130
  z = 130
FEATURE [Part::FeaturePython] GDMLBox_Box  # WARN: FeaturePython — macro-defined, semantics opaque (R4)
  Placement = pos=(30,0,0) rot=(0,0,1;0rad)
  lunit = 2
  material = 0
  x = 10
  y = 10
  z = 10
FEATURE [Part::FeaturePython] GDMLTorus  # WARN: FeaturePython — macro-defined, semantics opaque (R4)
  Placement = pos=(30,0,0) rot=(0,1,0;1.5708rad)
  aunit = deg
  deltaphi = 360
  lunit = 2
  material = 0
  rmax = 2
  rmin = 0
  rtor = 8
  startphi = 0
FEATURE [Part::MultiFuse] Fusion
  Shapes = -> [GDMLBox_Box,GDMLTorus]
FEATURE [Part::FeaturePython] Array  # Draft array (typed FeaturePython)
  AlwaysSyncPlacement = false
  Angle = 180
  ArrayType = 1
  Axis = (0,0,1)
  Base = -> Fusion
  Center = (0,0,0)
  Count = 5
  ExpandArray = false
  Fuse = false
  IntervalAxis = (0,0,0)
  IntervalX = (50,0,0)
  IntervalY = (0,50,0)
  IntervalZ = (0,0,50)
  NumberCircles = 3
  NumberPolar = 5
  NumberX = 2
  NumberY = 2
  NumberZ = 1
  Placement = pos=(42,0,0) rot=(0,0,1;0rad)
  PlacementList = 5 placements: [(0,0,0),(0,0,0),(0,0,0),(0,0,0),(0,0,0)]
  RadialDistance = 50
  ScaleList = (5) [(1,1,1),(1,1,1),(1,1,1),(1,1,1),(1,1,1)]
  Symmetry = 1
  TangentialDistance = 25
FEATURE [App::Part] Part001
  Group = -> [Array]
  Origin = -> Origin004
FEATURE [App::Part] worldVOL
  Group = -> [GDMLBox_WorldBox,Part001]
  Origin = -> Origin
